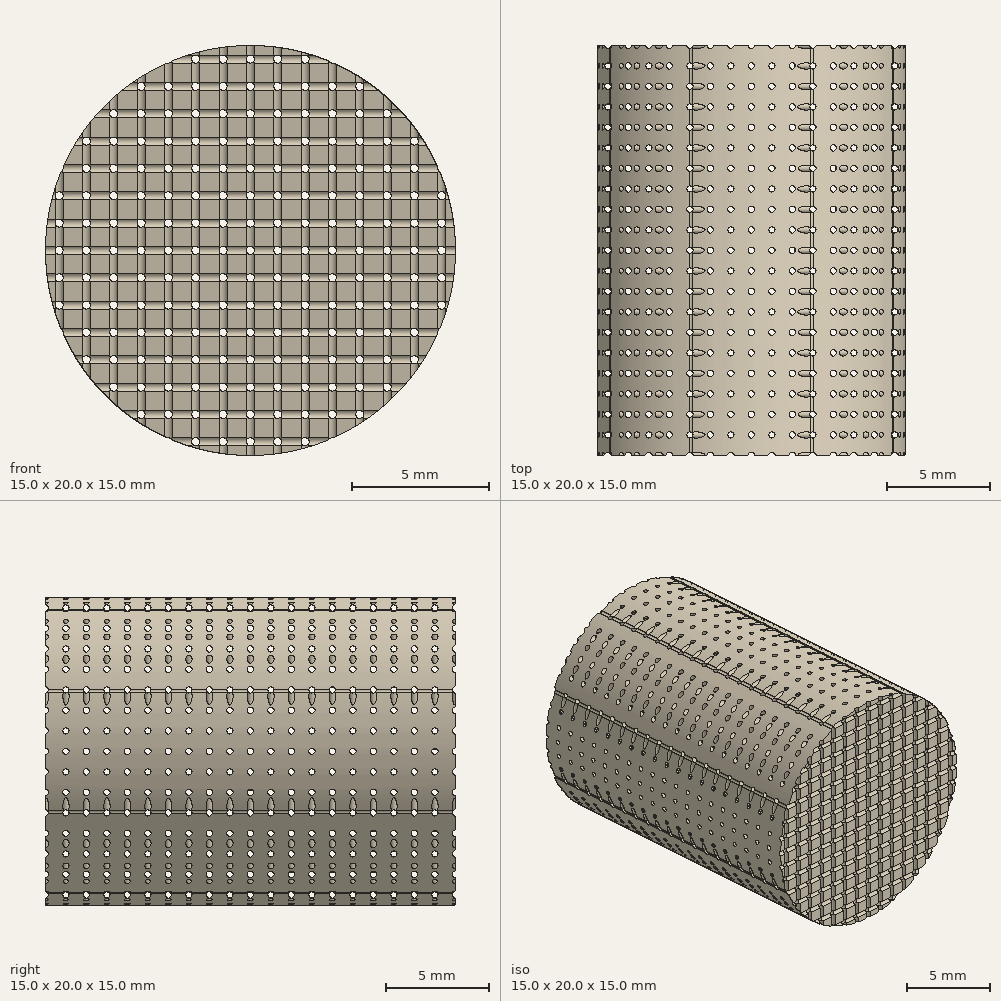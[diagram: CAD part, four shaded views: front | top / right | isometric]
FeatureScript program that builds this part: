
annotation { "Feature Type Name" : "Feature", "Feature Type Description" : "" }
export const myFeature = defineFeature(function(context is Context, id is Id, definition is map)
    precondition{}
    {
        {
            var Q0;
            Q0=qCreatedBy(makeId("Front.planeOp"),FACE);
            var sketch = newSketch(context, id + "F0", { "sketchPlane" : qUnion([Q0])});
            skCircle(sketch, "E0", {"center": v(0, 0) * mm, "radius": 7.5 * mm});
            skSolve(sketch);
        }
        {
            var Q0;
            Q0=qCreatedBy(makeId("Top.planeOp"),FACE);
            var sketch = newSketch(context, id + "F1", { "sketchPlane" : qUnion([Q0])});
            skLineSegment(sketch, "E1", {"start": v(0, 0) * mm, "end": v(0, 20) * mm});
            skSolve(sketch);
        }
        {
            var Q0;
            Q0 = qSketchRegion(id + "F0", true);
            var Q1;
            Q1 = qBodyType(qCreatedBy(id + "F1" ,EDGE), BodyType.WIRE);
            sweep(context, id + "F2", {"profiles" : qUnion([Q0]), "path" : qUnion([Q1])});
        }
        {
            var Q0;
            Q0=qCreatedBy(makeId("Front.planeOp"),FACE);
            var sketch = newSketch(context, id + "F3", { "sketchPlane" : qUnion([Q0])});
            skCircle(sketch, "E2", {"center": v(0, 0) * mm, "radius": 0.15 * mm});
            skCircle(sketch, "E3.0.1.0", {"center": v(0, 1) * mm, "radius": 0.15 * mm});
            skCircle(sketch, "E3.0.2.0", {"center": v(0, 2) * mm, "radius": 0.15 * mm});
            skCircle(sketch, "E3.0.3.0", {"center": v(0, 3) * mm, "radius": 0.15 * mm});
            skCircle(sketch, "E3.0.4.0", {"center": v(0, 4) * mm, "radius": 0.15 * mm});
            skCircle(sketch, "E3.0.5.0", {"center": v(0, 5) * mm, "radius": 0.15 * mm});
            skCircle(sketch, "E3.0.6.0", {"center": v(0, 6) * mm, "radius": 0.15 * mm});
            skCircle(sketch, "E3.0.7.0", {"center": v(0, 7) * mm, "radius": 0.15 * mm});
            skCircle(sketch, "E3.0.8.0", {"center": v(0, 8) * mm, "radius": 0.15 * mm});
            skCircle(sketch, "E3.0.9.0", {"center": v(0, 9) * mm, "radius": 0.15 * mm});
            skCircle(sketch, "E3.1.0.0", {"center": v(1, 0) * mm, "radius": 0.15 * mm});
            skCircle(sketch, "E3.1.1.0", {"center": v(1, 1) * mm, "radius": 0.15 * mm});
            skCircle(sketch, "E3.1.2.0", {"center": v(1, 2) * mm, "radius": 0.15 * mm});
            skCircle(sketch, "E3.1.3.0", {"center": v(1, 3) * mm, "radius": 0.15 * mm});
            skCircle(sketch, "E3.1.4.0", {"center": v(1, 4) * mm, "radius": 0.15 * mm});
            skCircle(sketch, "E3.1.5.0", {"center": v(1, 5) * mm, "radius": 0.15 * mm});
            skCircle(sketch, "E3.1.6.0", {"center": v(1, 6) * mm, "radius": 0.15 * mm});
            skCircle(sketch, "E3.1.7.0", {"center": v(1, 7) * mm, "radius": 0.15 * mm});
            skCircle(sketch, "E3.1.8.0", {"center": v(1, 8) * mm, "radius": 0.15 * mm});
            skCircle(sketch, "E3.1.9.0", {"center": v(1, 9) * mm, "radius": 0.15 * mm});
            skCircle(sketch, "E3.2.0.0", {"center": v(2, 0) * mm, "radius": 0.15 * mm});
            skCircle(sketch, "E3.2.1.0", {"center": v(2, 1) * mm, "radius": 0.15 * mm});
            skCircle(sketch, "E3.2.2.0", {"center": v(2, 2) * mm, "radius": 0.15 * mm});
            skCircle(sketch, "E3.2.3.0", {"center": v(2, 3) * mm, "radius": 0.15 * mm});
            skCircle(sketch, "E3.2.4.0", {"center": v(2, 4) * mm, "radius": 0.15 * mm});
            skCircle(sketch, "E3.2.5.0", {"center": v(2, 5) * mm, "radius": 0.15 * mm});
            skCircle(sketch, "E3.2.6.0", {"center": v(2, 6) * mm, "radius": 0.15 * mm});
            skCircle(sketch, "E3.2.7.0", {"center": v(2, 7) * mm, "radius": 0.15 * mm});
            skCircle(sketch, "E3.2.8.0", {"center": v(2, 8) * mm, "radius": 0.15 * mm});
            skCircle(sketch, "E3.2.9.0", {"center": v(2, 9) * mm, "radius": 0.15 * mm});
            skCircle(sketch, "E3.3.0.0", {"center": v(3, 0) * mm, "radius": 0.15 * mm});
            skCircle(sketch, "E3.3.1.0", {"center": v(3, 1) * mm, "radius": 0.15 * mm});
            skCircle(sketch, "E3.3.2.0", {"center": v(3, 2) * mm, "radius": 0.15 * mm});
            skCircle(sketch, "E3.3.3.0", {"center": v(3, 3) * mm, "radius": 0.15 * mm});
            skCircle(sketch, "E3.3.4.0", {"center": v(3, 4) * mm, "radius": 0.15 * mm});
            skCircle(sketch, "E3.3.5.0", {"center": v(3, 5) * mm, "radius": 0.15 * mm});
            skCircle(sketch, "E3.3.6.0", {"center": v(3, 6) * mm, "radius": 0.15 * mm});
            skCircle(sketch, "E3.3.7.0", {"center": v(3, 7) * mm, "radius": 0.15 * mm});
            skCircle(sketch, "E3.3.8.0", {"center": v(3, 8) * mm, "radius": 0.15 * mm});
            skCircle(sketch, "E3.3.9.0", {"center": v(3, 9) * mm, "radius": 0.15 * mm});
            skCircle(sketch, "E3.4.0.0", {"center": v(4, 0) * mm, "radius": 0.15 * mm});
            skCircle(sketch, "E3.4.1.0", {"center": v(4, 1) * mm, "radius": 0.15 * mm});
            skCircle(sketch, "E3.4.2.0", {"center": v(4, 2) * mm, "radius": 0.15 * mm});
            skCircle(sketch, "E3.4.3.0", {"center": v(4, 3) * mm, "radius": 0.15 * mm});
            skCircle(sketch, "E3.4.4.0", {"center": v(4, 4) * mm, "radius": 0.15 * mm});
            skCircle(sketch, "E3.4.5.0", {"center": v(4, 5) * mm, "radius": 0.15 * mm});
            skCircle(sketch, "E3.4.6.0", {"center": v(4, 6) * mm, "radius": 0.15 * mm});
            skCircle(sketch, "E3.4.7.0", {"center": v(4, 7) * mm, "radius": 0.15 * mm});
            skCircle(sketch, "E3.4.8.0", {"center": v(4, 8) * mm, "radius": 0.15 * mm});
            skCircle(sketch, "E3.4.9.0", {"center": v(4, 9) * mm, "radius": 0.15 * mm});
            skCircle(sketch, "E3.5.0.0", {"center": v(5, 0) * mm, "radius": 0.15 * mm});
            skCircle(sketch, "E3.5.1.0", {"center": v(5, 1) * mm, "radius": 0.15 * mm});
            skCircle(sketch, "E3.5.2.0", {"center": v(5, 2) * mm, "radius": 0.15 * mm});
            skCircle(sketch, "E3.5.3.0", {"center": v(5, 3) * mm, "radius": 0.15 * mm});
            skCircle(sketch, "E3.5.4.0", {"center": v(5, 4) * mm, "radius": 0.15 * mm});
            skCircle(sketch, "E3.5.5.0", {"center": v(5, 5) * mm, "radius": 0.15 * mm});
            skCircle(sketch, "E3.5.6.0", {"center": v(5, 6) * mm, "radius": 0.15 * mm});
            skCircle(sketch, "E3.5.7.0", {"center": v(5, 7) * mm, "radius": 0.15 * mm});
            skCircle(sketch, "E3.5.8.0", {"center": v(5, 8) * mm, "radius": 0.15 * mm});
            skCircle(sketch, "E3.5.9.0", {"center": v(5, 9) * mm, "radius": 0.15 * mm});
            skCircle(sketch, "E3.6.0.0", {"center": v(6, 0) * mm, "radius": 0.15 * mm});
            skCircle(sketch, "E3.6.1.0", {"center": v(6, 1) * mm, "radius": 0.15 * mm});
            skCircle(sketch, "E3.6.2.0", {"center": v(6, 2) * mm, "radius": 0.15 * mm});
            skCircle(sketch, "E3.6.3.0", {"center": v(6, 3) * mm, "radius": 0.15 * mm});
            skCircle(sketch, "E3.6.4.0", {"center": v(6, 4) * mm, "radius": 0.15 * mm});
            skCircle(sketch, "E3.6.5.0", {"center": v(6, 5) * mm, "radius": 0.15 * mm});
            skCircle(sketch, "E3.6.6.0", {"center": v(6, 6) * mm, "radius": 0.15 * mm});
            skCircle(sketch, "E3.6.7.0", {"center": v(6, 7) * mm, "radius": 0.15 * mm});
            skCircle(sketch, "E3.6.8.0", {"center": v(6, 8) * mm, "radius": 0.15 * mm});
            skCircle(sketch, "E3.6.9.0", {"center": v(6, 9) * mm, "radius": 0.15 * mm});
            skCircle(sketch, "E3.7.0.0", {"center": v(7, 0) * mm, "radius": 0.15 * mm});
            skCircle(sketch, "E3.7.1.0", {"center": v(7, 1) * mm, "radius": 0.15 * mm});
            skCircle(sketch, "E3.7.2.0", {"center": v(7, 2) * mm, "radius": 0.15 * mm});
            skCircle(sketch, "E3.7.3.0", {"center": v(7, 3) * mm, "radius": 0.15 * mm});
            skCircle(sketch, "E3.7.4.0", {"center": v(7, 4) * mm, "radius": 0.15 * mm});
            skCircle(sketch, "E3.7.5.0", {"center": v(7, 5) * mm, "radius": 0.15 * mm});
            skCircle(sketch, "E3.7.6.0", {"center": v(7, 6) * mm, "radius": 0.15 * mm});
            skCircle(sketch, "E3.7.7.0", {"center": v(7, 7) * mm, "radius": 0.15 * mm});
            skCircle(sketch, "E3.7.8.0", {"center": v(7, 8) * mm, "radius": 0.15 * mm});
            skCircle(sketch, "E3.7.9.0", {"center": v(7, 9) * mm, "radius": 0.15 * mm});
            skCircle(sketch, "E3.8.0.0", {"center": v(8, 0) * mm, "radius": 0.15 * mm});
            skCircle(sketch, "E3.8.1.0", {"center": v(8, 1) * mm, "radius": 0.15 * mm});
            skCircle(sketch, "E3.8.2.0", {"center": v(8, 2) * mm, "radius": 0.15 * mm});
            skCircle(sketch, "E3.8.3.0", {"center": v(8, 3) * mm, "radius": 0.15 * mm});
            skCircle(sketch, "E3.8.4.0", {"center": v(8, 4) * mm, "radius": 0.15 * mm});
            skCircle(sketch, "E3.8.5.0", {"center": v(8, 5) * mm, "radius": 0.15 * mm});
            skCircle(sketch, "E3.8.6.0", {"center": v(8, 6) * mm, "radius": 0.15 * mm});
            skCircle(sketch, "E3.8.7.0", {"center": v(8, 7) * mm, "radius": 0.15 * mm});
            skCircle(sketch, "E3.8.8.0", {"center": v(8, 8) * mm, "radius": 0.15 * mm});
            skCircle(sketch, "E3.8.9.0", {"center": v(8, 9) * mm, "radius": 0.15 * mm});
            skCircle(sketch, "E3.9.0.0", {"center": v(9, 0) * mm, "radius": 0.15 * mm});
            skCircle(sketch, "E3.9.1.0", {"center": v(9, 1) * mm, "radius": 0.15 * mm});
            skCircle(sketch, "E3.9.2.0", {"center": v(9, 2) * mm, "radius": 0.15 * mm});
            skCircle(sketch, "E3.9.3.0", {"center": v(9, 3) * mm, "radius": 0.15 * mm});
            skCircle(sketch, "E3.9.4.0", {"center": v(9, 4) * mm, "radius": 0.15 * mm});
            skCircle(sketch, "E3.9.5.0", {"center": v(9, 5) * mm, "radius": 0.15 * mm});
            skCircle(sketch, "E3.9.6.0", {"center": v(9, 6) * mm, "radius": 0.15 * mm});
            skCircle(sketch, "E3.9.7.0", {"center": v(9, 7) * mm, "radius": 0.15 * mm});
            skCircle(sketch, "E3.9.8.0", {"center": v(9, 8) * mm, "radius": 0.15 * mm});
            skCircle(sketch, "E3.9.9.0", {"center": v(9, 9) * mm, "radius": 0.15 * mm});
            skLineSegment(sketch, "E3.direction1", {"start": v(0, 0) * mm, "end": v(1, 0) * mm, "construction": true});
            skLineSegment(sketch, "E3.direction2", {"start": v(0, 0) * mm, "end": v(0, 1) * mm, "construction": true});
            skCircle(sketch, "E4.0.10.0", {"center": v(9, -1) * mm, "radius": 0.15 * mm});
            skCircle(sketch, "E4.0.11.0", {"center": v(9, -2) * mm, "radius": 0.15 * mm});
            skCircle(sketch, "E4.0.12.0", {"center": v(9, -3) * mm, "radius": 0.15 * mm});
            skCircle(sketch, "E4.0.13.0", {"center": v(9, -4) * mm, "radius": 0.15 * mm});
            skCircle(sketch, "E4.0.14.0", {"center": v(9, -5) * mm, "radius": 0.15 * mm});
            skCircle(sketch, "E4.0.15.0", {"center": v(9, -6) * mm, "radius": 0.15 * mm});
            skCircle(sketch, "E4.0.16.0", {"center": v(9, -7) * mm, "radius": 0.15 * mm});
            skCircle(sketch, "E4.0.17.0", {"center": v(9, -8) * mm, "radius": 0.15 * mm});
            skCircle(sketch, "E4.0.18.0", {"center": v(9, -9) * mm, "radius": 0.15 * mm});
            skCircle(sketch, "E4.0.19.0", {"center": v(9, -10) * mm, "radius": 0.15 * mm});
            skCircle(sketch, "E4.1.10.0", {"center": v(8, -1) * mm, "radius": 0.15 * mm});
            skCircle(sketch, "E4.1.11.0", {"center": v(8, -2) * mm, "radius": 0.15 * mm});
            skCircle(sketch, "E4.1.12.0", {"center": v(8, -3) * mm, "radius": 0.15 * mm});
            skCircle(sketch, "E4.1.13.0", {"center": v(8, -4) * mm, "radius": 0.15 * mm});
            skCircle(sketch, "E4.1.14.0", {"center": v(8, -5) * mm, "radius": 0.15 * mm});
            skCircle(sketch, "E4.1.15.0", {"center": v(8, -6) * mm, "radius": 0.15 * mm});
            skCircle(sketch, "E4.1.16.0", {"center": v(8, -7) * mm, "radius": 0.15 * mm});
            skCircle(sketch, "E4.1.17.0", {"center": v(8, -8) * mm, "radius": 0.15 * mm});
            skCircle(sketch, "E4.1.18.0", {"center": v(8, -9) * mm, "radius": 0.15 * mm});
            skCircle(sketch, "E4.1.19.0", {"center": v(8, -10) * mm, "radius": 0.15 * mm});
            skCircle(sketch, "E4.2.10.0", {"center": v(7, -1) * mm, "radius": 0.15 * mm});
            skCircle(sketch, "E4.2.11.0", {"center": v(7, -2) * mm, "radius": 0.15 * mm});
            skCircle(sketch, "E4.2.12.0", {"center": v(7, -3) * mm, "radius": 0.15 * mm});
            skCircle(sketch, "E4.2.13.0", {"center": v(7, -4) * mm, "radius": 0.15 * mm});
            skCircle(sketch, "E4.2.14.0", {"center": v(7, -5) * mm, "radius": 0.15 * mm});
            skCircle(sketch, "E4.2.15.0", {"center": v(7, -6) * mm, "radius": 0.15 * mm});
            skCircle(sketch, "E4.2.16.0", {"center": v(7, -7) * mm, "radius": 0.15 * mm});
            skCircle(sketch, "E4.2.17.0", {"center": v(7, -8) * mm, "radius": 0.15 * mm});
            skCircle(sketch, "E4.2.18.0", {"center": v(7, -9) * mm, "radius": 0.15 * mm});
            skCircle(sketch, "E4.2.19.0", {"center": v(7, -10) * mm, "radius": 0.15 * mm});
            skCircle(sketch, "E4.3.10.0", {"center": v(6, -1) * mm, "radius": 0.15 * mm});
            skCircle(sketch, "E4.3.11.0", {"center": v(6, -2) * mm, "radius": 0.15 * mm});
            skCircle(sketch, "E4.3.12.0", {"center": v(6, -3) * mm, "radius": 0.15 * mm});
            skCircle(sketch, "E4.3.13.0", {"center": v(6, -4) * mm, "radius": 0.15 * mm});
            skCircle(sketch, "E4.3.14.0", {"center": v(6, -5) * mm, "radius": 0.15 * mm});
            skCircle(sketch, "E4.3.15.0", {"center": v(6, -6) * mm, "radius": 0.15 * mm});
            skCircle(sketch, "E4.3.16.0", {"center": v(6, -7) * mm, "radius": 0.15 * mm});
            skCircle(sketch, "E4.3.17.0", {"center": v(6, -8) * mm, "radius": 0.15 * mm});
            skCircle(sketch, "E4.3.18.0", {"center": v(6, -9) * mm, "radius": 0.15 * mm});
            skCircle(sketch, "E4.3.19.0", {"center": v(6, -10) * mm, "radius": 0.15 * mm});
            skCircle(sketch, "E4.4.10.0", {"center": v(5, -1) * mm, "radius": 0.15 * mm});
            skCircle(sketch, "E4.4.11.0", {"center": v(5, -2) * mm, "radius": 0.15 * mm});
            skCircle(sketch, "E4.4.12.0", {"center": v(5, -3) * mm, "radius": 0.15 * mm});
            skCircle(sketch, "E4.4.13.0", {"center": v(5, -4) * mm, "radius": 0.15 * mm});
            skCircle(sketch, "E4.4.14.0", {"center": v(5, -5) * mm, "radius": 0.15 * mm});
            skCircle(sketch, "E4.4.15.0", {"center": v(5, -6) * mm, "radius": 0.15 * mm});
            skCircle(sketch, "E4.4.16.0", {"center": v(5, -7) * mm, "radius": 0.15 * mm});
            skCircle(sketch, "E4.4.17.0", {"center": v(5, -8) * mm, "radius": 0.15 * mm});
            skCircle(sketch, "E4.4.18.0", {"center": v(5, -9) * mm, "radius": 0.15 * mm});
            skCircle(sketch, "E4.4.19.0", {"center": v(5, -10) * mm, "radius": 0.15 * mm});
            skCircle(sketch, "E4.5.10.0", {"center": v(4, -1) * mm, "radius": 0.15 * mm});
            skCircle(sketch, "E4.5.11.0", {"center": v(4, -2) * mm, "radius": 0.15 * mm});
            skCircle(sketch, "E4.5.12.0", {"center": v(4, -3) * mm, "radius": 0.15 * mm});
            skCircle(sketch, "E4.5.13.0", {"center": v(4, -4) * mm, "radius": 0.15 * mm});
            skCircle(sketch, "E4.5.14.0", {"center": v(4, -5) * mm, "radius": 0.15 * mm});
            skCircle(sketch, "E4.5.15.0", {"center": v(4, -6) * mm, "radius": 0.15 * mm});
            skCircle(sketch, "E4.5.16.0", {"center": v(4, -7) * mm, "radius": 0.15 * mm});
            skCircle(sketch, "E4.5.17.0", {"center": v(4, -8) * mm, "radius": 0.15 * mm});
            skCircle(sketch, "E4.5.18.0", {"center": v(4, -9) * mm, "radius": 0.15 * mm});
            skCircle(sketch, "E4.5.19.0", {"center": v(4, -10) * mm, "radius": 0.15 * mm});
            skCircle(sketch, "E4.6.10.0", {"center": v(3, -1) * mm, "radius": 0.15 * mm});
            skCircle(sketch, "E4.6.11.0", {"center": v(3, -2) * mm, "radius": 0.15 * mm});
            skCircle(sketch, "E4.6.12.0", {"center": v(3, -3) * mm, "radius": 0.15 * mm});
            skCircle(sketch, "E4.6.13.0", {"center": v(3, -4) * mm, "radius": 0.15 * mm});
            skCircle(sketch, "E4.6.14.0", {"center": v(3, -5) * mm, "radius": 0.15 * mm});
            skCircle(sketch, "E4.6.15.0", {"center": v(3, -6) * mm, "radius": 0.15 * mm});
            skCircle(sketch, "E4.6.16.0", {"center": v(3, -7) * mm, "radius": 0.15 * mm});
            skCircle(sketch, "E4.6.17.0", {"center": v(3, -8) * mm, "radius": 0.15 * mm});
            skCircle(sketch, "E4.6.18.0", {"center": v(3, -9) * mm, "radius": 0.15 * mm});
            skCircle(sketch, "E4.6.19.0", {"center": v(3, -10) * mm, "radius": 0.15 * mm});
            skCircle(sketch, "E4.7.10.0", {"center": v(2, -1) * mm, "radius": 0.15 * mm});
            skCircle(sketch, "E4.7.11.0", {"center": v(2, -2) * mm, "radius": 0.15 * mm});
            skCircle(sketch, "E4.7.12.0", {"center": v(2, -3) * mm, "radius": 0.15 * mm});
            skCircle(sketch, "E4.7.13.0", {"center": v(2, -4) * mm, "radius": 0.15 * mm});
            skCircle(sketch, "E4.7.14.0", {"center": v(2, -5) * mm, "radius": 0.15 * mm});
            skCircle(sketch, "E4.7.15.0", {"center": v(2, -6) * mm, "radius": 0.15 * mm});
            skCircle(sketch, "E4.7.16.0", {"center": v(2, -7) * mm, "radius": 0.15 * mm});
            skCircle(sketch, "E4.7.17.0", {"center": v(2, -8) * mm, "radius": 0.15 * mm});
            skCircle(sketch, "E4.7.18.0", {"center": v(2, -9) * mm, "radius": 0.15 * mm});
            skCircle(sketch, "E4.7.19.0", {"center": v(2, -10) * mm, "radius": 0.15 * mm});
            skCircle(sketch, "E4.8.10.0", {"center": v(1, -1) * mm, "radius": 0.15 * mm});
            skCircle(sketch, "E4.8.11.0", {"center": v(1, -2) * mm, "radius": 0.15 * mm});
            skCircle(sketch, "E4.8.12.0", {"center": v(1, -3) * mm, "radius": 0.15 * mm});
            skCircle(sketch, "E4.8.13.0", {"center": v(1, -4) * mm, "radius": 0.15 * mm});
            skCircle(sketch, "E4.8.14.0", {"center": v(1, -5) * mm, "radius": 0.15 * mm});
            skCircle(sketch, "E4.8.15.0", {"center": v(1, -6) * mm, "radius": 0.15 * mm});
            skCircle(sketch, "E4.8.16.0", {"center": v(1, -7) * mm, "radius": 0.15 * mm});
            skCircle(sketch, "E4.8.17.0", {"center": v(1, -8) * mm, "radius": 0.15 * mm});
            skCircle(sketch, "E4.8.18.0", {"center": v(1, -9) * mm, "radius": 0.15 * mm});
            skCircle(sketch, "E4.8.19.0", {"center": v(1, -10) * mm, "radius": 0.15 * mm});
            skCircle(sketch, "E4.9.10.0", {"center": v(0, -1) * mm, "radius": 0.15 * mm});
            skCircle(sketch, "E4.9.11.0", {"center": v(0, -2) * mm, "radius": 0.15 * mm});
            skCircle(sketch, "E4.9.12.0", {"center": v(0, -3) * mm, "radius": 0.15 * mm});
            skCircle(sketch, "E4.9.13.0", {"center": v(0, -4) * mm, "radius": 0.15 * mm});
            skCircle(sketch, "E4.9.14.0", {"center": v(0, -5) * mm, "radius": 0.15 * mm});
            skCircle(sketch, "E4.9.15.0", {"center": v(0, -6) * mm, "radius": 0.15 * mm});
            skCircle(sketch, "E4.9.16.0", {"center": v(0, -7) * mm, "radius": 0.15 * mm});
            skCircle(sketch, "E4.9.17.0", {"center": v(0, -8) * mm, "radius": 0.15 * mm});
            skCircle(sketch, "E4.9.18.0", {"center": v(0, -9) * mm, "radius": 0.15 * mm});
            skCircle(sketch, "E4.9.19.0", {"center": v(0, -10) * mm, "radius": 0.15 * mm});
            skCircle(sketch, "E4.10.0.0", {"center": v(-1, 9) * mm, "radius": 0.15 * mm});
            skCircle(sketch, "E4.10.1.0", {"center": v(-1, 8) * mm, "radius": 0.15 * mm});
            skCircle(sketch, "E4.10.2.0", {"center": v(-1, 7) * mm, "radius": 0.15 * mm});
            skCircle(sketch, "E4.10.3.0", {"center": v(-1, 6) * mm, "radius": 0.15 * mm});
            skCircle(sketch, "E4.10.4.0", {"center": v(-1, 5) * mm, "radius": 0.15 * mm});
            skCircle(sketch, "E4.10.5.0", {"center": v(-1, 4) * mm, "radius": 0.15 * mm});
            skCircle(sketch, "E4.10.6.0", {"center": v(-1, 3) * mm, "radius": 0.15 * mm});
            skCircle(sketch, "E4.10.7.0", {"center": v(-1, 2) * mm, "radius": 0.15 * mm});
            skCircle(sketch, "E4.10.8.0", {"center": v(-1, 1) * mm, "radius": 0.15 * mm});
            skCircle(sketch, "E4.10.9.0", {"center": v(-1, 0) * mm, "radius": 0.15 * mm});
            skCircle(sketch, "E4.10.10.0", {"center": v(-1, -1) * mm, "radius": 0.15 * mm});
            skCircle(sketch, "E4.10.11.0", {"center": v(-1, -2) * mm, "radius": 0.15 * mm});
            skCircle(sketch, "E4.10.12.0", {"center": v(-1, -3) * mm, "radius": 0.15 * mm});
            skCircle(sketch, "E4.10.13.0", {"center": v(-1, -4) * mm, "radius": 0.15 * mm});
            skCircle(sketch, "E4.10.14.0", {"center": v(-1, -5) * mm, "radius": 0.15 * mm});
            skCircle(sketch, "E4.10.15.0", {"center": v(-1, -6) * mm, "radius": 0.15 * mm});
            skCircle(sketch, "E4.10.16.0", {"center": v(-1, -7) * mm, "radius": 0.15 * mm});
            skCircle(sketch, "E4.10.17.0", {"center": v(-1, -8) * mm, "radius": 0.15 * mm});
            skCircle(sketch, "E4.10.18.0", {"center": v(-1, -9) * mm, "radius": 0.15 * mm});
            skCircle(sketch, "E4.10.19.0", {"center": v(-1, -10) * mm, "radius": 0.15 * mm});
            skCircle(sketch, "E4.11.0.0", {"center": v(-2, 9) * mm, "radius": 0.15 * mm});
            skCircle(sketch, "E4.11.1.0", {"center": v(-2, 8) * mm, "radius": 0.15 * mm});
            skCircle(sketch, "E4.11.2.0", {"center": v(-2, 7) * mm, "radius": 0.15 * mm});
            skCircle(sketch, "E4.11.3.0", {"center": v(-2, 6) * mm, "radius": 0.15 * mm});
            skCircle(sketch, "E4.11.4.0", {"center": v(-2, 5) * mm, "radius": 0.15 * mm});
            skCircle(sketch, "E4.11.5.0", {"center": v(-2, 4) * mm, "radius": 0.15 * mm});
            skCircle(sketch, "E4.11.6.0", {"center": v(-2, 3) * mm, "radius": 0.15 * mm});
            skCircle(sketch, "E4.11.7.0", {"center": v(-2, 2) * mm, "radius": 0.15 * mm});
            skCircle(sketch, "E4.11.8.0", {"center": v(-2, 1) * mm, "radius": 0.15 * mm});
            skCircle(sketch, "E4.11.9.0", {"center": v(-2, 0) * mm, "radius": 0.15 * mm});
            skCircle(sketch, "E4.11.10.0", {"center": v(-2, -1) * mm, "radius": 0.15 * mm});
            skCircle(sketch, "E4.11.11.0", {"center": v(-2, -2) * mm, "radius": 0.15 * mm});
            skCircle(sketch, "E4.11.12.0", {"center": v(-2, -3) * mm, "radius": 0.15 * mm});
            skCircle(sketch, "E4.11.13.0", {"center": v(-2, -4) * mm, "radius": 0.15 * mm});
            skCircle(sketch, "E4.11.14.0", {"center": v(-2, -5) * mm, "radius": 0.15 * mm});
            skCircle(sketch, "E4.11.15.0", {"center": v(-2, -6) * mm, "radius": 0.15 * mm});
            skCircle(sketch, "E4.11.16.0", {"center": v(-2, -7) * mm, "radius": 0.15 * mm});
            skCircle(sketch, "E4.11.17.0", {"center": v(-2, -8) * mm, "radius": 0.15 * mm});
            skCircle(sketch, "E4.11.18.0", {"center": v(-2, -9) * mm, "radius": 0.15 * mm});
            skCircle(sketch, "E4.11.19.0", {"center": v(-2, -10) * mm, "radius": 0.15 * mm});
            skCircle(sketch, "E4.12.0.0", {"center": v(-3, 9) * mm, "radius": 0.15 * mm});
            skCircle(sketch, "E4.12.1.0", {"center": v(-3, 8) * mm, "radius": 0.15 * mm});
            skCircle(sketch, "E4.12.2.0", {"center": v(-3, 7) * mm, "radius": 0.15 * mm});
            skCircle(sketch, "E4.12.3.0", {"center": v(-3, 6) * mm, "radius": 0.15 * mm});
            skCircle(sketch, "E4.12.4.0", {"center": v(-3, 5) * mm, "radius": 0.15 * mm});
            skCircle(sketch, "E4.12.5.0", {"center": v(-3, 4) * mm, "radius": 0.15 * mm});
            skCircle(sketch, "E4.12.6.0", {"center": v(-3, 3) * mm, "radius": 0.15 * mm});
            skCircle(sketch, "E4.12.7.0", {"center": v(-3, 2) * mm, "radius": 0.15 * mm});
            skCircle(sketch, "E4.12.8.0", {"center": v(-3, 1) * mm, "radius": 0.15 * mm});
            skCircle(sketch, "E4.12.9.0", {"center": v(-3, 0) * mm, "radius": 0.15 * mm});
            skCircle(sketch, "E4.12.10.0", {"center": v(-3, -1) * mm, "radius": 0.15 * mm});
            skCircle(sketch, "E4.12.11.0", {"center": v(-3, -2) * mm, "radius": 0.15 * mm});
            skCircle(sketch, "E4.12.12.0", {"center": v(-3, -3) * mm, "radius": 0.15 * mm});
            skCircle(sketch, "E4.12.13.0", {"center": v(-3, -4) * mm, "radius": 0.15 * mm});
            skCircle(sketch, "E4.12.14.0", {"center": v(-3, -5) * mm, "radius": 0.15 * mm});
            skCircle(sketch, "E4.12.15.0", {"center": v(-3, -6) * mm, "radius": 0.15 * mm});
            skCircle(sketch, "E4.12.16.0", {"center": v(-3, -7) * mm, "radius": 0.15 * mm});
            skCircle(sketch, "E4.12.17.0", {"center": v(-3, -8) * mm, "radius": 0.15 * mm});
            skCircle(sketch, "E4.12.18.0", {"center": v(-3, -9) * mm, "radius": 0.15 * mm});
            skCircle(sketch, "E4.12.19.0", {"center": v(-3, -10) * mm, "radius": 0.15 * mm});
            skCircle(sketch, "E4.13.0.0", {"center": v(-4, 9) * mm, "radius": 0.15 * mm});
            skCircle(sketch, "E4.13.1.0", {"center": v(-4, 8) * mm, "radius": 0.15 * mm});
            skCircle(sketch, "E4.13.2.0", {"center": v(-4, 7) * mm, "radius": 0.15 * mm});
            skCircle(sketch, "E4.13.3.0", {"center": v(-4, 6) * mm, "radius": 0.15 * mm});
            skCircle(sketch, "E4.13.4.0", {"center": v(-4, 5) * mm, "radius": 0.15 * mm});
            skCircle(sketch, "E4.13.5.0", {"center": v(-4, 4) * mm, "radius": 0.15 * mm});
            skCircle(sketch, "E4.13.6.0", {"center": v(-4, 3) * mm, "radius": 0.15 * mm});
            skCircle(sketch, "E4.13.7.0", {"center": v(-4, 2) * mm, "radius": 0.15 * mm});
            skCircle(sketch, "E4.13.8.0", {"center": v(-4, 1) * mm, "radius": 0.15 * mm});
            skCircle(sketch, "E4.13.9.0", {"center": v(-4, 0) * mm, "radius": 0.15 * mm});
            skCircle(sketch, "E4.13.10.0", {"center": v(-4, -1) * mm, "radius": 0.15 * mm});
            skCircle(sketch, "E4.13.11.0", {"center": v(-4, -2) * mm, "radius": 0.15 * mm});
            skCircle(sketch, "E4.13.12.0", {"center": v(-4, -3) * mm, "radius": 0.15 * mm});
            skCircle(sketch, "E4.13.13.0", {"center": v(-4, -4) * mm, "radius": 0.15 * mm});
            skCircle(sketch, "E4.13.14.0", {"center": v(-4, -5) * mm, "radius": 0.15 * mm});
            skCircle(sketch, "E4.13.15.0", {"center": v(-4, -6) * mm, "radius": 0.15 * mm});
            skCircle(sketch, "E4.13.16.0", {"center": v(-4, -7) * mm, "radius": 0.15 * mm});
            skCircle(sketch, "E4.13.17.0", {"center": v(-4, -8) * mm, "radius": 0.15 * mm});
            skCircle(sketch, "E4.13.18.0", {"center": v(-4, -9) * mm, "radius": 0.15 * mm});
            skCircle(sketch, "E4.13.19.0", {"center": v(-4, -10) * mm, "radius": 0.15 * mm});
            skCircle(sketch, "E4.14.0.0", {"center": v(-5, 9) * mm, "radius": 0.15 * mm});
            skCircle(sketch, "E4.14.1.0", {"center": v(-5, 8) * mm, "radius": 0.15 * mm});
            skCircle(sketch, "E4.14.2.0", {"center": v(-5, 7) * mm, "radius": 0.15 * mm});
            skCircle(sketch, "E4.14.3.0", {"center": v(-5, 6) * mm, "radius": 0.15 * mm});
            skCircle(sketch, "E4.14.4.0", {"center": v(-5, 5) * mm, "radius": 0.15 * mm});
            skCircle(sketch, "E4.14.5.0", {"center": v(-5, 4) * mm, "radius": 0.15 * mm});
            skCircle(sketch, "E4.14.6.0", {"center": v(-5, 3) * mm, "radius": 0.15 * mm});
            skCircle(sketch, "E4.14.7.0", {"center": v(-5, 2) * mm, "radius": 0.15 * mm});
            skCircle(sketch, "E4.14.8.0", {"center": v(-5, 1) * mm, "radius": 0.15 * mm});
            skCircle(sketch, "E4.14.9.0", {"center": v(-5, 0) * mm, "radius": 0.15 * mm});
            skCircle(sketch, "E4.14.10.0", {"center": v(-5, -1) * mm, "radius": 0.15 * mm});
            skCircle(sketch, "E4.14.11.0", {"center": v(-5, -2) * mm, "radius": 0.15 * mm});
            skCircle(sketch, "E4.14.12.0", {"center": v(-5, -3) * mm, "radius": 0.15 * mm});
            skCircle(sketch, "E4.14.13.0", {"center": v(-5, -4) * mm, "radius": 0.15 * mm});
            skCircle(sketch, "E4.14.14.0", {"center": v(-5, -5) * mm, "radius": 0.15 * mm});
            skCircle(sketch, "E4.14.15.0", {"center": v(-5, -6) * mm, "radius": 0.15 * mm});
            skCircle(sketch, "E4.14.16.0", {"center": v(-5, -7) * mm, "radius": 0.15 * mm});
            skCircle(sketch, "E4.14.17.0", {"center": v(-5, -8) * mm, "radius": 0.15 * mm});
            skCircle(sketch, "E4.14.18.0", {"center": v(-5, -9) * mm, "radius": 0.15 * mm});
            skCircle(sketch, "E4.14.19.0", {"center": v(-5, -10) * mm, "radius": 0.15 * mm});
            skCircle(sketch, "E4.15.0.0", {"center": v(-6, 9) * mm, "radius": 0.15 * mm});
            skCircle(sketch, "E4.15.1.0", {"center": v(-6, 8) * mm, "radius": 0.15 * mm});
            skCircle(sketch, "E4.15.2.0", {"center": v(-6, 7) * mm, "radius": 0.15 * mm});
            skCircle(sketch, "E4.15.3.0", {"center": v(-6, 6) * mm, "radius": 0.15 * mm});
            skCircle(sketch, "E4.15.4.0", {"center": v(-6, 5) * mm, "radius": 0.15 * mm});
            skCircle(sketch, "E4.15.5.0", {"center": v(-6, 4) * mm, "radius": 0.15 * mm});
            skCircle(sketch, "E4.15.6.0", {"center": v(-6, 3) * mm, "radius": 0.15 * mm});
            skCircle(sketch, "E4.15.7.0", {"center": v(-6, 2) * mm, "radius": 0.15 * mm});
            skCircle(sketch, "E4.15.8.0", {"center": v(-6, 1) * mm, "radius": 0.15 * mm});
            skCircle(sketch, "E4.15.9.0", {"center": v(-6, 0) * mm, "radius": 0.15 * mm});
            skCircle(sketch, "E4.15.10.0", {"center": v(-6, -1) * mm, "radius": 0.15 * mm});
            skCircle(sketch, "E4.15.11.0", {"center": v(-6, -2) * mm, "radius": 0.15 * mm});
            skCircle(sketch, "E4.15.12.0", {"center": v(-6, -3) * mm, "radius": 0.15 * mm});
            skCircle(sketch, "E4.15.13.0", {"center": v(-6, -4) * mm, "radius": 0.15 * mm});
            skCircle(sketch, "E4.15.14.0", {"center": v(-6, -5) * mm, "radius": 0.15 * mm});
            skCircle(sketch, "E4.15.15.0", {"center": v(-6, -6) * mm, "radius": 0.15 * mm});
            skCircle(sketch, "E4.15.16.0", {"center": v(-6, -7) * mm, "radius": 0.15 * mm});
            skCircle(sketch, "E4.15.17.0", {"center": v(-6, -8) * mm, "radius": 0.15 * mm});
            skCircle(sketch, "E4.15.18.0", {"center": v(-6, -9) * mm, "radius": 0.15 * mm});
            skCircle(sketch, "E4.15.19.0", {"center": v(-6, -10) * mm, "radius": 0.15 * mm});
            skCircle(sketch, "E4.16.0.0", {"center": v(-7, 9) * mm, "radius": 0.15 * mm});
            skCircle(sketch, "E4.16.1.0", {"center": v(-7, 8) * mm, "radius": 0.15 * mm});
            skCircle(sketch, "E4.16.2.0", {"center": v(-7, 7) * mm, "radius": 0.15 * mm});
            skCircle(sketch, "E4.16.3.0", {"center": v(-7, 6) * mm, "radius": 0.15 * mm});
            skCircle(sketch, "E4.16.4.0", {"center": v(-7, 5) * mm, "radius": 0.15 * mm});
            skCircle(sketch, "E4.16.5.0", {"center": v(-7, 4) * mm, "radius": 0.15 * mm});
            skCircle(sketch, "E4.16.6.0", {"center": v(-7, 3) * mm, "radius": 0.15 * mm});
            skCircle(sketch, "E4.16.7.0", {"center": v(-7, 2) * mm, "radius": 0.15 * mm});
            skCircle(sketch, "E4.16.8.0", {"center": v(-7, 1) * mm, "radius": 0.15 * mm});
            skCircle(sketch, "E4.16.9.0", {"center": v(-7, 0) * mm, "radius": 0.15 * mm});
            skCircle(sketch, "E4.16.10.0", {"center": v(-7, -1) * mm, "radius": 0.15 * mm});
            skCircle(sketch, "E4.16.11.0", {"center": v(-7, -2) * mm, "radius": 0.15 * mm});
            skCircle(sketch, "E4.16.12.0", {"center": v(-7, -3) * mm, "radius": 0.15 * mm});
            skCircle(sketch, "E4.16.13.0", {"center": v(-7, -4) * mm, "radius": 0.15 * mm});
            skCircle(sketch, "E4.16.14.0", {"center": v(-7, -5) * mm, "radius": 0.15 * mm});
            skCircle(sketch, "E4.16.15.0", {"center": v(-7, -6) * mm, "radius": 0.15 * mm});
            skCircle(sketch, "E4.16.16.0", {"center": v(-7, -7) * mm, "radius": 0.15 * mm});
            skCircle(sketch, "E4.16.17.0", {"center": v(-7, -8) * mm, "radius": 0.15 * mm});
            skCircle(sketch, "E4.16.18.0", {"center": v(-7, -9) * mm, "radius": 0.15 * mm});
            skCircle(sketch, "E4.16.19.0", {"center": v(-7, -10) * mm, "radius": 0.15 * mm});
            skCircle(sketch, "E4.17.0.0", {"center": v(-8, 9) * mm, "radius": 0.15 * mm});
            skCircle(sketch, "E4.17.1.0", {"center": v(-8, 8) * mm, "radius": 0.15 * mm});
            skCircle(sketch, "E4.17.2.0", {"center": v(-8, 7) * mm, "radius": 0.15 * mm});
            skCircle(sketch, "E4.17.3.0", {"center": v(-8, 6) * mm, "radius": 0.15 * mm});
            skCircle(sketch, "E4.17.4.0", {"center": v(-8, 5) * mm, "radius": 0.15 * mm});
            skCircle(sketch, "E4.17.5.0", {"center": v(-8, 4) * mm, "radius": 0.15 * mm});
            skCircle(sketch, "E4.17.6.0", {"center": v(-8, 3) * mm, "radius": 0.15 * mm});
            skCircle(sketch, "E4.17.7.0", {"center": v(-8, 2) * mm, "radius": 0.15 * mm});
            skCircle(sketch, "E4.17.8.0", {"center": v(-8, 1) * mm, "radius": 0.15 * mm});
            skCircle(sketch, "E4.17.9.0", {"center": v(-8, 0) * mm, "radius": 0.15 * mm});
            skCircle(sketch, "E4.17.10.0", {"center": v(-8, -1) * mm, "radius": 0.15 * mm});
            skCircle(sketch, "E4.17.11.0", {"center": v(-8, -2) * mm, "radius": 0.15 * mm});
            skCircle(sketch, "E4.17.12.0", {"center": v(-8, -3) * mm, "radius": 0.15 * mm});
            skCircle(sketch, "E4.17.13.0", {"center": v(-8, -4) * mm, "radius": 0.15 * mm});
            skCircle(sketch, "E4.17.14.0", {"center": v(-8, -5) * mm, "radius": 0.15 * mm});
            skCircle(sketch, "E4.17.15.0", {"center": v(-8, -6) * mm, "radius": 0.15 * mm});
            skCircle(sketch, "E4.17.16.0", {"center": v(-8, -7) * mm, "radius": 0.15 * mm});
            skCircle(sketch, "E4.17.17.0", {"center": v(-8, -8) * mm, "radius": 0.15 * mm});
            skCircle(sketch, "E4.17.18.0", {"center": v(-8, -9) * mm, "radius": 0.15 * mm});
            skCircle(sketch, "E4.17.19.0", {"center": v(-8, -10) * mm, "radius": 0.15 * mm});
            skCircle(sketch, "E4.18.0.0", {"center": v(-9, 9) * mm, "radius": 0.15 * mm});
            skCircle(sketch, "E4.18.1.0", {"center": v(-9, 8) * mm, "radius": 0.15 * mm});
            skCircle(sketch, "E4.18.2.0", {"center": v(-9, 7) * mm, "radius": 0.15 * mm});
            skCircle(sketch, "E4.18.3.0", {"center": v(-9, 6) * mm, "radius": 0.15 * mm});
            skCircle(sketch, "E4.18.4.0", {"center": v(-9, 5) * mm, "radius": 0.15 * mm});
            skCircle(sketch, "E4.18.5.0", {"center": v(-9, 4) * mm, "radius": 0.15 * mm});
            skCircle(sketch, "E4.18.6.0", {"center": v(-9, 3) * mm, "radius": 0.15 * mm});
            skCircle(sketch, "E4.18.7.0", {"center": v(-9, 2) * mm, "radius": 0.15 * mm});
            skCircle(sketch, "E4.18.8.0", {"center": v(-9, 1) * mm, "radius": 0.15 * mm});
            skCircle(sketch, "E4.18.9.0", {"center": v(-9, 0) * mm, "radius": 0.15 * mm});
            skCircle(sketch, "E4.18.10.0", {"center": v(-9, -1) * mm, "radius": 0.15 * mm});
            skCircle(sketch, "E4.18.11.0", {"center": v(-9, -2) * mm, "radius": 0.15 * mm});
            skCircle(sketch, "E4.18.12.0", {"center": v(-9, -3) * mm, "radius": 0.15 * mm});
            skCircle(sketch, "E4.18.13.0", {"center": v(-9, -4) * mm, "radius": 0.15 * mm});
            skCircle(sketch, "E4.18.14.0", {"center": v(-9, -5) * mm, "radius": 0.15 * mm});
            skCircle(sketch, "E4.18.15.0", {"center": v(-9, -6) * mm, "radius": 0.15 * mm});
            skCircle(sketch, "E4.18.16.0", {"center": v(-9, -7) * mm, "radius": 0.15 * mm});
            skCircle(sketch, "E4.18.17.0", {"center": v(-9, -8) * mm, "radius": 0.15 * mm});
            skCircle(sketch, "E4.18.18.0", {"center": v(-9, -9) * mm, "radius": 0.15 * mm});
            skCircle(sketch, "E4.18.19.0", {"center": v(-9, -10) * mm, "radius": 0.15 * mm});
            skCircle(sketch, "E4.19.0.0", {"center": v(-10, 9) * mm, "radius": 0.15 * mm});
            skCircle(sketch, "E4.19.1.0", {"center": v(-10, 8) * mm, "radius": 0.15 * mm});
            skCircle(sketch, "E4.19.2.0", {"center": v(-10, 7) * mm, "radius": 0.15 * mm});
            skCircle(sketch, "E4.19.3.0", {"center": v(-10, 6) * mm, "radius": 0.15 * mm});
            skCircle(sketch, "E4.19.4.0", {"center": v(-10, 5) * mm, "radius": 0.15 * mm});
            skCircle(sketch, "E4.19.5.0", {"center": v(-10, 4) * mm, "radius": 0.15 * mm});
            skCircle(sketch, "E4.19.6.0", {"center": v(-10, 3) * mm, "radius": 0.15 * mm});
            skCircle(sketch, "E4.19.7.0", {"center": v(-10, 2) * mm, "radius": 0.15 * mm});
            skCircle(sketch, "E4.19.8.0", {"center": v(-10, 1) * mm, "radius": 0.15 * mm});
            skCircle(sketch, "E4.19.9.0", {"center": v(-10, 0) * mm, "radius": 0.15 * mm});
            skCircle(sketch, "E4.19.10.0", {"center": v(-10, -1) * mm, "radius": 0.15 * mm});
            skCircle(sketch, "E4.19.11.0", {"center": v(-10, -2) * mm, "radius": 0.15 * mm});
            skCircle(sketch, "E4.19.12.0", {"center": v(-10, -3) * mm, "radius": 0.15 * mm});
            skCircle(sketch, "E4.19.13.0", {"center": v(-10, -4) * mm, "radius": 0.15 * mm});
            skCircle(sketch, "E4.19.14.0", {"center": v(-10, -5) * mm, "radius": 0.15 * mm});
            skCircle(sketch, "E4.19.15.0", {"center": v(-10, -6) * mm, "radius": 0.15 * mm});
            skCircle(sketch, "E4.19.16.0", {"center": v(-10, -7) * mm, "radius": 0.15 * mm});
            skCircle(sketch, "E4.19.17.0", {"center": v(-10, -8) * mm, "radius": 0.15 * mm});
            skCircle(sketch, "E4.19.18.0", {"center": v(-10, -9) * mm, "radius": 0.15 * mm});
            skCircle(sketch, "E4.19.19.0", {"center": v(-10, -10) * mm, "radius": 0.15 * mm});
            skLineSegment(sketch, "E4.direction1", {"start": v(9, 9) * mm, "end": v(8, 9) * mm, "construction": true});
            skLineSegment(sketch, "E4.direction2", {"start": v(9, 9) * mm, "end": v(9, 8) * mm, "construction": true});
            skSolve(sketch);
        }
        {
            var Q0;
            Q0 = qSketchRegion(id + "F3", true);
            extrude(context, id + "F4", {"entities" : qUnion([Q0]), "operationType" : NewBodyOperationType.REMOVE, "oppositeDirection" : true, "depth" : 40 * mm, "offsetDistance" : 25 * mm});
        }
        {
            var Q0;
            Q0=qCreatedBy(makeId("Top.planeOp"),FACE);
            var sketch = newSketch(context, id + "F5", { "sketchPlane" : qUnion([Q0])});
            skCircle(sketch, "E5", {"center": v(0, 0) * mm, "radius": 0.15 * mm});
            skCircle(sketch, "E6.0.1.0", {"center": v(0, 1) * mm, "radius": 0.15 * mm});
            skCircle(sketch, "E6.0.2.0", {"center": v(0, 2) * mm, "radius": 0.15 * mm});
            skCircle(sketch, "E6.0.3.0", {"center": v(0, 3) * mm, "radius": 0.15 * mm});
            skCircle(sketch, "E6.0.4.0", {"center": v(0, 4) * mm, "radius": 0.15 * mm});
            skCircle(sketch, "E6.0.5.0", {"center": v(0, 5) * mm, "radius": 0.15 * mm});
            skCircle(sketch, "E6.0.6.0", {"center": v(0, 6) * mm, "radius": 0.15 * mm});
            skCircle(sketch, "E6.0.7.0", {"center": v(0, 7) * mm, "radius": 0.15 * mm});
            skCircle(sketch, "E6.0.8.0", {"center": v(0, 8) * mm, "radius": 0.15 * mm});
            skCircle(sketch, "E6.0.9.0", {"center": v(0, 9) * mm, "radius": 0.15 * mm});
            skCircle(sketch, "E6.1.0.0", {"center": v(1, 0) * mm, "radius": 0.15 * mm});
            skCircle(sketch, "E6.1.1.0", {"center": v(1, 1) * mm, "radius": 0.15 * mm});
            skCircle(sketch, "E6.1.2.0", {"center": v(1, 2) * mm, "radius": 0.15 * mm});
            skCircle(sketch, "E6.1.3.0", {"center": v(1, 3) * mm, "radius": 0.15 * mm});
            skCircle(sketch, "E6.1.4.0", {"center": v(1, 4) * mm, "radius": 0.15 * mm});
            skCircle(sketch, "E6.1.5.0", {"center": v(1, 5) * mm, "radius": 0.15 * mm});
            skCircle(sketch, "E6.1.6.0", {"center": v(1, 6) * mm, "radius": 0.15 * mm});
            skCircle(sketch, "E6.1.7.0", {"center": v(1, 7) * mm, "radius": 0.15 * mm});
            skCircle(sketch, "E6.1.8.0", {"center": v(1, 8) * mm, "radius": 0.15 * mm});
            skCircle(sketch, "E6.1.9.0", {"center": v(1, 9) * mm, "radius": 0.15 * mm});
            skCircle(sketch, "E6.2.0.0", {"center": v(2, 0) * mm, "radius": 0.15 * mm});
            skCircle(sketch, "E6.2.1.0", {"center": v(2, 1) * mm, "radius": 0.15 * mm});
            skCircle(sketch, "E6.2.2.0", {"center": v(2, 2) * mm, "radius": 0.15 * mm});
            skCircle(sketch, "E6.2.3.0", {"center": v(2, 3) * mm, "radius": 0.15 * mm});
            skCircle(sketch, "E6.2.4.0", {"center": v(2, 4) * mm, "radius": 0.15 * mm});
            skCircle(sketch, "E6.2.5.0", {"center": v(2, 5) * mm, "radius": 0.15 * mm});
            skCircle(sketch, "E6.2.6.0", {"center": v(2, 6) * mm, "radius": 0.15 * mm});
            skCircle(sketch, "E6.2.7.0", {"center": v(2, 7) * mm, "radius": 0.15 * mm});
            skCircle(sketch, "E6.2.8.0", {"center": v(2, 8) * mm, "radius": 0.15 * mm});
            skCircle(sketch, "E6.2.9.0", {"center": v(2, 9) * mm, "radius": 0.15 * mm});
            skCircle(sketch, "E6.3.0.0", {"center": v(3, 0) * mm, "radius": 0.15 * mm});
            skCircle(sketch, "E6.3.1.0", {"center": v(3, 1) * mm, "radius": 0.15 * mm});
            skCircle(sketch, "E6.3.2.0", {"center": v(3, 2) * mm, "radius": 0.15 * mm});
            skCircle(sketch, "E6.3.3.0", {"center": v(3, 3) * mm, "radius": 0.15 * mm});
            skCircle(sketch, "E6.3.4.0", {"center": v(3, 4) * mm, "radius": 0.15 * mm});
            skCircle(sketch, "E6.3.5.0", {"center": v(3, 5) * mm, "radius": 0.15 * mm});
            skCircle(sketch, "E6.3.6.0", {"center": v(3, 6) * mm, "radius": 0.15 * mm});
            skCircle(sketch, "E6.3.7.0", {"center": v(3, 7) * mm, "radius": 0.15 * mm});
            skCircle(sketch, "E6.3.8.0", {"center": v(3, 8) * mm, "radius": 0.15 * mm});
            skCircle(sketch, "E6.3.9.0", {"center": v(3, 9) * mm, "radius": 0.15 * mm});
            skCircle(sketch, "E6.4.0.0", {"center": v(4, 0) * mm, "radius": 0.15 * mm});
            skCircle(sketch, "E6.4.1.0", {"center": v(4, 1) * mm, "radius": 0.15 * mm});
            skCircle(sketch, "E6.4.2.0", {"center": v(4, 2) * mm, "radius": 0.15 * mm});
            skCircle(sketch, "E6.4.3.0", {"center": v(4, 3) * mm, "radius": 0.15 * mm});
            skCircle(sketch, "E6.4.4.0", {"center": v(4, 4) * mm, "radius": 0.15 * mm});
            skCircle(sketch, "E6.4.5.0", {"center": v(4, 5) * mm, "radius": 0.15 * mm});
            skCircle(sketch, "E6.4.6.0", {"center": v(4, 6) * mm, "radius": 0.15 * mm});
            skCircle(sketch, "E6.4.7.0", {"center": v(4, 7) * mm, "radius": 0.15 * mm});
            skCircle(sketch, "E6.4.8.0", {"center": v(4, 8) * mm, "radius": 0.15 * mm});
            skCircle(sketch, "E6.4.9.0", {"center": v(4, 9) * mm, "radius": 0.15 * mm});
            skCircle(sketch, "E6.5.0.0", {"center": v(5, 0) * mm, "radius": 0.15 * mm});
            skCircle(sketch, "E6.5.1.0", {"center": v(5, 1) * mm, "radius": 0.15 * mm});
            skCircle(sketch, "E6.5.2.0", {"center": v(5, 2) * mm, "radius": 0.15 * mm});
            skCircle(sketch, "E6.5.3.0", {"center": v(5, 3) * mm, "radius": 0.15 * mm});
            skCircle(sketch, "E6.5.4.0", {"center": v(5, 4) * mm, "radius": 0.15 * mm});
            skCircle(sketch, "E6.5.5.0", {"center": v(5, 5) * mm, "radius": 0.15 * mm});
            skCircle(sketch, "E6.5.6.0", {"center": v(5, 6) * mm, "radius": 0.15 * mm});
            skCircle(sketch, "E6.5.7.0", {"center": v(5, 7) * mm, "radius": 0.15 * mm});
            skCircle(sketch, "E6.5.8.0", {"center": v(5, 8) * mm, "radius": 0.15 * mm});
            skCircle(sketch, "E6.5.9.0", {"center": v(5, 9) * mm, "radius": 0.15 * mm});
            skCircle(sketch, "E6.6.0.0", {"center": v(6, 0) * mm, "radius": 0.15 * mm});
            skCircle(sketch, "E6.6.1.0", {"center": v(6, 1) * mm, "radius": 0.15 * mm});
            skCircle(sketch, "E6.6.2.0", {"center": v(6, 2) * mm, "radius": 0.15 * mm});
            skCircle(sketch, "E6.6.3.0", {"center": v(6, 3) * mm, "radius": 0.15 * mm});
            skCircle(sketch, "E6.6.4.0", {"center": v(6, 4) * mm, "radius": 0.15 * mm});
            skCircle(sketch, "E6.6.5.0", {"center": v(6, 5) * mm, "radius": 0.15 * mm});
            skCircle(sketch, "E6.6.6.0", {"center": v(6, 6) * mm, "radius": 0.15 * mm});
            skCircle(sketch, "E6.6.7.0", {"center": v(6, 7) * mm, "radius": 0.15 * mm});
            skCircle(sketch, "E6.6.8.0", {"center": v(6, 8) * mm, "radius": 0.15 * mm});
            skCircle(sketch, "E6.6.9.0", {"center": v(6, 9) * mm, "radius": 0.15 * mm});
            skCircle(sketch, "E6.7.0.0", {"center": v(7, 0) * mm, "radius": 0.15 * mm});
            skCircle(sketch, "E6.7.1.0", {"center": v(7, 1) * mm, "radius": 0.15 * mm});
            skCircle(sketch, "E6.7.2.0", {"center": v(7, 2) * mm, "radius": 0.15 * mm});
            skCircle(sketch, "E6.7.3.0", {"center": v(7, 3) * mm, "radius": 0.15 * mm});
            skCircle(sketch, "E6.7.4.0", {"center": v(7, 4) * mm, "radius": 0.15 * mm});
            skCircle(sketch, "E6.7.5.0", {"center": v(7, 5) * mm, "radius": 0.15 * mm});
            skCircle(sketch, "E6.7.6.0", {"center": v(7, 6) * mm, "radius": 0.15 * mm});
            skCircle(sketch, "E6.7.7.0", {"center": v(7, 7) * mm, "radius": 0.15 * mm});
            skCircle(sketch, "E6.7.8.0", {"center": v(7, 8) * mm, "radius": 0.15 * mm});
            skCircle(sketch, "E6.7.9.0", {"center": v(7, 9) * mm, "radius": 0.15 * mm});
            skCircle(sketch, "E6.8.0.0", {"center": v(8, 0) * mm, "radius": 0.15 * mm});
            skCircle(sketch, "E6.8.1.0", {"center": v(8, 1) * mm, "radius": 0.15 * mm});
            skCircle(sketch, "E6.8.2.0", {"center": v(8, 2) * mm, "radius": 0.15 * mm});
            skCircle(sketch, "E6.8.3.0", {"center": v(8, 3) * mm, "radius": 0.15 * mm});
            skCircle(sketch, "E6.8.4.0", {"center": v(8, 4) * mm, "radius": 0.15 * mm});
            skCircle(sketch, "E6.8.5.0", {"center": v(8, 5) * mm, "radius": 0.15 * mm});
            skCircle(sketch, "E6.8.6.0", {"center": v(8, 6) * mm, "radius": 0.15 * mm});
            skCircle(sketch, "E6.8.7.0", {"center": v(8, 7) * mm, "radius": 0.15 * mm});
            skCircle(sketch, "E6.8.8.0", {"center": v(8, 8) * mm, "radius": 0.15 * mm});
            skCircle(sketch, "E6.8.9.0", {"center": v(8, 9) * mm, "radius": 0.15 * mm});
            skCircle(sketch, "E6.9.0.0", {"center": v(9, 0) * mm, "radius": 0.15 * mm});
            skCircle(sketch, "E6.9.1.0", {"center": v(9, 1) * mm, "radius": 0.15 * mm});
            skCircle(sketch, "E6.9.2.0", {"center": v(9, 2) * mm, "radius": 0.15 * mm});
            skCircle(sketch, "E6.9.3.0", {"center": v(9, 3) * mm, "radius": 0.15 * mm});
            skCircle(sketch, "E6.9.4.0", {"center": v(9, 4) * mm, "radius": 0.15 * mm});
            skCircle(sketch, "E6.9.5.0", {"center": v(9, 5) * mm, "radius": 0.15 * mm});
            skCircle(sketch, "E6.9.6.0", {"center": v(9, 6) * mm, "radius": 0.15 * mm});
            skCircle(sketch, "E6.9.7.0", {"center": v(9, 7) * mm, "radius": 0.15 * mm});
            skCircle(sketch, "E6.9.8.0", {"center": v(9, 8) * mm, "radius": 0.15 * mm});
            skCircle(sketch, "E6.9.9.0", {"center": v(9, 9) * mm, "radius": 0.15 * mm});
            skLineSegment(sketch, "E6.direction1", {"start": v(0, 0) * mm, "end": v(1, 0) * mm, "construction": true});
            skLineSegment(sketch, "E6.direction2", {"start": v(0, 0) * mm, "end": v(0, 1) * mm, "construction": true});
            skLineSegment(sketch, "E7.direction1", {"start": v(9, 9) * mm, "end": v(8, 9) * mm, "construction": true});
            skLineSegment(sketch, "E7.direction2", {"start": v(9, 9) * mm, "end": v(9, 8) * mm, "construction": true});
            skCircle(sketch, "E8.0.10.0", {"center": v(9, 10) * mm, "radius": 0.15 * mm});
            skCircle(sketch, "E8.0.11.0", {"center": v(9, 11) * mm, "radius": 0.15 * mm});
            skCircle(sketch, "E8.0.12.0", {"center": v(9, 12) * mm, "radius": 0.15 * mm});
            skCircle(sketch, "E8.0.13.0", {"center": v(9, 13) * mm, "radius": 0.15 * mm});
            skCircle(sketch, "E8.0.14.0", {"center": v(9, 14) * mm, "radius": 0.15 * mm});
            skCircle(sketch, "E8.0.15.0", {"center": v(9, 15) * mm, "radius": 0.15 * mm});
            skCircle(sketch, "E8.0.16.0", {"center": v(9, 16) * mm, "radius": 0.15 * mm});
            skCircle(sketch, "E8.0.17.0", {"center": v(9, 17) * mm, "radius": 0.15 * mm});
            skCircle(sketch, "E8.0.18.0", {"center": v(9, 18) * mm, "radius": 0.15 * mm});
            skCircle(sketch, "E8.0.19.0", {"center": v(9, 19) * mm, "radius": 0.15 * mm});
            skCircle(sketch, "E8.0.20.0", {"center": v(9, 20) * mm, "radius": 0.15 * mm});
            skCircle(sketch, "E8.0.21.0", {"center": v(9, 21) * mm, "radius": 0.15 * mm});
            skCircle(sketch, "E8.0.22.0", {"center": v(9, 22) * mm, "radius": 0.15 * mm});
            skCircle(sketch, "E8.0.23.0", {"center": v(9, 23) * mm, "radius": 0.15 * mm});
            skCircle(sketch, "E8.0.24.0", {"center": v(9, 24) * mm, "radius": 0.15 * mm});
            skCircle(sketch, "E8.0.25.0", {"center": v(9, 25) * mm, "radius": 0.15 * mm});
            skCircle(sketch, "E8.0.26.0", {"center": v(9, 26) * mm, "radius": 0.15 * mm});
            skCircle(sketch, "E8.0.27.0", {"center": v(9, 27) * mm, "radius": 0.15 * mm});
            skCircle(sketch, "E8.0.28.0", {"center": v(9, 28) * mm, "radius": 0.15 * mm});
            skCircle(sketch, "E8.0.29.0", {"center": v(9, 29) * mm, "radius": 0.15 * mm});
            skCircle(sketch, "E8.0.30.0", {"center": v(9, 30) * mm, "radius": 0.15 * mm});
            skCircle(sketch, "E8.0.31.0", {"center": v(9, 31) * mm, "radius": 0.15 * mm});
            skCircle(sketch, "E8.0.32.0", {"center": v(9, 32) * mm, "radius": 0.15 * mm});
            skCircle(sketch, "E8.0.33.0", {"center": v(9, 33) * mm, "radius": 0.15 * mm});
            skCircle(sketch, "E8.0.34.0", {"center": v(9, 34) * mm, "radius": 0.15 * mm});
            skCircle(sketch, "E8.0.35.0", {"center": v(9, 35) * mm, "radius": 0.15 * mm});
            skCircle(sketch, "E8.0.36.0", {"center": v(9, 36) * mm, "radius": 0.15 * mm});
            skCircle(sketch, "E8.0.37.0", {"center": v(9, 37) * mm, "radius": 0.15 * mm});
            skCircle(sketch, "E8.0.38.0", {"center": v(9, 38) * mm, "radius": 0.15 * mm});
            skCircle(sketch, "E8.0.39.0", {"center": v(9, 39) * mm, "radius": 0.15 * mm});
            skCircle(sketch, "E8.0.40.0", {"center": v(9, 40) * mm, "radius": 0.15 * mm});
            skCircle(sketch, "E8.0.41.0", {"center": v(9, 41) * mm, "radius": 0.15 * mm});
            skCircle(sketch, "E8.0.42.0", {"center": v(9, 42) * mm, "radius": 0.15 * mm});
            skCircle(sketch, "E8.0.43.0", {"center": v(9, 43) * mm, "radius": 0.15 * mm});
            skCircle(sketch, "E8.0.44.0", {"center": v(9, 44) * mm, "radius": 0.15 * mm});
            skCircle(sketch, "E8.1.10.0", {"center": v(8, 10) * mm, "radius": 0.15 * mm});
            skCircle(sketch, "E8.1.11.0", {"center": v(8, 11) * mm, "radius": 0.15 * mm});
            skCircle(sketch, "E8.1.12.0", {"center": v(8, 12) * mm, "radius": 0.15 * mm});
            skCircle(sketch, "E8.1.13.0", {"center": v(8, 13) * mm, "radius": 0.15 * mm});
            skCircle(sketch, "E8.1.14.0", {"center": v(8, 14) * mm, "radius": 0.15 * mm});
            skCircle(sketch, "E8.1.15.0", {"center": v(8, 15) * mm, "radius": 0.15 * mm});
            skCircle(sketch, "E8.1.16.0", {"center": v(8, 16) * mm, "radius": 0.15 * mm});
            skCircle(sketch, "E8.1.17.0", {"center": v(8, 17) * mm, "radius": 0.15 * mm});
            skCircle(sketch, "E8.1.18.0", {"center": v(8, 18) * mm, "radius": 0.15 * mm});
            skCircle(sketch, "E8.1.19.0", {"center": v(8, 19) * mm, "radius": 0.15 * mm});
            skCircle(sketch, "E8.1.20.0", {"center": v(8, 20) * mm, "radius": 0.15 * mm});
            skCircle(sketch, "E8.1.21.0", {"center": v(8, 21) * mm, "radius": 0.15 * mm});
            skCircle(sketch, "E8.1.22.0", {"center": v(8, 22) * mm, "radius": 0.15 * mm});
            skCircle(sketch, "E8.1.23.0", {"center": v(8, 23) * mm, "radius": 0.15 * mm});
            skCircle(sketch, "E8.1.24.0", {"center": v(8, 24) * mm, "radius": 0.15 * mm});
            skCircle(sketch, "E8.1.25.0", {"center": v(8, 25) * mm, "radius": 0.15 * mm});
            skCircle(sketch, "E8.1.26.0", {"center": v(8, 26) * mm, "radius": 0.15 * mm});
            skCircle(sketch, "E8.1.27.0", {"center": v(8, 27) * mm, "radius": 0.15 * mm});
            skCircle(sketch, "E8.1.28.0", {"center": v(8, 28) * mm, "radius": 0.15 * mm});
            skCircle(sketch, "E8.1.29.0", {"center": v(8, 29) * mm, "radius": 0.15 * mm});
            skCircle(sketch, "E8.1.30.0", {"center": v(8, 30) * mm, "radius": 0.15 * mm});
            skCircle(sketch, "E8.1.31.0", {"center": v(8, 31) * mm, "radius": 0.15 * mm});
            skCircle(sketch, "E8.1.32.0", {"center": v(8, 32) * mm, "radius": 0.15 * mm});
            skCircle(sketch, "E8.1.33.0", {"center": v(8, 33) * mm, "radius": 0.15 * mm});
            skCircle(sketch, "E8.1.34.0", {"center": v(8, 34) * mm, "radius": 0.15 * mm});
            skCircle(sketch, "E8.1.35.0", {"center": v(8, 35) * mm, "radius": 0.15 * mm});
            skCircle(sketch, "E8.1.36.0", {"center": v(8, 36) * mm, "radius": 0.15 * mm});
            skCircle(sketch, "E8.1.37.0", {"center": v(8, 37) * mm, "radius": 0.15 * mm});
            skCircle(sketch, "E8.1.38.0", {"center": v(8, 38) * mm, "radius": 0.15 * mm});
            skCircle(sketch, "E8.1.39.0", {"center": v(8, 39) * mm, "radius": 0.15 * mm});
            skCircle(sketch, "E8.1.40.0", {"center": v(8, 40) * mm, "radius": 0.15 * mm});
            skCircle(sketch, "E8.1.41.0", {"center": v(8, 41) * mm, "radius": 0.15 * mm});
            skCircle(sketch, "E8.1.42.0", {"center": v(8, 42) * mm, "radius": 0.15 * mm});
            skCircle(sketch, "E8.1.43.0", {"center": v(8, 43) * mm, "radius": 0.15 * mm});
            skCircle(sketch, "E8.1.44.0", {"center": v(8, 44) * mm, "radius": 0.15 * mm});
            skCircle(sketch, "E8.2.10.0", {"center": v(7, 10) * mm, "radius": 0.15 * mm});
            skCircle(sketch, "E8.2.11.0", {"center": v(7, 11) * mm, "radius": 0.15 * mm});
            skCircle(sketch, "E8.2.12.0", {"center": v(7, 12) * mm, "radius": 0.15 * mm});
            skCircle(sketch, "E8.2.13.0", {"center": v(7, 13) * mm, "radius": 0.15 * mm});
            skCircle(sketch, "E8.2.14.0", {"center": v(7, 14) * mm, "radius": 0.15 * mm});
            skCircle(sketch, "E8.2.15.0", {"center": v(7, 15) * mm, "radius": 0.15 * mm});
            skCircle(sketch, "E8.2.16.0", {"center": v(7, 16) * mm, "radius": 0.15 * mm});
            skCircle(sketch, "E8.2.17.0", {"center": v(7, 17) * mm, "radius": 0.15 * mm});
            skCircle(sketch, "E8.2.18.0", {"center": v(7, 18) * mm, "radius": 0.15 * mm});
            skCircle(sketch, "E8.2.19.0", {"center": v(7, 19) * mm, "radius": 0.15 * mm});
            skCircle(sketch, "E8.2.20.0", {"center": v(7, 20) * mm, "radius": 0.15 * mm});
            skCircle(sketch, "E8.2.21.0", {"center": v(7, 21) * mm, "radius": 0.15 * mm});
            skCircle(sketch, "E8.2.22.0", {"center": v(7, 22) * mm, "radius": 0.15 * mm});
            skCircle(sketch, "E8.2.23.0", {"center": v(7, 23) * mm, "radius": 0.15 * mm});
            skCircle(sketch, "E8.2.24.0", {"center": v(7, 24) * mm, "radius": 0.15 * mm});
            skCircle(sketch, "E8.2.25.0", {"center": v(7, 25) * mm, "radius": 0.15 * mm});
            skCircle(sketch, "E8.2.26.0", {"center": v(7, 26) * mm, "radius": 0.15 * mm});
            skCircle(sketch, "E8.2.27.0", {"center": v(7, 27) * mm, "radius": 0.15 * mm});
            skCircle(sketch, "E8.2.28.0", {"center": v(7, 28) * mm, "radius": 0.15 * mm});
            skCircle(sketch, "E8.2.29.0", {"center": v(7, 29) * mm, "radius": 0.15 * mm});
            skCircle(sketch, "E8.2.30.0", {"center": v(7, 30) * mm, "radius": 0.15 * mm});
            skCircle(sketch, "E8.2.31.0", {"center": v(7, 31) * mm, "radius": 0.15 * mm});
            skCircle(sketch, "E8.2.32.0", {"center": v(7, 32) * mm, "radius": 0.15 * mm});
            skCircle(sketch, "E8.2.33.0", {"center": v(7, 33) * mm, "radius": 0.15 * mm});
            skCircle(sketch, "E8.2.34.0", {"center": v(7, 34) * mm, "radius": 0.15 * mm});
            skCircle(sketch, "E8.2.35.0", {"center": v(7, 35) * mm, "radius": 0.15 * mm});
            skCircle(sketch, "E8.2.36.0", {"center": v(7, 36) * mm, "radius": 0.15 * mm});
            skCircle(sketch, "E8.2.37.0", {"center": v(7, 37) * mm, "radius": 0.15 * mm});
            skCircle(sketch, "E8.2.38.0", {"center": v(7, 38) * mm, "radius": 0.15 * mm});
            skCircle(sketch, "E8.2.39.0", {"center": v(7, 39) * mm, "radius": 0.15 * mm});
            skCircle(sketch, "E8.2.40.0", {"center": v(7, 40) * mm, "radius": 0.15 * mm});
            skCircle(sketch, "E8.2.41.0", {"center": v(7, 41) * mm, "radius": 0.15 * mm});
            skCircle(sketch, "E8.2.42.0", {"center": v(7, 42) * mm, "radius": 0.15 * mm});
            skCircle(sketch, "E8.2.43.0", {"center": v(7, 43) * mm, "radius": 0.15 * mm});
            skCircle(sketch, "E8.2.44.0", {"center": v(7, 44) * mm, "radius": 0.15 * mm});
            skCircle(sketch, "E8.3.10.0", {"center": v(6, 10) * mm, "radius": 0.15 * mm});
            skCircle(sketch, "E8.3.11.0", {"center": v(6, 11) * mm, "radius": 0.15 * mm});
            skCircle(sketch, "E8.3.12.0", {"center": v(6, 12) * mm, "radius": 0.15 * mm});
            skCircle(sketch, "E8.3.13.0", {"center": v(6, 13) * mm, "radius": 0.15 * mm});
            skCircle(sketch, "E8.3.14.0", {"center": v(6, 14) * mm, "radius": 0.15 * mm});
            skCircle(sketch, "E8.3.15.0", {"center": v(6, 15) * mm, "radius": 0.15 * mm});
            skCircle(sketch, "E8.3.16.0", {"center": v(6, 16) * mm, "radius": 0.15 * mm});
            skCircle(sketch, "E8.3.17.0", {"center": v(6, 17) * mm, "radius": 0.15 * mm});
            skCircle(sketch, "E8.3.18.0", {"center": v(6, 18) * mm, "radius": 0.15 * mm});
            skCircle(sketch, "E8.3.19.0", {"center": v(6, 19) * mm, "radius": 0.15 * mm});
            skCircle(sketch, "E8.3.20.0", {"center": v(6, 20) * mm, "radius": 0.15 * mm});
            skCircle(sketch, "E8.3.21.0", {"center": v(6, 21) * mm, "radius": 0.15 * mm});
            skCircle(sketch, "E8.3.22.0", {"center": v(6, 22) * mm, "radius": 0.15 * mm});
            skCircle(sketch, "E8.3.23.0", {"center": v(6, 23) * mm, "radius": 0.15 * mm});
            skCircle(sketch, "E8.3.24.0", {"center": v(6, 24) * mm, "radius": 0.15 * mm});
            skCircle(sketch, "E8.3.25.0", {"center": v(6, 25) * mm, "radius": 0.15 * mm});
            skCircle(sketch, "E8.3.26.0", {"center": v(6, 26) * mm, "radius": 0.15 * mm});
            skCircle(sketch, "E8.3.27.0", {"center": v(6, 27) * mm, "radius": 0.15 * mm});
            skCircle(sketch, "E8.3.28.0", {"center": v(6, 28) * mm, "radius": 0.15 * mm});
            skCircle(sketch, "E8.3.29.0", {"center": v(6, 29) * mm, "radius": 0.15 * mm});
            skCircle(sketch, "E8.3.30.0", {"center": v(6, 30) * mm, "radius": 0.15 * mm});
            skCircle(sketch, "E8.3.31.0", {"center": v(6, 31) * mm, "radius": 0.15 * mm});
            skCircle(sketch, "E8.3.32.0", {"center": v(6, 32) * mm, "radius": 0.15 * mm});
            skCircle(sketch, "E8.3.33.0", {"center": v(6, 33) * mm, "radius": 0.15 * mm});
            skCircle(sketch, "E8.3.34.0", {"center": v(6, 34) * mm, "radius": 0.15 * mm});
            skCircle(sketch, "E8.3.35.0", {"center": v(6, 35) * mm, "radius": 0.15 * mm});
            skCircle(sketch, "E8.3.36.0", {"center": v(6, 36) * mm, "radius": 0.15 * mm});
            skCircle(sketch, "E8.3.37.0", {"center": v(6, 37) * mm, "radius": 0.15 * mm});
            skCircle(sketch, "E8.3.38.0", {"center": v(6, 38) * mm, "radius": 0.15 * mm});
            skCircle(sketch, "E8.3.39.0", {"center": v(6, 39) * mm, "radius": 0.15 * mm});
            skCircle(sketch, "E8.3.40.0", {"center": v(6, 40) * mm, "radius": 0.15 * mm});
            skCircle(sketch, "E8.3.41.0", {"center": v(6, 41) * mm, "radius": 0.15 * mm});
            skCircle(sketch, "E8.3.42.0", {"center": v(6, 42) * mm, "radius": 0.15 * mm});
            skCircle(sketch, "E8.3.43.0", {"center": v(6, 43) * mm, "radius": 0.15 * mm});
            skCircle(sketch, "E8.3.44.0", {"center": v(6, 44) * mm, "radius": 0.15 * mm});
            skCircle(sketch, "E8.4.10.0", {"center": v(5, 10) * mm, "radius": 0.15 * mm});
            skCircle(sketch, "E8.4.11.0", {"center": v(5, 11) * mm, "radius": 0.15 * mm});
            skCircle(sketch, "E8.4.12.0", {"center": v(5, 12) * mm, "radius": 0.15 * mm});
            skCircle(sketch, "E8.4.13.0", {"center": v(5, 13) * mm, "radius": 0.15 * mm});
            skCircle(sketch, "E8.4.14.0", {"center": v(5, 14) * mm, "radius": 0.15 * mm});
            skCircle(sketch, "E8.4.15.0", {"center": v(5, 15) * mm, "radius": 0.15 * mm});
            skCircle(sketch, "E8.4.16.0", {"center": v(5, 16) * mm, "radius": 0.15 * mm});
            skCircle(sketch, "E8.4.17.0", {"center": v(5, 17) * mm, "radius": 0.15 * mm});
            skCircle(sketch, "E8.4.18.0", {"center": v(5, 18) * mm, "radius": 0.15 * mm});
            skCircle(sketch, "E8.4.19.0", {"center": v(5, 19) * mm, "radius": 0.15 * mm});
            skCircle(sketch, "E8.4.20.0", {"center": v(5, 20) * mm, "radius": 0.15 * mm});
            skCircle(sketch, "E8.4.21.0", {"center": v(5, 21) * mm, "radius": 0.15 * mm});
            skCircle(sketch, "E8.4.22.0", {"center": v(5, 22) * mm, "radius": 0.15 * mm});
            skCircle(sketch, "E8.4.23.0", {"center": v(5, 23) * mm, "radius": 0.15 * mm});
            skCircle(sketch, "E8.4.24.0", {"center": v(5, 24) * mm, "radius": 0.15 * mm});
            skCircle(sketch, "E8.4.25.0", {"center": v(5, 25) * mm, "radius": 0.15 * mm});
            skCircle(sketch, "E8.4.26.0", {"center": v(5, 26) * mm, "radius": 0.15 * mm});
            skCircle(sketch, "E8.4.27.0", {"center": v(5, 27) * mm, "radius": 0.15 * mm});
            skCircle(sketch, "E8.4.28.0", {"center": v(5, 28) * mm, "radius": 0.15 * mm});
            skCircle(sketch, "E8.4.29.0", {"center": v(5, 29) * mm, "radius": 0.15 * mm});
            skCircle(sketch, "E8.4.30.0", {"center": v(5, 30) * mm, "radius": 0.15 * mm});
            skCircle(sketch, "E8.4.31.0", {"center": v(5, 31) * mm, "radius": 0.15 * mm});
            skCircle(sketch, "E8.4.32.0", {"center": v(5, 32) * mm, "radius": 0.15 * mm});
            skCircle(sketch, "E8.4.33.0", {"center": v(5, 33) * mm, "radius": 0.15 * mm});
            skCircle(sketch, "E8.4.34.0", {"center": v(5, 34) * mm, "radius": 0.15 * mm});
            skCircle(sketch, "E8.4.35.0", {"center": v(5, 35) * mm, "radius": 0.15 * mm});
            skCircle(sketch, "E8.4.36.0", {"center": v(5, 36) * mm, "radius": 0.15 * mm});
            skCircle(sketch, "E8.4.37.0", {"center": v(5, 37) * mm, "radius": 0.15 * mm});
            skCircle(sketch, "E8.4.38.0", {"center": v(5, 38) * mm, "radius": 0.15 * mm});
            skCircle(sketch, "E8.4.39.0", {"center": v(5, 39) * mm, "radius": 0.15 * mm});
            skCircle(sketch, "E8.4.40.0", {"center": v(5, 40) * mm, "radius": 0.15 * mm});
            skCircle(sketch, "E8.4.41.0", {"center": v(5, 41) * mm, "radius": 0.15 * mm});
            skCircle(sketch, "E8.4.42.0", {"center": v(5, 42) * mm, "radius": 0.15 * mm});
            skCircle(sketch, "E8.4.43.0", {"center": v(5, 43) * mm, "radius": 0.15 * mm});
            skCircle(sketch, "E8.4.44.0", {"center": v(5, 44) * mm, "radius": 0.15 * mm});
            skCircle(sketch, "E8.5.10.0", {"center": v(4, 10) * mm, "radius": 0.15 * mm});
            skCircle(sketch, "E8.5.11.0", {"center": v(4, 11) * mm, "radius": 0.15 * mm});
            skCircle(sketch, "E8.5.12.0", {"center": v(4, 12) * mm, "radius": 0.15 * mm});
            skCircle(sketch, "E8.5.13.0", {"center": v(4, 13) * mm, "radius": 0.15 * mm});
            skCircle(sketch, "E8.5.14.0", {"center": v(4, 14) * mm, "radius": 0.15 * mm});
            skCircle(sketch, "E8.5.15.0", {"center": v(4, 15) * mm, "radius": 0.15 * mm});
            skCircle(sketch, "E8.5.16.0", {"center": v(4, 16) * mm, "radius": 0.15 * mm});
            skCircle(sketch, "E8.5.17.0", {"center": v(4, 17) * mm, "radius": 0.15 * mm});
            skCircle(sketch, "E8.5.18.0", {"center": v(4, 18) * mm, "radius": 0.15 * mm});
            skCircle(sketch, "E8.5.19.0", {"center": v(4, 19) * mm, "radius": 0.15 * mm});
            skCircle(sketch, "E8.5.20.0", {"center": v(4, 20) * mm, "radius": 0.15 * mm});
            skCircle(sketch, "E8.5.21.0", {"center": v(4, 21) * mm, "radius": 0.15 * mm});
            skCircle(sketch, "E8.5.22.0", {"center": v(4, 22) * mm, "radius": 0.15 * mm});
            skCircle(sketch, "E8.5.23.0", {"center": v(4, 23) * mm, "radius": 0.15 * mm});
            skCircle(sketch, "E8.5.24.0", {"center": v(4, 24) * mm, "radius": 0.15 * mm});
            skCircle(sketch, "E8.5.25.0", {"center": v(4, 25) * mm, "radius": 0.15 * mm});
            skCircle(sketch, "E8.5.26.0", {"center": v(4, 26) * mm, "radius": 0.15 * mm});
            skCircle(sketch, "E8.5.27.0", {"center": v(4, 27) * mm, "radius": 0.15 * mm});
            skCircle(sketch, "E8.5.28.0", {"center": v(4, 28) * mm, "radius": 0.15 * mm});
            skCircle(sketch, "E8.5.29.0", {"center": v(4, 29) * mm, "radius": 0.15 * mm});
            skCircle(sketch, "E8.5.30.0", {"center": v(4, 30) * mm, "radius": 0.15 * mm});
            skCircle(sketch, "E8.5.31.0", {"center": v(4, 31) * mm, "radius": 0.15 * mm});
            skCircle(sketch, "E8.5.32.0", {"center": v(4, 32) * mm, "radius": 0.15 * mm});
            skCircle(sketch, "E8.5.33.0", {"center": v(4, 33) * mm, "radius": 0.15 * mm});
            skCircle(sketch, "E8.5.34.0", {"center": v(4, 34) * mm, "radius": 0.15 * mm});
            skCircle(sketch, "E8.5.35.0", {"center": v(4, 35) * mm, "radius": 0.15 * mm});
            skCircle(sketch, "E8.5.36.0", {"center": v(4, 36) * mm, "radius": 0.15 * mm});
            skCircle(sketch, "E8.5.37.0", {"center": v(4, 37) * mm, "radius": 0.15 * mm});
            skCircle(sketch, "E8.5.38.0", {"center": v(4, 38) * mm, "radius": 0.15 * mm});
            skCircle(sketch, "E8.5.39.0", {"center": v(4, 39) * mm, "radius": 0.15 * mm});
            skCircle(sketch, "E8.5.40.0", {"center": v(4, 40) * mm, "radius": 0.15 * mm});
            skCircle(sketch, "E8.5.41.0", {"center": v(4, 41) * mm, "radius": 0.15 * mm});
            skCircle(sketch, "E8.5.42.0", {"center": v(4, 42) * mm, "radius": 0.15 * mm});
            skCircle(sketch, "E8.5.43.0", {"center": v(4, 43) * mm, "radius": 0.15 * mm});
            skCircle(sketch, "E8.5.44.0", {"center": v(4, 44) * mm, "radius": 0.15 * mm});
            skCircle(sketch, "E8.6.10.0", {"center": v(3, 10) * mm, "radius": 0.15 * mm});
            skCircle(sketch, "E8.6.11.0", {"center": v(3, 11) * mm, "radius": 0.15 * mm});
            skCircle(sketch, "E8.6.12.0", {"center": v(3, 12) * mm, "radius": 0.15 * mm});
            skCircle(sketch, "E8.6.13.0", {"center": v(3, 13) * mm, "radius": 0.15 * mm});
            skCircle(sketch, "E8.6.14.0", {"center": v(3, 14) * mm, "radius": 0.15 * mm});
            skCircle(sketch, "E8.6.15.0", {"center": v(3, 15) * mm, "radius": 0.15 * mm});
            skCircle(sketch, "E8.6.16.0", {"center": v(3, 16) * mm, "radius": 0.15 * mm});
            skCircle(sketch, "E8.6.17.0", {"center": v(3, 17) * mm, "radius": 0.15 * mm});
            skCircle(sketch, "E8.6.18.0", {"center": v(3, 18) * mm, "radius": 0.15 * mm});
            skCircle(sketch, "E8.6.19.0", {"center": v(3, 19) * mm, "radius": 0.15 * mm});
            skCircle(sketch, "E8.6.20.0", {"center": v(3, 20) * mm, "radius": 0.15 * mm});
            skCircle(sketch, "E8.6.21.0", {"center": v(3, 21) * mm, "radius": 0.15 * mm});
            skCircle(sketch, "E8.6.22.0", {"center": v(3, 22) * mm, "radius": 0.15 * mm});
            skCircle(sketch, "E8.6.23.0", {"center": v(3, 23) * mm, "radius": 0.15 * mm});
            skCircle(sketch, "E8.6.24.0", {"center": v(3, 24) * mm, "radius": 0.15 * mm});
            skCircle(sketch, "E8.6.25.0", {"center": v(3, 25) * mm, "radius": 0.15 * mm});
            skCircle(sketch, "E8.6.26.0", {"center": v(3, 26) * mm, "radius": 0.15 * mm});
            skCircle(sketch, "E8.6.27.0", {"center": v(3, 27) * mm, "radius": 0.15 * mm});
            skCircle(sketch, "E8.6.28.0", {"center": v(3, 28) * mm, "radius": 0.15 * mm});
            skCircle(sketch, "E8.6.29.0", {"center": v(3, 29) * mm, "radius": 0.15 * mm});
            skCircle(sketch, "E8.6.30.0", {"center": v(3, 30) * mm, "radius": 0.15 * mm});
            skCircle(sketch, "E8.6.31.0", {"center": v(3, 31) * mm, "radius": 0.15 * mm});
            skCircle(sketch, "E8.6.32.0", {"center": v(3, 32) * mm, "radius": 0.15 * mm});
            skCircle(sketch, "E8.6.33.0", {"center": v(3, 33) * mm, "radius": 0.15 * mm});
            skCircle(sketch, "E8.6.34.0", {"center": v(3, 34) * mm, "radius": 0.15 * mm});
            skCircle(sketch, "E8.6.35.0", {"center": v(3, 35) * mm, "radius": 0.15 * mm});
            skCircle(sketch, "E8.6.36.0", {"center": v(3, 36) * mm, "radius": 0.15 * mm});
            skCircle(sketch, "E8.6.37.0", {"center": v(3, 37) * mm, "radius": 0.15 * mm});
            skCircle(sketch, "E8.6.38.0", {"center": v(3, 38) * mm, "radius": 0.15 * mm});
            skCircle(sketch, "E8.6.39.0", {"center": v(3, 39) * mm, "radius": 0.15 * mm});
            skCircle(sketch, "E8.6.40.0", {"center": v(3, 40) * mm, "radius": 0.15 * mm});
            skCircle(sketch, "E8.6.41.0", {"center": v(3, 41) * mm, "radius": 0.15 * mm});
            skCircle(sketch, "E8.6.42.0", {"center": v(3, 42) * mm, "radius": 0.15 * mm});
            skCircle(sketch, "E8.6.43.0", {"center": v(3, 43) * mm, "radius": 0.15 * mm});
            skCircle(sketch, "E8.6.44.0", {"center": v(3, 44) * mm, "radius": 0.15 * mm});
            skCircle(sketch, "E8.7.10.0", {"center": v(2, 10) * mm, "radius": 0.15 * mm});
            skCircle(sketch, "E8.7.11.0", {"center": v(2, 11) * mm, "radius": 0.15 * mm});
            skCircle(sketch, "E8.7.12.0", {"center": v(2, 12) * mm, "radius": 0.15 * mm});
            skCircle(sketch, "E8.7.13.0", {"center": v(2, 13) * mm, "radius": 0.15 * mm});
            skCircle(sketch, "E8.7.14.0", {"center": v(2, 14) * mm, "radius": 0.15 * mm});
            skCircle(sketch, "E8.7.15.0", {"center": v(2, 15) * mm, "radius": 0.15 * mm});
            skCircle(sketch, "E8.7.16.0", {"center": v(2, 16) * mm, "radius": 0.15 * mm});
            skCircle(sketch, "E8.7.17.0", {"center": v(2, 17) * mm, "radius": 0.15 * mm});
            skCircle(sketch, "E8.7.18.0", {"center": v(2, 18) * mm, "radius": 0.15 * mm});
            skCircle(sketch, "E8.7.19.0", {"center": v(2, 19) * mm, "radius": 0.15 * mm});
            skCircle(sketch, "E8.7.20.0", {"center": v(2, 20) * mm, "radius": 0.15 * mm});
            skCircle(sketch, "E8.7.21.0", {"center": v(2, 21) * mm, "radius": 0.15 * mm});
            skCircle(sketch, "E8.7.22.0", {"center": v(2, 22) * mm, "radius": 0.15 * mm});
            skCircle(sketch, "E8.7.23.0", {"center": v(2, 23) * mm, "radius": 0.15 * mm});
            skCircle(sketch, "E8.7.24.0", {"center": v(2, 24) * mm, "radius": 0.15 * mm});
            skCircle(sketch, "E8.7.25.0", {"center": v(2, 25) * mm, "radius": 0.15 * mm});
            skCircle(sketch, "E8.7.26.0", {"center": v(2, 26) * mm, "radius": 0.15 * mm});
            skCircle(sketch, "E8.7.27.0", {"center": v(2, 27) * mm, "radius": 0.15 * mm});
            skCircle(sketch, "E8.7.28.0", {"center": v(2, 28) * mm, "radius": 0.15 * mm});
            skCircle(sketch, "E8.7.29.0", {"center": v(2, 29) * mm, "radius": 0.15 * mm});
            skCircle(sketch, "E8.7.30.0", {"center": v(2, 30) * mm, "radius": 0.15 * mm});
            skCircle(sketch, "E8.7.31.0", {"center": v(2, 31) * mm, "radius": 0.15 * mm});
            skCircle(sketch, "E8.7.32.0", {"center": v(2, 32) * mm, "radius": 0.15 * mm});
            skCircle(sketch, "E8.7.33.0", {"center": v(2, 33) * mm, "radius": 0.15 * mm});
            skCircle(sketch, "E8.7.34.0", {"center": v(2, 34) * mm, "radius": 0.15 * mm});
            skCircle(sketch, "E8.7.35.0", {"center": v(2, 35) * mm, "radius": 0.15 * mm});
            skCircle(sketch, "E8.7.36.0", {"center": v(2, 36) * mm, "radius": 0.15 * mm});
            skCircle(sketch, "E8.7.37.0", {"center": v(2, 37) * mm, "radius": 0.15 * mm});
            skCircle(sketch, "E8.7.38.0", {"center": v(2, 38) * mm, "radius": 0.15 * mm});
            skCircle(sketch, "E8.7.39.0", {"center": v(2, 39) * mm, "radius": 0.15 * mm});
            skCircle(sketch, "E8.7.40.0", {"center": v(2, 40) * mm, "radius": 0.15 * mm});
            skCircle(sketch, "E8.7.41.0", {"center": v(2, 41) * mm, "radius": 0.15 * mm});
            skCircle(sketch, "E8.7.42.0", {"center": v(2, 42) * mm, "radius": 0.15 * mm});
            skCircle(sketch, "E8.7.43.0", {"center": v(2, 43) * mm, "radius": 0.15 * mm});
            skCircle(sketch, "E8.7.44.0", {"center": v(2, 44) * mm, "radius": 0.15 * mm});
            skCircle(sketch, "E8.8.10.0", {"center": v(1, 10) * mm, "radius": 0.15 * mm});
            skCircle(sketch, "E8.8.11.0", {"center": v(1, 11) * mm, "radius": 0.15 * mm});
            skCircle(sketch, "E8.8.12.0", {"center": v(1, 12) * mm, "radius": 0.15 * mm});
            skCircle(sketch, "E8.8.13.0", {"center": v(1, 13) * mm, "radius": 0.15 * mm});
            skCircle(sketch, "E8.8.14.0", {"center": v(1, 14) * mm, "radius": 0.15 * mm});
            skCircle(sketch, "E8.8.15.0", {"center": v(1, 15) * mm, "radius": 0.15 * mm});
            skCircle(sketch, "E8.8.16.0", {"center": v(1, 16) * mm, "radius": 0.15 * mm});
            skCircle(sketch, "E8.8.17.0", {"center": v(1, 17) * mm, "radius": 0.15 * mm});
            skCircle(sketch, "E8.8.18.0", {"center": v(1, 18) * mm, "radius": 0.15 * mm});
            skCircle(sketch, "E8.8.19.0", {"center": v(1, 19) * mm, "radius": 0.15 * mm});
            skCircle(sketch, "E8.8.20.0", {"center": v(1, 20) * mm, "radius": 0.15 * mm});
            skCircle(sketch, "E8.8.21.0", {"center": v(1, 21) * mm, "radius": 0.15 * mm});
            skCircle(sketch, "E8.8.22.0", {"center": v(1, 22) * mm, "radius": 0.15 * mm});
            skCircle(sketch, "E8.8.23.0", {"center": v(1, 23) * mm, "radius": 0.15 * mm});
            skCircle(sketch, "E8.8.24.0", {"center": v(1, 24) * mm, "radius": 0.15 * mm});
            skCircle(sketch, "E8.8.25.0", {"center": v(1, 25) * mm, "radius": 0.15 * mm});
            skCircle(sketch, "E8.8.26.0", {"center": v(1, 26) * mm, "radius": 0.15 * mm});
            skCircle(sketch, "E8.8.27.0", {"center": v(1, 27) * mm, "radius": 0.15 * mm});
            skCircle(sketch, "E8.8.28.0", {"center": v(1, 28) * mm, "radius": 0.15 * mm});
            skCircle(sketch, "E8.8.29.0", {"center": v(1, 29) * mm, "radius": 0.15 * mm});
            skCircle(sketch, "E8.8.30.0", {"center": v(1, 30) * mm, "radius": 0.15 * mm});
            skCircle(sketch, "E8.8.31.0", {"center": v(1, 31) * mm, "radius": 0.15 * mm});
            skCircle(sketch, "E8.8.32.0", {"center": v(1, 32) * mm, "radius": 0.15 * mm});
            skCircle(sketch, "E8.8.33.0", {"center": v(1, 33) * mm, "radius": 0.15 * mm});
            skCircle(sketch, "E8.8.34.0", {"center": v(1, 34) * mm, "radius": 0.15 * mm});
            skCircle(sketch, "E8.8.35.0", {"center": v(1, 35) * mm, "radius": 0.15 * mm});
            skCircle(sketch, "E8.8.36.0", {"center": v(1, 36) * mm, "radius": 0.15 * mm});
            skCircle(sketch, "E8.8.37.0", {"center": v(1, 37) * mm, "radius": 0.15 * mm});
            skCircle(sketch, "E8.8.38.0", {"center": v(1, 38) * mm, "radius": 0.15 * mm});
            skCircle(sketch, "E8.8.39.0", {"center": v(1, 39) * mm, "radius": 0.15 * mm});
            skCircle(sketch, "E8.8.40.0", {"center": v(1, 40) * mm, "radius": 0.15 * mm});
            skCircle(sketch, "E8.8.41.0", {"center": v(1, 41) * mm, "radius": 0.15 * mm});
            skCircle(sketch, "E8.8.42.0", {"center": v(1, 42) * mm, "radius": 0.15 * mm});
            skCircle(sketch, "E8.8.43.0", {"center": v(1, 43) * mm, "radius": 0.15 * mm});
            skCircle(sketch, "E8.8.44.0", {"center": v(1, 44) * mm, "radius": 0.15 * mm});
            skCircle(sketch, "E8.9.10.0", {"center": v(0, 10) * mm, "radius": 0.15 * mm});
            skCircle(sketch, "E8.9.11.0", {"center": v(0, 11) * mm, "radius": 0.15 * mm});
            skCircle(sketch, "E8.9.12.0", {"center": v(0, 12) * mm, "radius": 0.15 * mm});
            skCircle(sketch, "E8.9.13.0", {"center": v(0, 13) * mm, "radius": 0.15 * mm});
            skCircle(sketch, "E8.9.14.0", {"center": v(0, 14) * mm, "radius": 0.15 * mm});
            skCircle(sketch, "E8.9.15.0", {"center": v(0, 15) * mm, "radius": 0.15 * mm});
            skCircle(sketch, "E8.9.16.0", {"center": v(0, 16) * mm, "radius": 0.15 * mm});
            skCircle(sketch, "E8.9.17.0", {"center": v(0, 17) * mm, "radius": 0.15 * mm});
            skCircle(sketch, "E8.9.18.0", {"center": v(0, 18) * mm, "radius": 0.15 * mm});
            skCircle(sketch, "E8.9.19.0", {"center": v(0, 19) * mm, "radius": 0.15 * mm});
            skCircle(sketch, "E8.9.20.0", {"center": v(0, 20) * mm, "radius": 0.15 * mm});
            skCircle(sketch, "E8.9.21.0", {"center": v(0, 21) * mm, "radius": 0.15 * mm});
            skCircle(sketch, "E8.9.22.0", {"center": v(0, 22) * mm, "radius": 0.15 * mm});
            skCircle(sketch, "E8.9.23.0", {"center": v(0, 23) * mm, "radius": 0.15 * mm});
            skCircle(sketch, "E8.9.24.0", {"center": v(0, 24) * mm, "radius": 0.15 * mm});
            skCircle(sketch, "E8.9.25.0", {"center": v(0, 25) * mm, "radius": 0.15 * mm});
            skCircle(sketch, "E8.9.26.0", {"center": v(0, 26) * mm, "radius": 0.15 * mm});
            skCircle(sketch, "E8.9.27.0", {"center": v(0, 27) * mm, "radius": 0.15 * mm});
            skCircle(sketch, "E8.9.28.0", {"center": v(0, 28) * mm, "radius": 0.15 * mm});
            skCircle(sketch, "E8.9.29.0", {"center": v(0, 29) * mm, "radius": 0.15 * mm});
            skCircle(sketch, "E8.9.30.0", {"center": v(0, 30) * mm, "radius": 0.15 * mm});
            skCircle(sketch, "E8.9.31.0", {"center": v(0, 31) * mm, "radius": 0.15 * mm});
            skCircle(sketch, "E8.9.32.0", {"center": v(0, 32) * mm, "radius": 0.15 * mm});
            skCircle(sketch, "E8.9.33.0", {"center": v(0, 33) * mm, "radius": 0.15 * mm});
            skCircle(sketch, "E8.9.34.0", {"center": v(0, 34) * mm, "radius": 0.15 * mm});
            skCircle(sketch, "E8.9.35.0", {"center": v(0, 35) * mm, "radius": 0.15 * mm});
            skCircle(sketch, "E8.9.36.0", {"center": v(0, 36) * mm, "radius": 0.15 * mm});
            skCircle(sketch, "E8.9.37.0", {"center": v(0, 37) * mm, "radius": 0.15 * mm});
            skCircle(sketch, "E8.9.38.0", {"center": v(0, 38) * mm, "radius": 0.15 * mm});
            skCircle(sketch, "E8.9.39.0", {"center": v(0, 39) * mm, "radius": 0.15 * mm});
            skCircle(sketch, "E8.9.40.0", {"center": v(0, 40) * mm, "radius": 0.15 * mm});
            skCircle(sketch, "E8.9.41.0", {"center": v(0, 41) * mm, "radius": 0.15 * mm});
            skCircle(sketch, "E8.9.42.0", {"center": v(0, 42) * mm, "radius": 0.15 * mm});
            skCircle(sketch, "E8.9.43.0", {"center": v(0, 43) * mm, "radius": 0.15 * mm});
            skCircle(sketch, "E8.9.44.0", {"center": v(0, 44) * mm, "radius": 0.15 * mm});
            skCircle(sketch, "E8.10.0.0", {"center": v(-1, 0) * mm, "radius": 0.15 * mm});
            skCircle(sketch, "E8.10.1.0", {"center": v(-1, 1) * mm, "radius": 0.15 * mm});
            skCircle(sketch, "E8.10.2.0", {"center": v(-1, 2) * mm, "radius": 0.15 * mm});
            skCircle(sketch, "E8.10.3.0", {"center": v(-1, 3) * mm, "radius": 0.15 * mm});
            skCircle(sketch, "E8.10.4.0", {"center": v(-1, 4) * mm, "radius": 0.15 * mm});
            skCircle(sketch, "E8.10.5.0", {"center": v(-1, 5) * mm, "radius": 0.15 * mm});
            skCircle(sketch, "E8.10.6.0", {"center": v(-1, 6) * mm, "radius": 0.15 * mm});
            skCircle(sketch, "E8.10.7.0", {"center": v(-1, 7) * mm, "radius": 0.15 * mm});
            skCircle(sketch, "E8.10.8.0", {"center": v(-1, 8) * mm, "radius": 0.15 * mm});
            skCircle(sketch, "E8.10.9.0", {"center": v(-1, 9) * mm, "radius": 0.15 * mm});
            skCircle(sketch, "E8.10.10.0", {"center": v(-1, 10) * mm, "radius": 0.15 * mm});
            skCircle(sketch, "E8.10.11.0", {"center": v(-1, 11) * mm, "radius": 0.15 * mm});
            skCircle(sketch, "E8.10.12.0", {"center": v(-1, 12) * mm, "radius": 0.15 * mm});
            skCircle(sketch, "E8.10.13.0", {"center": v(-1, 13) * mm, "radius": 0.15 * mm});
            skCircle(sketch, "E8.10.14.0", {"center": v(-1, 14) * mm, "radius": 0.15 * mm});
            skCircle(sketch, "E8.10.15.0", {"center": v(-1, 15) * mm, "radius": 0.15 * mm});
            skCircle(sketch, "E8.10.16.0", {"center": v(-1, 16) * mm, "radius": 0.15 * mm});
            skCircle(sketch, "E8.10.17.0", {"center": v(-1, 17) * mm, "radius": 0.15 * mm});
            skCircle(sketch, "E8.10.18.0", {"center": v(-1, 18) * mm, "radius": 0.15 * mm});
            skCircle(sketch, "E8.10.19.0", {"center": v(-1, 19) * mm, "radius": 0.15 * mm});
            skCircle(sketch, "E8.10.20.0", {"center": v(-1, 20) * mm, "radius": 0.15 * mm});
            skCircle(sketch, "E8.10.21.0", {"center": v(-1, 21) * mm, "radius": 0.15 * mm});
            skCircle(sketch, "E8.10.22.0", {"center": v(-1, 22) * mm, "radius": 0.15 * mm});
            skCircle(sketch, "E8.10.23.0", {"center": v(-1, 23) * mm, "radius": 0.15 * mm});
            skCircle(sketch, "E8.10.24.0", {"center": v(-1, 24) * mm, "radius": 0.15 * mm});
            skCircle(sketch, "E8.10.25.0", {"center": v(-1, 25) * mm, "radius": 0.15 * mm});
            skCircle(sketch, "E8.10.26.0", {"center": v(-1, 26) * mm, "radius": 0.15 * mm});
            skCircle(sketch, "E8.10.27.0", {"center": v(-1, 27) * mm, "radius": 0.15 * mm});
            skCircle(sketch, "E8.10.28.0", {"center": v(-1, 28) * mm, "radius": 0.15 * mm});
            skCircle(sketch, "E8.10.29.0", {"center": v(-1, 29) * mm, "radius": 0.15 * mm});
            skCircle(sketch, "E8.10.30.0", {"center": v(-1, 30) * mm, "radius": 0.15 * mm});
            skCircle(sketch, "E8.10.31.0", {"center": v(-1, 31) * mm, "radius": 0.15 * mm});
            skCircle(sketch, "E8.10.32.0", {"center": v(-1, 32) * mm, "radius": 0.15 * mm});
            skCircle(sketch, "E8.10.33.0", {"center": v(-1, 33) * mm, "radius": 0.15 * mm});
            skCircle(sketch, "E8.10.34.0", {"center": v(-1, 34) * mm, "radius": 0.15 * mm});
            skCircle(sketch, "E8.10.35.0", {"center": v(-1, 35) * mm, "radius": 0.15 * mm});
            skCircle(sketch, "E8.10.36.0", {"center": v(-1, 36) * mm, "radius": 0.15 * mm});
            skCircle(sketch, "E8.10.37.0", {"center": v(-1, 37) * mm, "radius": 0.15 * mm});
            skCircle(sketch, "E8.10.38.0", {"center": v(-1, 38) * mm, "radius": 0.15 * mm});
            skCircle(sketch, "E8.10.39.0", {"center": v(-1, 39) * mm, "radius": 0.15 * mm});
            skCircle(sketch, "E8.10.40.0", {"center": v(-1, 40) * mm, "radius": 0.15 * mm});
            skCircle(sketch, "E8.10.41.0", {"center": v(-1, 41) * mm, "radius": 0.15 * mm});
            skCircle(sketch, "E8.10.42.0", {"center": v(-1, 42) * mm, "radius": 0.15 * mm});
            skCircle(sketch, "E8.10.43.0", {"center": v(-1, 43) * mm, "radius": 0.15 * mm});
            skCircle(sketch, "E8.10.44.0", {"center": v(-1, 44) * mm, "radius": 0.15 * mm});
            skCircle(sketch, "E8.11.0.0", {"center": v(-2, 0) * mm, "radius": 0.15 * mm});
            skCircle(sketch, "E8.11.1.0", {"center": v(-2, 1) * mm, "radius": 0.15 * mm});
            skCircle(sketch, "E8.11.2.0", {"center": v(-2, 2) * mm, "radius": 0.15 * mm});
            skCircle(sketch, "E8.11.3.0", {"center": v(-2, 3) * mm, "radius": 0.15 * mm});
            skCircle(sketch, "E8.11.4.0", {"center": v(-2, 4) * mm, "radius": 0.15 * mm});
            skCircle(sketch, "E8.11.5.0", {"center": v(-2, 5) * mm, "radius": 0.15 * mm});
            skCircle(sketch, "E8.11.6.0", {"center": v(-2, 6) * mm, "radius": 0.15 * mm});
            skCircle(sketch, "E8.11.7.0", {"center": v(-2, 7) * mm, "radius": 0.15 * mm});
            skCircle(sketch, "E8.11.8.0", {"center": v(-2, 8) * mm, "radius": 0.15 * mm});
            skCircle(sketch, "E8.11.9.0", {"center": v(-2, 9) * mm, "radius": 0.15 * mm});
            skCircle(sketch, "E8.11.10.0", {"center": v(-2, 10) * mm, "radius": 0.15 * mm});
            skCircle(sketch, "E8.11.11.0", {"center": v(-2, 11) * mm, "radius": 0.15 * mm});
            skCircle(sketch, "E8.11.12.0", {"center": v(-2, 12) * mm, "radius": 0.15 * mm});
            skCircle(sketch, "E8.11.13.0", {"center": v(-2, 13) * mm, "radius": 0.15 * mm});
            skCircle(sketch, "E8.11.14.0", {"center": v(-2, 14) * mm, "radius": 0.15 * mm});
            skCircle(sketch, "E8.11.15.0", {"center": v(-2, 15) * mm, "radius": 0.15 * mm});
            skCircle(sketch, "E8.11.16.0", {"center": v(-2, 16) * mm, "radius": 0.15 * mm});
            skCircle(sketch, "E8.11.17.0", {"center": v(-2, 17) * mm, "radius": 0.15 * mm});
            skCircle(sketch, "E8.11.18.0", {"center": v(-2, 18) * mm, "radius": 0.15 * mm});
            skCircle(sketch, "E8.11.19.0", {"center": v(-2, 19) * mm, "radius": 0.15 * mm});
            skCircle(sketch, "E8.11.20.0", {"center": v(-2, 20) * mm, "radius": 0.15 * mm});
            skCircle(sketch, "E8.11.21.0", {"center": v(-2, 21) * mm, "radius": 0.15 * mm});
            skCircle(sketch, "E8.11.22.0", {"center": v(-2, 22) * mm, "radius": 0.15 * mm});
            skCircle(sketch, "E8.11.23.0", {"center": v(-2, 23) * mm, "radius": 0.15 * mm});
            skCircle(sketch, "E8.11.24.0", {"center": v(-2, 24) * mm, "radius": 0.15 * mm});
            skCircle(sketch, "E8.11.25.0", {"center": v(-2, 25) * mm, "radius": 0.15 * mm});
            skCircle(sketch, "E8.11.26.0", {"center": v(-2, 26) * mm, "radius": 0.15 * mm});
            skCircle(sketch, "E8.11.27.0", {"center": v(-2, 27) * mm, "radius": 0.15 * mm});
            skCircle(sketch, "E8.11.28.0", {"center": v(-2, 28) * mm, "radius": 0.15 * mm});
            skCircle(sketch, "E8.11.29.0", {"center": v(-2, 29) * mm, "radius": 0.15 * mm});
            skCircle(sketch, "E8.11.30.0", {"center": v(-2, 30) * mm, "radius": 0.15 * mm});
            skCircle(sketch, "E8.11.31.0", {"center": v(-2, 31) * mm, "radius": 0.15 * mm});
            skCircle(sketch, "E8.11.32.0", {"center": v(-2, 32) * mm, "radius": 0.15 * mm});
            skCircle(sketch, "E8.11.33.0", {"center": v(-2, 33) * mm, "radius": 0.15 * mm});
            skCircle(sketch, "E8.11.34.0", {"center": v(-2, 34) * mm, "radius": 0.15 * mm});
            skCircle(sketch, "E8.11.35.0", {"center": v(-2, 35) * mm, "radius": 0.15 * mm});
            skCircle(sketch, "E8.11.36.0", {"center": v(-2, 36) * mm, "radius": 0.15 * mm});
            skCircle(sketch, "E8.11.37.0", {"center": v(-2, 37) * mm, "radius": 0.15 * mm});
            skCircle(sketch, "E8.11.38.0", {"center": v(-2, 38) * mm, "radius": 0.15 * mm});
            skCircle(sketch, "E8.11.39.0", {"center": v(-2, 39) * mm, "radius": 0.15 * mm});
            skCircle(sketch, "E8.11.40.0", {"center": v(-2, 40) * mm, "radius": 0.15 * mm});
            skCircle(sketch, "E8.11.41.0", {"center": v(-2, 41) * mm, "radius": 0.15 * mm});
            skCircle(sketch, "E8.11.42.0", {"center": v(-2, 42) * mm, "radius": 0.15 * mm});
            skCircle(sketch, "E8.11.43.0", {"center": v(-2, 43) * mm, "radius": 0.15 * mm});
            skCircle(sketch, "E8.11.44.0", {"center": v(-2, 44) * mm, "radius": 0.15 * mm});
            skCircle(sketch, "E8.12.0.0", {"center": v(-3, 0) * mm, "radius": 0.15 * mm});
            skCircle(sketch, "E8.12.1.0", {"center": v(-3, 1) * mm, "radius": 0.15 * mm});
            skCircle(sketch, "E8.12.2.0", {"center": v(-3, 2) * mm, "radius": 0.15 * mm});
            skCircle(sketch, "E8.12.3.0", {"center": v(-3, 3) * mm, "radius": 0.15 * mm});
            skCircle(sketch, "E8.12.4.0", {"center": v(-3, 4) * mm, "radius": 0.15 * mm});
            skCircle(sketch, "E8.12.5.0", {"center": v(-3, 5) * mm, "radius": 0.15 * mm});
            skCircle(sketch, "E8.12.6.0", {"center": v(-3, 6) * mm, "radius": 0.15 * mm});
            skCircle(sketch, "E8.12.7.0", {"center": v(-3, 7) * mm, "radius": 0.15 * mm});
            skCircle(sketch, "E8.12.8.0", {"center": v(-3, 8) * mm, "radius": 0.15 * mm});
            skCircle(sketch, "E8.12.9.0", {"center": v(-3, 9) * mm, "radius": 0.15 * mm});
            skCircle(sketch, "E8.12.10.0", {"center": v(-3, 10) * mm, "radius": 0.15 * mm});
            skCircle(sketch, "E8.12.11.0", {"center": v(-3, 11) * mm, "radius": 0.15 * mm});
            skCircle(sketch, "E8.12.12.0", {"center": v(-3, 12) * mm, "radius": 0.15 * mm});
            skCircle(sketch, "E8.12.13.0", {"center": v(-3, 13) * mm, "radius": 0.15 * mm});
            skCircle(sketch, "E8.12.14.0", {"center": v(-3, 14) * mm, "radius": 0.15 * mm});
            skCircle(sketch, "E8.12.15.0", {"center": v(-3, 15) * mm, "radius": 0.15 * mm});
            skCircle(sketch, "E8.12.16.0", {"center": v(-3, 16) * mm, "radius": 0.15 * mm});
            skCircle(sketch, "E8.12.17.0", {"center": v(-3, 17) * mm, "radius": 0.15 * mm});
            skCircle(sketch, "E8.12.18.0", {"center": v(-3, 18) * mm, "radius": 0.15 * mm});
            skCircle(sketch, "E8.12.19.0", {"center": v(-3, 19) * mm, "radius": 0.15 * mm});
            skCircle(sketch, "E8.12.20.0", {"center": v(-3, 20) * mm, "radius": 0.15 * mm});
            skCircle(sketch, "E8.12.21.0", {"center": v(-3, 21) * mm, "radius": 0.15 * mm});
            skCircle(sketch, "E8.12.22.0", {"center": v(-3, 22) * mm, "radius": 0.15 * mm});
            skCircle(sketch, "E8.12.23.0", {"center": v(-3, 23) * mm, "radius": 0.15 * mm});
            skCircle(sketch, "E8.12.24.0", {"center": v(-3, 24) * mm, "radius": 0.15 * mm});
            skCircle(sketch, "E8.12.25.0", {"center": v(-3, 25) * mm, "radius": 0.15 * mm});
            skCircle(sketch, "E8.12.26.0", {"center": v(-3, 26) * mm, "radius": 0.15 * mm});
            skCircle(sketch, "E8.12.27.0", {"center": v(-3, 27) * mm, "radius": 0.15 * mm});
            skCircle(sketch, "E8.12.28.0", {"center": v(-3, 28) * mm, "radius": 0.15 * mm});
            skCircle(sketch, "E8.12.29.0", {"center": v(-3, 29) * mm, "radius": 0.15 * mm});
            skCircle(sketch, "E8.12.30.0", {"center": v(-3, 30) * mm, "radius": 0.15 * mm});
            skCircle(sketch, "E8.12.31.0", {"center": v(-3, 31) * mm, "radius": 0.15 * mm});
            skCircle(sketch, "E8.12.32.0", {"center": v(-3, 32) * mm, "radius": 0.15 * mm});
            skCircle(sketch, "E8.12.33.0", {"center": v(-3, 33) * mm, "radius": 0.15 * mm});
            skCircle(sketch, "E8.12.34.0", {"center": v(-3, 34) * mm, "radius": 0.15 * mm});
            skCircle(sketch, "E8.12.35.0", {"center": v(-3, 35) * mm, "radius": 0.15 * mm});
            skCircle(sketch, "E8.12.36.0", {"center": v(-3, 36) * mm, "radius": 0.15 * mm});
            skCircle(sketch, "E8.12.37.0", {"center": v(-3, 37) * mm, "radius": 0.15 * mm});
            skCircle(sketch, "E8.12.38.0", {"center": v(-3, 38) * mm, "radius": 0.15 * mm});
            skCircle(sketch, "E8.12.39.0", {"center": v(-3, 39) * mm, "radius": 0.15 * mm});
            skCircle(sketch, "E8.12.40.0", {"center": v(-3, 40) * mm, "radius": 0.15 * mm});
            skCircle(sketch, "E8.12.41.0", {"center": v(-3, 41) * mm, "radius": 0.15 * mm});
            skCircle(sketch, "E8.12.42.0", {"center": v(-3, 42) * mm, "radius": 0.15 * mm});
            skCircle(sketch, "E8.12.43.0", {"center": v(-3, 43) * mm, "radius": 0.15 * mm});
            skCircle(sketch, "E8.12.44.0", {"center": v(-3, 44) * mm, "radius": 0.15 * mm});
            skCircle(sketch, "E8.13.0.0", {"center": v(-4, 0) * mm, "radius": 0.15 * mm});
            skCircle(sketch, "E8.13.1.0", {"center": v(-4, 1) * mm, "radius": 0.15 * mm});
            skCircle(sketch, "E8.13.2.0", {"center": v(-4, 2) * mm, "radius": 0.15 * mm});
            skCircle(sketch, "E8.13.3.0", {"center": v(-4, 3) * mm, "radius": 0.15 * mm});
            skCircle(sketch, "E8.13.4.0", {"center": v(-4, 4) * mm, "radius": 0.15 * mm});
            skCircle(sketch, "E8.13.5.0", {"center": v(-4, 5) * mm, "radius": 0.15 * mm});
            skCircle(sketch, "E8.13.6.0", {"center": v(-4, 6) * mm, "radius": 0.15 * mm});
            skCircle(sketch, "E8.13.7.0", {"center": v(-4, 7) * mm, "radius": 0.15 * mm});
            skCircle(sketch, "E8.13.8.0", {"center": v(-4, 8) * mm, "radius": 0.15 * mm});
            skCircle(sketch, "E8.13.9.0", {"center": v(-4, 9) * mm, "radius": 0.15 * mm});
            skCircle(sketch, "E8.13.10.0", {"center": v(-4, 10) * mm, "radius": 0.15 * mm});
            skCircle(sketch, "E8.13.11.0", {"center": v(-4, 11) * mm, "radius": 0.15 * mm});
            skCircle(sketch, "E8.13.12.0", {"center": v(-4, 12) * mm, "radius": 0.15 * mm});
            skCircle(sketch, "E8.13.13.0", {"center": v(-4, 13) * mm, "radius": 0.15 * mm});
            skCircle(sketch, "E8.13.14.0", {"center": v(-4, 14) * mm, "radius": 0.15 * mm});
            skCircle(sketch, "E8.13.15.0", {"center": v(-4, 15) * mm, "radius": 0.15 * mm});
            skCircle(sketch, "E8.13.16.0", {"center": v(-4, 16) * mm, "radius": 0.15 * mm});
            skCircle(sketch, "E8.13.17.0", {"center": v(-4, 17) * mm, "radius": 0.15 * mm});
            skCircle(sketch, "E8.13.18.0", {"center": v(-4, 18) * mm, "radius": 0.15 * mm});
            skCircle(sketch, "E8.13.19.0", {"center": v(-4, 19) * mm, "radius": 0.15 * mm});
            skCircle(sketch, "E8.13.20.0", {"center": v(-4, 20) * mm, "radius": 0.15 * mm});
            skCircle(sketch, "E8.13.21.0", {"center": v(-4, 21) * mm, "radius": 0.15 * mm});
            skCircle(sketch, "E8.13.22.0", {"center": v(-4, 22) * mm, "radius": 0.15 * mm});
            skCircle(sketch, "E8.13.23.0", {"center": v(-4, 23) * mm, "radius": 0.15 * mm});
            skCircle(sketch, "E8.13.24.0", {"center": v(-4, 24) * mm, "radius": 0.15 * mm});
            skCircle(sketch, "E8.13.25.0", {"center": v(-4, 25) * mm, "radius": 0.15 * mm});
            skCircle(sketch, "E8.13.26.0", {"center": v(-4, 26) * mm, "radius": 0.15 * mm});
            skCircle(sketch, "E8.13.27.0", {"center": v(-4, 27) * mm, "radius": 0.15 * mm});
            skCircle(sketch, "E8.13.28.0", {"center": v(-4, 28) * mm, "radius": 0.15 * mm});
            skCircle(sketch, "E8.13.29.0", {"center": v(-4, 29) * mm, "radius": 0.15 * mm});
            skCircle(sketch, "E8.13.30.0", {"center": v(-4, 30) * mm, "radius": 0.15 * mm});
            skCircle(sketch, "E8.13.31.0", {"center": v(-4, 31) * mm, "radius": 0.15 * mm});
            skCircle(sketch, "E8.13.32.0", {"center": v(-4, 32) * mm, "radius": 0.15 * mm});
            skCircle(sketch, "E8.13.33.0", {"center": v(-4, 33) * mm, "radius": 0.15 * mm});
            skCircle(sketch, "E8.13.34.0", {"center": v(-4, 34) * mm, "radius": 0.15 * mm});
            skCircle(sketch, "E8.13.35.0", {"center": v(-4, 35) * mm, "radius": 0.15 * mm});
            skCircle(sketch, "E8.13.36.0", {"center": v(-4, 36) * mm, "radius": 0.15 * mm});
            skCircle(sketch, "E8.13.37.0", {"center": v(-4, 37) * mm, "radius": 0.15 * mm});
            skCircle(sketch, "E8.13.38.0", {"center": v(-4, 38) * mm, "radius": 0.15 * mm});
            skCircle(sketch, "E8.13.39.0", {"center": v(-4, 39) * mm, "radius": 0.15 * mm});
            skCircle(sketch, "E8.13.40.0", {"center": v(-4, 40) * mm, "radius": 0.15 * mm});
            skCircle(sketch, "E8.13.41.0", {"center": v(-4, 41) * mm, "radius": 0.15 * mm});
            skCircle(sketch, "E8.13.42.0", {"center": v(-4, 42) * mm, "radius": 0.15 * mm});
            skCircle(sketch, "E8.13.43.0", {"center": v(-4, 43) * mm, "radius": 0.15 * mm});
            skCircle(sketch, "E8.13.44.0", {"center": v(-4, 44) * mm, "radius": 0.15 * mm});
            skCircle(sketch, "E8.14.0.0", {"center": v(-5, 0) * mm, "radius": 0.15 * mm});
            skCircle(sketch, "E8.14.1.0", {"center": v(-5, 1) * mm, "radius": 0.15 * mm});
            skCircle(sketch, "E8.14.2.0", {"center": v(-5, 2) * mm, "radius": 0.15 * mm});
            skCircle(sketch, "E8.14.3.0", {"center": v(-5, 3) * mm, "radius": 0.15 * mm});
            skCircle(sketch, "E8.14.4.0", {"center": v(-5, 4) * mm, "radius": 0.15 * mm});
            skCircle(sketch, "E8.14.5.0", {"center": v(-5, 5) * mm, "radius": 0.15 * mm});
            skCircle(sketch, "E8.14.6.0", {"center": v(-5, 6) * mm, "radius": 0.15 * mm});
            skCircle(sketch, "E8.14.7.0", {"center": v(-5, 7) * mm, "radius": 0.15 * mm});
            skCircle(sketch, "E8.14.8.0", {"center": v(-5, 8) * mm, "radius": 0.15 * mm});
            skCircle(sketch, "E8.14.9.0", {"center": v(-5, 9) * mm, "radius": 0.15 * mm});
            skCircle(sketch, "E8.14.10.0", {"center": v(-5, 10) * mm, "radius": 0.15 * mm});
            skCircle(sketch, "E8.14.11.0", {"center": v(-5, 11) * mm, "radius": 0.15 * mm});
            skCircle(sketch, "E8.14.12.0", {"center": v(-5, 12) * mm, "radius": 0.15 * mm});
            skCircle(sketch, "E8.14.13.0", {"center": v(-5, 13) * mm, "radius": 0.15 * mm});
            skCircle(sketch, "E8.14.14.0", {"center": v(-5, 14) * mm, "radius": 0.15 * mm});
            skCircle(sketch, "E8.14.15.0", {"center": v(-5, 15) * mm, "radius": 0.15 * mm});
            skCircle(sketch, "E8.14.16.0", {"center": v(-5, 16) * mm, "radius": 0.15 * mm});
            skCircle(sketch, "E8.14.17.0", {"center": v(-5, 17) * mm, "radius": 0.15 * mm});
            skCircle(sketch, "E8.14.18.0", {"center": v(-5, 18) * mm, "radius": 0.15 * mm});
            skCircle(sketch, "E8.14.19.0", {"center": v(-5, 19) * mm, "radius": 0.15 * mm});
            skCircle(sketch, "E8.14.20.0", {"center": v(-5, 20) * mm, "radius": 0.15 * mm});
            skCircle(sketch, "E8.14.21.0", {"center": v(-5, 21) * mm, "radius": 0.15 * mm});
            skCircle(sketch, "E8.14.22.0", {"center": v(-5, 22) * mm, "radius": 0.15 * mm});
            skCircle(sketch, "E8.14.23.0", {"center": v(-5, 23) * mm, "radius": 0.15 * mm});
            skCircle(sketch, "E8.14.24.0", {"center": v(-5, 24) * mm, "radius": 0.15 * mm});
            skCircle(sketch, "E8.14.25.0", {"center": v(-5, 25) * mm, "radius": 0.15 * mm});
            skCircle(sketch, "E8.14.26.0", {"center": v(-5, 26) * mm, "radius": 0.15 * mm});
            skCircle(sketch, "E8.14.27.0", {"center": v(-5, 27) * mm, "radius": 0.15 * mm});
            skCircle(sketch, "E8.14.28.0", {"center": v(-5, 28) * mm, "radius": 0.15 * mm});
            skCircle(sketch, "E8.14.29.0", {"center": v(-5, 29) * mm, "radius": 0.15 * mm});
            skCircle(sketch, "E8.14.30.0", {"center": v(-5, 30) * mm, "radius": 0.15 * mm});
            skCircle(sketch, "E8.14.31.0", {"center": v(-5, 31) * mm, "radius": 0.15 * mm});
            skCircle(sketch, "E8.14.32.0", {"center": v(-5, 32) * mm, "radius": 0.15 * mm});
            skCircle(sketch, "E8.14.33.0", {"center": v(-5, 33) * mm, "radius": 0.15 * mm});
            skCircle(sketch, "E8.14.34.0", {"center": v(-5, 34) * mm, "radius": 0.15 * mm});
            skCircle(sketch, "E8.14.35.0", {"center": v(-5, 35) * mm, "radius": 0.15 * mm});
            skCircle(sketch, "E8.14.36.0", {"center": v(-5, 36) * mm, "radius": 0.15 * mm});
            skCircle(sketch, "E8.14.37.0", {"center": v(-5, 37) * mm, "radius": 0.15 * mm});
            skCircle(sketch, "E8.14.38.0", {"center": v(-5, 38) * mm, "radius": 0.15 * mm});
            skCircle(sketch, "E8.14.39.0", {"center": v(-5, 39) * mm, "radius": 0.15 * mm});
            skCircle(sketch, "E8.14.40.0", {"center": v(-5, 40) * mm, "radius": 0.15 * mm});
            skCircle(sketch, "E8.14.41.0", {"center": v(-5, 41) * mm, "radius": 0.15 * mm});
            skCircle(sketch, "E8.14.42.0", {"center": v(-5, 42) * mm, "radius": 0.15 * mm});
            skCircle(sketch, "E8.14.43.0", {"center": v(-5, 43) * mm, "radius": 0.15 * mm});
            skCircle(sketch, "E8.14.44.0", {"center": v(-5, 44) * mm, "radius": 0.15 * mm});
            skCircle(sketch, "E8.15.0.0", {"center": v(-6, 0) * mm, "radius": 0.15 * mm});
            skCircle(sketch, "E8.15.1.0", {"center": v(-6, 1) * mm, "radius": 0.15 * mm});
            skCircle(sketch, "E8.15.2.0", {"center": v(-6, 2) * mm, "radius": 0.15 * mm});
            skCircle(sketch, "E8.15.3.0", {"center": v(-6, 3) * mm, "radius": 0.15 * mm});
            skCircle(sketch, "E8.15.4.0", {"center": v(-6, 4) * mm, "radius": 0.15 * mm});
            skCircle(sketch, "E8.15.5.0", {"center": v(-6, 5) * mm, "radius": 0.15 * mm});
            skCircle(sketch, "E8.15.6.0", {"center": v(-6, 6) * mm, "radius": 0.15 * mm});
            skCircle(sketch, "E8.15.7.0", {"center": v(-6, 7) * mm, "radius": 0.15 * mm});
            skCircle(sketch, "E8.15.8.0", {"center": v(-6, 8) * mm, "radius": 0.15 * mm});
            skCircle(sketch, "E8.15.9.0", {"center": v(-6, 9) * mm, "radius": 0.15 * mm});
            skCircle(sketch, "E8.15.10.0", {"center": v(-6, 10) * mm, "radius": 0.15 * mm});
            skCircle(sketch, "E8.15.11.0", {"center": v(-6, 11) * mm, "radius": 0.15 * mm});
            skCircle(sketch, "E8.15.12.0", {"center": v(-6, 12) * mm, "radius": 0.15 * mm});
            skCircle(sketch, "E8.15.13.0", {"center": v(-6, 13) * mm, "radius": 0.15 * mm});
            skCircle(sketch, "E8.15.14.0", {"center": v(-6, 14) * mm, "radius": 0.15 * mm});
            skCircle(sketch, "E8.15.15.0", {"center": v(-6, 15) * mm, "radius": 0.15 * mm});
            skCircle(sketch, "E8.15.16.0", {"center": v(-6, 16) * mm, "radius": 0.15 * mm});
            skCircle(sketch, "E8.15.17.0", {"center": v(-6, 17) * mm, "radius": 0.15 * mm});
            skCircle(sketch, "E8.15.18.0", {"center": v(-6, 18) * mm, "radius": 0.15 * mm});
            skCircle(sketch, "E8.15.19.0", {"center": v(-6, 19) * mm, "radius": 0.15 * mm});
            skCircle(sketch, "E8.15.20.0", {"center": v(-6, 20) * mm, "radius": 0.15 * mm});
            skCircle(sketch, "E8.15.21.0", {"center": v(-6, 21) * mm, "radius": 0.15 * mm});
            skCircle(sketch, "E8.15.22.0", {"center": v(-6, 22) * mm, "radius": 0.15 * mm});
            skCircle(sketch, "E8.15.23.0", {"center": v(-6, 23) * mm, "radius": 0.15 * mm});
            skCircle(sketch, "E8.15.24.0", {"center": v(-6, 24) * mm, "radius": 0.15 * mm});
            skCircle(sketch, "E8.15.25.0", {"center": v(-6, 25) * mm, "radius": 0.15 * mm});
            skCircle(sketch, "E8.15.26.0", {"center": v(-6, 26) * mm, "radius": 0.15 * mm});
            skCircle(sketch, "E8.15.27.0", {"center": v(-6, 27) * mm, "radius": 0.15 * mm});
            skCircle(sketch, "E8.15.28.0", {"center": v(-6, 28) * mm, "radius": 0.15 * mm});
            skCircle(sketch, "E8.15.29.0", {"center": v(-6, 29) * mm, "radius": 0.15 * mm});
            skCircle(sketch, "E8.15.30.0", {"center": v(-6, 30) * mm, "radius": 0.15 * mm});
            skCircle(sketch, "E8.15.31.0", {"center": v(-6, 31) * mm, "radius": 0.15 * mm});
            skCircle(sketch, "E8.15.32.0", {"center": v(-6, 32) * mm, "radius": 0.15 * mm});
            skCircle(sketch, "E8.15.33.0", {"center": v(-6, 33) * mm, "radius": 0.15 * mm});
            skCircle(sketch, "E8.15.34.0", {"center": v(-6, 34) * mm, "radius": 0.15 * mm});
            skCircle(sketch, "E8.15.35.0", {"center": v(-6, 35) * mm, "radius": 0.15 * mm});
            skCircle(sketch, "E8.15.36.0", {"center": v(-6, 36) * mm, "radius": 0.15 * mm});
            skCircle(sketch, "E8.15.37.0", {"center": v(-6, 37) * mm, "radius": 0.15 * mm});
            skCircle(sketch, "E8.15.38.0", {"center": v(-6, 38) * mm, "radius": 0.15 * mm});
            skCircle(sketch, "E8.15.39.0", {"center": v(-6, 39) * mm, "radius": 0.15 * mm});
            skCircle(sketch, "E8.15.40.0", {"center": v(-6, 40) * mm, "radius": 0.15 * mm});
            skCircle(sketch, "E8.15.41.0", {"center": v(-6, 41) * mm, "radius": 0.15 * mm});
            skCircle(sketch, "E8.15.42.0", {"center": v(-6, 42) * mm, "radius": 0.15 * mm});
            skCircle(sketch, "E8.15.43.0", {"center": v(-6, 43) * mm, "radius": 0.15 * mm});
            skCircle(sketch, "E8.15.44.0", {"center": v(-6, 44) * mm, "radius": 0.15 * mm});
            skCircle(sketch, "E8.16.0.0", {"center": v(-7, 0) * mm, "radius": 0.15 * mm});
            skCircle(sketch, "E8.16.1.0", {"center": v(-7, 1) * mm, "radius": 0.15 * mm});
            skCircle(sketch, "E8.16.2.0", {"center": v(-7, 2) * mm, "radius": 0.15 * mm});
            skCircle(sketch, "E8.16.3.0", {"center": v(-7, 3) * mm, "radius": 0.15 * mm});
            skCircle(sketch, "E8.16.4.0", {"center": v(-7, 4) * mm, "radius": 0.15 * mm});
            skCircle(sketch, "E8.16.5.0", {"center": v(-7, 5) * mm, "radius": 0.15 * mm});
            skCircle(sketch, "E8.16.6.0", {"center": v(-7, 6) * mm, "radius": 0.15 * mm});
            skCircle(sketch, "E8.16.7.0", {"center": v(-7, 7) * mm, "radius": 0.15 * mm});
            skCircle(sketch, "E8.16.8.0", {"center": v(-7, 8) * mm, "radius": 0.15 * mm});
            skCircle(sketch, "E8.16.9.0", {"center": v(-7, 9) * mm, "radius": 0.15 * mm});
            skCircle(sketch, "E8.16.10.0", {"center": v(-7, 10) * mm, "radius": 0.15 * mm});
            skCircle(sketch, "E8.16.11.0", {"center": v(-7, 11) * mm, "radius": 0.15 * mm});
            skCircle(sketch, "E8.16.12.0", {"center": v(-7, 12) * mm, "radius": 0.15 * mm});
            skCircle(sketch, "E8.16.13.0", {"center": v(-7, 13) * mm, "radius": 0.15 * mm});
            skCircle(sketch, "E8.16.14.0", {"center": v(-7, 14) * mm, "radius": 0.15 * mm});
            skCircle(sketch, "E8.16.15.0", {"center": v(-7, 15) * mm, "radius": 0.15 * mm});
            skCircle(sketch, "E8.16.16.0", {"center": v(-7, 16) * mm, "radius": 0.15 * mm});
            skCircle(sketch, "E8.16.17.0", {"center": v(-7, 17) * mm, "radius": 0.15 * mm});
            skCircle(sketch, "E8.16.18.0", {"center": v(-7, 18) * mm, "radius": 0.15 * mm});
            skCircle(sketch, "E8.16.19.0", {"center": v(-7, 19) * mm, "radius": 0.15 * mm});
            skCircle(sketch, "E8.16.20.0", {"center": v(-7, 20) * mm, "radius": 0.15 * mm});
            skCircle(sketch, "E8.16.21.0", {"center": v(-7, 21) * mm, "radius": 0.15 * mm});
            skCircle(sketch, "E8.16.22.0", {"center": v(-7, 22) * mm, "radius": 0.15 * mm});
            skCircle(sketch, "E8.16.23.0", {"center": v(-7, 23) * mm, "radius": 0.15 * mm});
            skCircle(sketch, "E8.16.24.0", {"center": v(-7, 24) * mm, "radius": 0.15 * mm});
            skCircle(sketch, "E8.16.25.0", {"center": v(-7, 25) * mm, "radius": 0.15 * mm});
            skCircle(sketch, "E8.16.26.0", {"center": v(-7, 26) * mm, "radius": 0.15 * mm});
            skCircle(sketch, "E8.16.27.0", {"center": v(-7, 27) * mm, "radius": 0.15 * mm});
            skCircle(sketch, "E8.16.28.0", {"center": v(-7, 28) * mm, "radius": 0.15 * mm});
            skCircle(sketch, "E8.16.29.0", {"center": v(-7, 29) * mm, "radius": 0.15 * mm});
            skCircle(sketch, "E8.16.30.0", {"center": v(-7, 30) * mm, "radius": 0.15 * mm});
            skCircle(sketch, "E8.16.31.0", {"center": v(-7, 31) * mm, "radius": 0.15 * mm});
            skCircle(sketch, "E8.16.32.0", {"center": v(-7, 32) * mm, "radius": 0.15 * mm});
            skCircle(sketch, "E8.16.33.0", {"center": v(-7, 33) * mm, "radius": 0.15 * mm});
            skCircle(sketch, "E8.16.34.0", {"center": v(-7, 34) * mm, "radius": 0.15 * mm});
            skCircle(sketch, "E8.16.35.0", {"center": v(-7, 35) * mm, "radius": 0.15 * mm});
            skCircle(sketch, "E8.16.36.0", {"center": v(-7, 36) * mm, "radius": 0.15 * mm});
            skCircle(sketch, "E8.16.37.0", {"center": v(-7, 37) * mm, "radius": 0.15 * mm});
            skCircle(sketch, "E8.16.38.0", {"center": v(-7, 38) * mm, "radius": 0.15 * mm});
            skCircle(sketch, "E8.16.39.0", {"center": v(-7, 39) * mm, "radius": 0.15 * mm});
            skCircle(sketch, "E8.16.40.0", {"center": v(-7, 40) * mm, "radius": 0.15 * mm});
            skCircle(sketch, "E8.16.41.0", {"center": v(-7, 41) * mm, "radius": 0.15 * mm});
            skCircle(sketch, "E8.16.42.0", {"center": v(-7, 42) * mm, "radius": 0.15 * mm});
            skCircle(sketch, "E8.16.43.0", {"center": v(-7, 43) * mm, "radius": 0.15 * mm});
            skCircle(sketch, "E8.16.44.0", {"center": v(-7, 44) * mm, "radius": 0.15 * mm});
            skCircle(sketch, "E8.17.0.0", {"center": v(-8, 0) * mm, "radius": 0.15 * mm});
            skCircle(sketch, "E8.17.1.0", {"center": v(-8, 1) * mm, "radius": 0.15 * mm});
            skCircle(sketch, "E8.17.2.0", {"center": v(-8, 2) * mm, "radius": 0.15 * mm});
            skCircle(sketch, "E8.17.3.0", {"center": v(-8, 3) * mm, "radius": 0.15 * mm});
            skCircle(sketch, "E8.17.4.0", {"center": v(-8, 4) * mm, "radius": 0.15 * mm});
            skCircle(sketch, "E8.17.5.0", {"center": v(-8, 5) * mm, "radius": 0.15 * mm});
            skCircle(sketch, "E8.17.6.0", {"center": v(-8, 6) * mm, "radius": 0.15 * mm});
            skCircle(sketch, "E8.17.7.0", {"center": v(-8, 7) * mm, "radius": 0.15 * mm});
            skCircle(sketch, "E8.17.8.0", {"center": v(-8, 8) * mm, "radius": 0.15 * mm});
            skCircle(sketch, "E8.17.9.0", {"center": v(-8, 9) * mm, "radius": 0.15 * mm});
            skCircle(sketch, "E8.17.10.0", {"center": v(-8, 10) * mm, "radius": 0.15 * mm});
            skCircle(sketch, "E8.17.11.0", {"center": v(-8, 11) * mm, "radius": 0.15 * mm});
            skCircle(sketch, "E8.17.12.0", {"center": v(-8, 12) * mm, "radius": 0.15 * mm});
            skCircle(sketch, "E8.17.13.0", {"center": v(-8, 13) * mm, "radius": 0.15 * mm});
            skCircle(sketch, "E8.17.14.0", {"center": v(-8, 14) * mm, "radius": 0.15 * mm});
            skCircle(sketch, "E8.17.15.0", {"center": v(-8, 15) * mm, "radius": 0.15 * mm});
            skCircle(sketch, "E8.17.16.0", {"center": v(-8, 16) * mm, "radius": 0.15 * mm});
            skCircle(sketch, "E8.17.17.0", {"center": v(-8, 17) * mm, "radius": 0.15 * mm});
            skCircle(sketch, "E8.17.18.0", {"center": v(-8, 18) * mm, "radius": 0.15 * mm});
            skCircle(sketch, "E8.17.19.0", {"center": v(-8, 19) * mm, "radius": 0.15 * mm});
            skCircle(sketch, "E8.17.20.0", {"center": v(-8, 20) * mm, "radius": 0.15 * mm});
            skCircle(sketch, "E8.17.21.0", {"center": v(-8, 21) * mm, "radius": 0.15 * mm});
            skCircle(sketch, "E8.17.22.0", {"center": v(-8, 22) * mm, "radius": 0.15 * mm});
            skCircle(sketch, "E8.17.23.0", {"center": v(-8, 23) * mm, "radius": 0.15 * mm});
            skCircle(sketch, "E8.17.24.0", {"center": v(-8, 24) * mm, "radius": 0.15 * mm});
            skCircle(sketch, "E8.17.25.0", {"center": v(-8, 25) * mm, "radius": 0.15 * mm});
            skCircle(sketch, "E8.17.26.0", {"center": v(-8, 26) * mm, "radius": 0.15 * mm});
            skCircle(sketch, "E8.17.27.0", {"center": v(-8, 27) * mm, "radius": 0.15 * mm});
            skCircle(sketch, "E8.17.28.0", {"center": v(-8, 28) * mm, "radius": 0.15 * mm});
            skCircle(sketch, "E8.17.29.0", {"center": v(-8, 29) * mm, "radius": 0.15 * mm});
            skCircle(sketch, "E8.17.30.0", {"center": v(-8, 30) * mm, "radius": 0.15 * mm});
            skCircle(sketch, "E8.17.31.0", {"center": v(-8, 31) * mm, "radius": 0.15 * mm});
            skCircle(sketch, "E8.17.32.0", {"center": v(-8, 32) * mm, "radius": 0.15 * mm});
            skCircle(sketch, "E8.17.33.0", {"center": v(-8, 33) * mm, "radius": 0.15 * mm});
            skCircle(sketch, "E8.17.34.0", {"center": v(-8, 34) * mm, "radius": 0.15 * mm});
            skCircle(sketch, "E8.17.35.0", {"center": v(-8, 35) * mm, "radius": 0.15 * mm});
            skCircle(sketch, "E8.17.36.0", {"center": v(-8, 36) * mm, "radius": 0.15 * mm});
            skCircle(sketch, "E8.17.37.0", {"center": v(-8, 37) * mm, "radius": 0.15 * mm});
            skCircle(sketch, "E8.17.38.0", {"center": v(-8, 38) * mm, "radius": 0.15 * mm});
            skCircle(sketch, "E8.17.39.0", {"center": v(-8, 39) * mm, "radius": 0.15 * mm});
            skCircle(sketch, "E8.17.40.0", {"center": v(-8, 40) * mm, "radius": 0.15 * mm});
            skCircle(sketch, "E8.17.41.0", {"center": v(-8, 41) * mm, "radius": 0.15 * mm});
            skCircle(sketch, "E8.17.42.0", {"center": v(-8, 42) * mm, "radius": 0.15 * mm});
            skCircle(sketch, "E8.17.43.0", {"center": v(-8, 43) * mm, "radius": 0.15 * mm});
            skCircle(sketch, "E8.17.44.0", {"center": v(-8, 44) * mm, "radius": 0.15 * mm});
            skCircle(sketch, "E8.18.0.0", {"center": v(-9, 0) * mm, "radius": 0.15 * mm});
            skCircle(sketch, "E8.18.1.0", {"center": v(-9, 1) * mm, "radius": 0.15 * mm});
            skCircle(sketch, "E8.18.2.0", {"center": v(-9, 2) * mm, "radius": 0.15 * mm});
            skCircle(sketch, "E8.18.3.0", {"center": v(-9, 3) * mm, "radius": 0.15 * mm});
            skCircle(sketch, "E8.18.4.0", {"center": v(-9, 4) * mm, "radius": 0.15 * mm});
            skCircle(sketch, "E8.18.5.0", {"center": v(-9, 5) * mm, "radius": 0.15 * mm});
            skCircle(sketch, "E8.18.6.0", {"center": v(-9, 6) * mm, "radius": 0.15 * mm});
            skCircle(sketch, "E8.18.7.0", {"center": v(-9, 7) * mm, "radius": 0.15 * mm});
            skCircle(sketch, "E8.18.8.0", {"center": v(-9, 8) * mm, "radius": 0.15 * mm});
            skCircle(sketch, "E8.18.9.0", {"center": v(-9, 9) * mm, "radius": 0.15 * mm});
            skCircle(sketch, "E8.18.10.0", {"center": v(-9, 10) * mm, "radius": 0.15 * mm});
            skCircle(sketch, "E8.18.11.0", {"center": v(-9, 11) * mm, "radius": 0.15 * mm});
            skCircle(sketch, "E8.18.12.0", {"center": v(-9, 12) * mm, "radius": 0.15 * mm});
            skCircle(sketch, "E8.18.13.0", {"center": v(-9, 13) * mm, "radius": 0.15 * mm});
            skCircle(sketch, "E8.18.14.0", {"center": v(-9, 14) * mm, "radius": 0.15 * mm});
            skCircle(sketch, "E8.18.15.0", {"center": v(-9, 15) * mm, "radius": 0.15 * mm});
            skCircle(sketch, "E8.18.16.0", {"center": v(-9, 16) * mm, "radius": 0.15 * mm});
            skCircle(sketch, "E8.18.17.0", {"center": v(-9, 17) * mm, "radius": 0.15 * mm});
            skCircle(sketch, "E8.18.18.0", {"center": v(-9, 18) * mm, "radius": 0.15 * mm});
            skCircle(sketch, "E8.18.19.0", {"center": v(-9, 19) * mm, "radius": 0.15 * mm});
            skCircle(sketch, "E8.18.20.0", {"center": v(-9, 20) * mm, "radius": 0.15 * mm});
            skCircle(sketch, "E8.18.21.0", {"center": v(-9, 21) * mm, "radius": 0.15 * mm});
            skCircle(sketch, "E8.18.22.0", {"center": v(-9, 22) * mm, "radius": 0.15 * mm});
            skCircle(sketch, "E8.18.23.0", {"center": v(-9, 23) * mm, "radius": 0.15 * mm});
            skCircle(sketch, "E8.18.24.0", {"center": v(-9, 24) * mm, "radius": 0.15 * mm});
            skCircle(sketch, "E8.18.25.0", {"center": v(-9, 25) * mm, "radius": 0.15 * mm});
            skCircle(sketch, "E8.18.26.0", {"center": v(-9, 26) * mm, "radius": 0.15 * mm});
            skCircle(sketch, "E8.18.27.0", {"center": v(-9, 27) * mm, "radius": 0.15 * mm});
            skCircle(sketch, "E8.18.28.0", {"center": v(-9, 28) * mm, "radius": 0.15 * mm});
            skCircle(sketch, "E8.18.29.0", {"center": v(-9, 29) * mm, "radius": 0.15 * mm});
            skCircle(sketch, "E8.18.30.0", {"center": v(-9, 30) * mm, "radius": 0.15 * mm});
            skCircle(sketch, "E8.18.31.0", {"center": v(-9, 31) * mm, "radius": 0.15 * mm});
            skCircle(sketch, "E8.18.32.0", {"center": v(-9, 32) * mm, "radius": 0.15 * mm});
            skCircle(sketch, "E8.18.33.0", {"center": v(-9, 33) * mm, "radius": 0.15 * mm});
            skCircle(sketch, "E8.18.34.0", {"center": v(-9, 34) * mm, "radius": 0.15 * mm});
            skCircle(sketch, "E8.18.35.0", {"center": v(-9, 35) * mm, "radius": 0.15 * mm});
            skCircle(sketch, "E8.18.36.0", {"center": v(-9, 36) * mm, "radius": 0.15 * mm});
            skCircle(sketch, "E8.18.37.0", {"center": v(-9, 37) * mm, "radius": 0.15 * mm});
            skCircle(sketch, "E8.18.38.0", {"center": v(-9, 38) * mm, "radius": 0.15 * mm});
            skCircle(sketch, "E8.18.39.0", {"center": v(-9, 39) * mm, "radius": 0.15 * mm});
            skCircle(sketch, "E8.18.40.0", {"center": v(-9, 40) * mm, "radius": 0.15 * mm});
            skCircle(sketch, "E8.18.41.0", {"center": v(-9, 41) * mm, "radius": 0.15 * mm});
            skCircle(sketch, "E8.18.42.0", {"center": v(-9, 42) * mm, "radius": 0.15 * mm});
            skCircle(sketch, "E8.18.43.0", {"center": v(-9, 43) * mm, "radius": 0.15 * mm});
            skCircle(sketch, "E8.18.44.0", {"center": v(-9, 44) * mm, "radius": 0.15 * mm});
            skCircle(sketch, "E8.19.0.0", {"center": v(-10, 0) * mm, "radius": 0.15 * mm});
            skCircle(sketch, "E8.19.1.0", {"center": v(-10, 1) * mm, "radius": 0.15 * mm});
            skCircle(sketch, "E8.19.2.0", {"center": v(-10, 2) * mm, "radius": 0.15 * mm});
            skCircle(sketch, "E8.19.3.0", {"center": v(-10, 3) * mm, "radius": 0.15 * mm});
            skCircle(sketch, "E8.19.4.0", {"center": v(-10, 4) * mm, "radius": 0.15 * mm});
            skCircle(sketch, "E8.19.5.0", {"center": v(-10, 5) * mm, "radius": 0.15 * mm});
            skCircle(sketch, "E8.19.6.0", {"center": v(-10, 6) * mm, "radius": 0.15 * mm});
            skCircle(sketch, "E8.19.7.0", {"center": v(-10, 7) * mm, "radius": 0.15 * mm});
            skCircle(sketch, "E8.19.8.0", {"center": v(-10, 8) * mm, "radius": 0.15 * mm});
            skCircle(sketch, "E8.19.9.0", {"center": v(-10, 9) * mm, "radius": 0.15 * mm});
            skCircle(sketch, "E8.19.10.0", {"center": v(-10, 10) * mm, "radius": 0.15 * mm});
            skCircle(sketch, "E8.19.11.0", {"center": v(-10, 11) * mm, "radius": 0.15 * mm});
            skCircle(sketch, "E8.19.12.0", {"center": v(-10, 12) * mm, "radius": 0.15 * mm});
            skCircle(sketch, "E8.19.13.0", {"center": v(-10, 13) * mm, "radius": 0.15 * mm});
            skCircle(sketch, "E8.19.14.0", {"center": v(-10, 14) * mm, "radius": 0.15 * mm});
            skCircle(sketch, "E8.19.15.0", {"center": v(-10, 15) * mm, "radius": 0.15 * mm});
            skCircle(sketch, "E8.19.16.0", {"center": v(-10, 16) * mm, "radius": 0.15 * mm});
            skCircle(sketch, "E8.19.17.0", {"center": v(-10, 17) * mm, "radius": 0.15 * mm});
            skCircle(sketch, "E8.19.18.0", {"center": v(-10, 18) * mm, "radius": 0.15 * mm});
            skCircle(sketch, "E8.19.19.0", {"center": v(-10, 19) * mm, "radius": 0.15 * mm});
            skCircle(sketch, "E8.19.20.0", {"center": v(-10, 20) * mm, "radius": 0.15 * mm});
            skCircle(sketch, "E8.19.21.0", {"center": v(-10, 21) * mm, "radius": 0.15 * mm});
            skCircle(sketch, "E8.19.22.0", {"center": v(-10, 22) * mm, "radius": 0.15 * mm});
            skCircle(sketch, "E8.19.23.0", {"center": v(-10, 23) * mm, "radius": 0.15 * mm});
            skCircle(sketch, "E8.19.24.0", {"center": v(-10, 24) * mm, "radius": 0.15 * mm});
            skCircle(sketch, "E8.19.25.0", {"center": v(-10, 25) * mm, "radius": 0.15 * mm});
            skCircle(sketch, "E8.19.26.0", {"center": v(-10, 26) * mm, "radius": 0.15 * mm});
            skCircle(sketch, "E8.19.27.0", {"center": v(-10, 27) * mm, "radius": 0.15 * mm});
            skCircle(sketch, "E8.19.28.0", {"center": v(-10, 28) * mm, "radius": 0.15 * mm});
            skCircle(sketch, "E8.19.29.0", {"center": v(-10, 29) * mm, "radius": 0.15 * mm});
            skCircle(sketch, "E8.19.30.0", {"center": v(-10, 30) * mm, "radius": 0.15 * mm});
            skCircle(sketch, "E8.19.31.0", {"center": v(-10, 31) * mm, "radius": 0.15 * mm});
            skCircle(sketch, "E8.19.32.0", {"center": v(-10, 32) * mm, "radius": 0.15 * mm});
            skCircle(sketch, "E8.19.33.0", {"center": v(-10, 33) * mm, "radius": 0.15 * mm});
            skCircle(sketch, "E8.19.34.0", {"center": v(-10, 34) * mm, "radius": 0.15 * mm});
            skCircle(sketch, "E8.19.35.0", {"center": v(-10, 35) * mm, "radius": 0.15 * mm});
            skCircle(sketch, "E8.19.36.0", {"center": v(-10, 36) * mm, "radius": 0.15 * mm});
            skCircle(sketch, "E8.19.37.0", {"center": v(-10, 37) * mm, "radius": 0.15 * mm});
            skCircle(sketch, "E8.19.38.0", {"center": v(-10, 38) * mm, "radius": 0.15 * mm});
            skCircle(sketch, "E8.19.39.0", {"center": v(-10, 39) * mm, "radius": 0.15 * mm});
            skCircle(sketch, "E8.19.40.0", {"center": v(-10, 40) * mm, "radius": 0.15 * mm});
            skCircle(sketch, "E8.19.41.0", {"center": v(-10, 41) * mm, "radius": 0.15 * mm});
            skCircle(sketch, "E8.19.42.0", {"center": v(-10, 42) * mm, "radius": 0.15 * mm});
            skCircle(sketch, "E8.19.43.0", {"center": v(-10, 43) * mm, "radius": 0.15 * mm});
            skCircle(sketch, "E8.19.44.0", {"center": v(-10, 44) * mm, "radius": 0.15 * mm});
            skLineSegment(sketch, "E8.direction1", {"start": v(9, 0) * mm, "end": v(8, 0) * mm, "construction": true});
            skLineSegment(sketch, "E8.direction2", {"start": v(9, 0) * mm, "end": v(9, 1) * mm, "construction": true});
            skSolve(sketch);
        }
        {
            var Q0;
            Q0=qCreatedBy(makeId("Right.planeOp"),FACE);
            var sketch = newSketch(context, id + "F6", { "sketchPlane" : qUnion([Q0])});
            skCircle(sketch, "E9", {"center": v(0, 0) * mm, "radius": 0.15 * mm});
            skCircle(sketch, "E10.0.1.0", {"center": v(0, 1) * mm, "radius": 0.15 * mm});
            skCircle(sketch, "E10.0.2.0", {"center": v(0, 2) * mm, "radius": 0.15 * mm});
            skCircle(sketch, "E10.0.3.0", {"center": v(0, 3) * mm, "radius": 0.15 * mm});
            skCircle(sketch, "E10.0.4.0", {"center": v(0, 4) * mm, "radius": 0.15 * mm});
            skCircle(sketch, "E10.0.5.0", {"center": v(0, 5) * mm, "radius": 0.15 * mm});
            skCircle(sketch, "E10.0.6.0", {"center": v(0, 6) * mm, "radius": 0.15 * mm});
            skCircle(sketch, "E10.0.7.0", {"center": v(0, 7) * mm, "radius": 0.15 * mm});
            skCircle(sketch, "E10.0.8.0", {"center": v(0, 8) * mm, "radius": 0.15 * mm});
            skCircle(sketch, "E10.0.9.0", {"center": v(0, 9) * mm, "radius": 0.15 * mm});
            skCircle(sketch, "E10.1.0.0", {"center": v(1, 0) * mm, "radius": 0.15 * mm});
            skCircle(sketch, "E10.1.1.0", {"center": v(1, 1) * mm, "radius": 0.15 * mm});
            skCircle(sketch, "E10.1.2.0", {"center": v(1, 2) * mm, "radius": 0.15 * mm});
            skCircle(sketch, "E10.1.3.0", {"center": v(1, 3) * mm, "radius": 0.15 * mm});
            skCircle(sketch, "E10.1.4.0", {"center": v(1, 4) * mm, "radius": 0.15 * mm});
            skCircle(sketch, "E10.1.5.0", {"center": v(1, 5) * mm, "radius": 0.15 * mm});
            skCircle(sketch, "E10.1.6.0", {"center": v(1, 6) * mm, "radius": 0.15 * mm});
            skCircle(sketch, "E10.1.7.0", {"center": v(1, 7) * mm, "radius": 0.15 * mm});
            skCircle(sketch, "E10.1.8.0", {"center": v(1, 8) * mm, "radius": 0.15 * mm});
            skCircle(sketch, "E10.1.9.0", {"center": v(1, 9) * mm, "radius": 0.15 * mm});
            skCircle(sketch, "E10.2.0.0", {"center": v(2, 0) * mm, "radius": 0.15 * mm});
            skCircle(sketch, "E10.2.1.0", {"center": v(2, 1) * mm, "radius": 0.15 * mm});
            skCircle(sketch, "E10.2.2.0", {"center": v(2, 2) * mm, "radius": 0.15 * mm});
            skCircle(sketch, "E10.2.3.0", {"center": v(2, 3) * mm, "radius": 0.15 * mm});
            skCircle(sketch, "E10.2.4.0", {"center": v(2, 4) * mm, "radius": 0.15 * mm});
            skCircle(sketch, "E10.2.5.0", {"center": v(2, 5) * mm, "radius": 0.15 * mm});
            skCircle(sketch, "E10.2.6.0", {"center": v(2, 6) * mm, "radius": 0.15 * mm});
            skCircle(sketch, "E10.2.7.0", {"center": v(2, 7) * mm, "radius": 0.15 * mm});
            skCircle(sketch, "E10.2.8.0", {"center": v(2, 8) * mm, "radius": 0.15 * mm});
            skCircle(sketch, "E10.2.9.0", {"center": v(2, 9) * mm, "radius": 0.15 * mm});
            skCircle(sketch, "E10.3.0.0", {"center": v(3, 0) * mm, "radius": 0.15 * mm});
            skCircle(sketch, "E10.3.1.0", {"center": v(3, 1) * mm, "radius": 0.15 * mm});
            skCircle(sketch, "E10.3.2.0", {"center": v(3, 2) * mm, "radius": 0.15 * mm});
            skCircle(sketch, "E10.3.3.0", {"center": v(3, 3) * mm, "radius": 0.15 * mm});
            skCircle(sketch, "E10.3.4.0", {"center": v(3, 4) * mm, "radius": 0.15 * mm});
            skCircle(sketch, "E10.3.5.0", {"center": v(3, 5) * mm, "radius": 0.15 * mm});
            skCircle(sketch, "E10.3.6.0", {"center": v(3, 6) * mm, "radius": 0.15 * mm});
            skCircle(sketch, "E10.3.7.0", {"center": v(3, 7) * mm, "radius": 0.15 * mm});
            skCircle(sketch, "E10.3.8.0", {"center": v(3, 8) * mm, "radius": 0.15 * mm});
            skCircle(sketch, "E10.3.9.0", {"center": v(3, 9) * mm, "radius": 0.15 * mm});
            skCircle(sketch, "E10.4.0.0", {"center": v(4, 0) * mm, "radius": 0.15 * mm});
            skCircle(sketch, "E10.4.1.0", {"center": v(4, 1) * mm, "radius": 0.15 * mm});
            skCircle(sketch, "E10.4.2.0", {"center": v(4, 2) * mm, "radius": 0.15 * mm});
            skCircle(sketch, "E10.4.3.0", {"center": v(4, 3) * mm, "radius": 0.15 * mm});
            skCircle(sketch, "E10.4.4.0", {"center": v(4, 4) * mm, "radius": 0.15 * mm});
            skCircle(sketch, "E10.4.5.0", {"center": v(4, 5) * mm, "radius": 0.15 * mm});
            skCircle(sketch, "E10.4.6.0", {"center": v(4, 6) * mm, "radius": 0.15 * mm});
            skCircle(sketch, "E10.4.7.0", {"center": v(4, 7) * mm, "radius": 0.15 * mm});
            skCircle(sketch, "E10.4.8.0", {"center": v(4, 8) * mm, "radius": 0.15 * mm});
            skCircle(sketch, "E10.4.9.0", {"center": v(4, 9) * mm, "radius": 0.15 * mm});
            skCircle(sketch, "E10.5.0.0", {"center": v(5, 0) * mm, "radius": 0.15 * mm});
            skCircle(sketch, "E10.5.1.0", {"center": v(5, 1) * mm, "radius": 0.15 * mm});
            skCircle(sketch, "E10.5.2.0", {"center": v(5, 2) * mm, "radius": 0.15 * mm});
            skCircle(sketch, "E10.5.3.0", {"center": v(5, 3) * mm, "radius": 0.15 * mm});
            skCircle(sketch, "E10.5.4.0", {"center": v(5, 4) * mm, "radius": 0.15 * mm});
            skCircle(sketch, "E10.5.5.0", {"center": v(5, 5) * mm, "radius": 0.15 * mm});
            skCircle(sketch, "E10.5.6.0", {"center": v(5, 6) * mm, "radius": 0.15 * mm});
            skCircle(sketch, "E10.5.7.0", {"center": v(5, 7) * mm, "radius": 0.15 * mm});
            skCircle(sketch, "E10.5.8.0", {"center": v(5, 8) * mm, "radius": 0.15 * mm});
            skCircle(sketch, "E10.5.9.0", {"center": v(5, 9) * mm, "radius": 0.15 * mm});
            skCircle(sketch, "E10.6.0.0", {"center": v(6, 0) * mm, "radius": 0.15 * mm});
            skCircle(sketch, "E10.6.1.0", {"center": v(6, 1) * mm, "radius": 0.15 * mm});
            skCircle(sketch, "E10.6.2.0", {"center": v(6, 2) * mm, "radius": 0.15 * mm});
            skCircle(sketch, "E10.6.3.0", {"center": v(6, 3) * mm, "radius": 0.15 * mm});
            skCircle(sketch, "E10.6.4.0", {"center": v(6, 4) * mm, "radius": 0.15 * mm});
            skCircle(sketch, "E10.6.5.0", {"center": v(6, 5) * mm, "radius": 0.15 * mm});
            skCircle(sketch, "E10.6.6.0", {"center": v(6, 6) * mm, "radius": 0.15 * mm});
            skCircle(sketch, "E10.6.7.0", {"center": v(6, 7) * mm, "radius": 0.15 * mm});
            skCircle(sketch, "E10.6.8.0", {"center": v(6, 8) * mm, "radius": 0.15 * mm});
            skCircle(sketch, "E10.6.9.0", {"center": v(6, 9) * mm, "radius": 0.15 * mm});
            skCircle(sketch, "E10.7.0.0", {"center": v(7, 0) * mm, "radius": 0.15 * mm});
            skCircle(sketch, "E10.7.1.0", {"center": v(7, 1) * mm, "radius": 0.15 * mm});
            skCircle(sketch, "E10.7.2.0", {"center": v(7, 2) * mm, "radius": 0.15 * mm});
            skCircle(sketch, "E10.7.3.0", {"center": v(7, 3) * mm, "radius": 0.15 * mm});
            skCircle(sketch, "E10.7.4.0", {"center": v(7, 4) * mm, "radius": 0.15 * mm});
            skCircle(sketch, "E10.7.5.0", {"center": v(7, 5) * mm, "radius": 0.15 * mm});
            skCircle(sketch, "E10.7.6.0", {"center": v(7, 6) * mm, "radius": 0.15 * mm});
            skCircle(sketch, "E10.7.7.0", {"center": v(7, 7) * mm, "radius": 0.15 * mm});
            skCircle(sketch, "E10.7.8.0", {"center": v(7, 8) * mm, "radius": 0.15 * mm});
            skCircle(sketch, "E10.7.9.0", {"center": v(7, 9) * mm, "radius": 0.15 * mm});
            skCircle(sketch, "E10.8.0.0", {"center": v(8, 0) * mm, "radius": 0.15 * mm});
            skCircle(sketch, "E10.8.1.0", {"center": v(8, 1) * mm, "radius": 0.15 * mm});
            skCircle(sketch, "E10.8.2.0", {"center": v(8, 2) * mm, "radius": 0.15 * mm});
            skCircle(sketch, "E10.8.3.0", {"center": v(8, 3) * mm, "radius": 0.15 * mm});
            skCircle(sketch, "E10.8.4.0", {"center": v(8, 4) * mm, "radius": 0.15 * mm});
            skCircle(sketch, "E10.8.5.0", {"center": v(8, 5) * mm, "radius": 0.15 * mm});
            skCircle(sketch, "E10.8.6.0", {"center": v(8, 6) * mm, "radius": 0.15 * mm});
            skCircle(sketch, "E10.8.7.0", {"center": v(8, 7) * mm, "radius": 0.15 * mm});
            skCircle(sketch, "E10.8.8.0", {"center": v(8, 8) * mm, "radius": 0.15 * mm});
            skCircle(sketch, "E10.8.9.0", {"center": v(8, 9) * mm, "radius": 0.15 * mm});
            skCircle(sketch, "E10.9.0.0", {"center": v(9, 0) * mm, "radius": 0.15 * mm});
            skCircle(sketch, "E10.9.1.0", {"center": v(9, 1) * mm, "radius": 0.15 * mm});
            skCircle(sketch, "E10.9.2.0", {"center": v(9, 2) * mm, "radius": 0.15 * mm});
            skCircle(sketch, "E10.9.3.0", {"center": v(9, 3) * mm, "radius": 0.15 * mm});
            skCircle(sketch, "E10.9.4.0", {"center": v(9, 4) * mm, "radius": 0.15 * mm});
            skCircle(sketch, "E10.9.5.0", {"center": v(9, 5) * mm, "radius": 0.15 * mm});
            skCircle(sketch, "E10.9.6.0", {"center": v(9, 6) * mm, "radius": 0.15 * mm});
            skCircle(sketch, "E10.9.7.0", {"center": v(9, 7) * mm, "radius": 0.15 * mm});
            skCircle(sketch, "E10.9.8.0", {"center": v(9, 8) * mm, "radius": 0.15 * mm});
            skCircle(sketch, "E10.9.9.0", {"center": v(9, 9) * mm, "radius": 0.15 * mm});
            skLineSegment(sketch, "E10.direction1", {"start": v(0, 0) * mm, "end": v(1, 0) * mm, "construction": true});
            skLineSegment(sketch, "E10.direction2", {"start": v(0, 0) * mm, "end": v(0, 1) * mm, "construction": true});
            skCircle(sketch, "E11.0.10.0", {"center": v(9, -1) * mm, "radius": 0.15 * mm});
            skCircle(sketch, "E11.0.11.0", {"center": v(9, -2) * mm, "radius": 0.15 * mm});
            skCircle(sketch, "E11.0.12.0", {"center": v(9, -3) * mm, "radius": 0.15 * mm});
            skCircle(sketch, "E11.0.13.0", {"center": v(9, -4) * mm, "radius": 0.15 * mm});
            skCircle(sketch, "E11.0.14.0", {"center": v(9, -5) * mm, "radius": 0.15 * mm});
            skCircle(sketch, "E11.0.15.0", {"center": v(9, -6) * mm, "radius": 0.15 * mm});
            skCircle(sketch, "E11.0.16.0", {"center": v(9, -7) * mm, "radius": 0.15 * mm});
            skCircle(sketch, "E11.0.17.0", {"center": v(9, -8) * mm, "radius": 0.15 * mm});
            skCircle(sketch, "E11.0.18.0", {"center": v(9, -9) * mm, "radius": 0.15 * mm});
            skCircle(sketch, "E11.0.19.0", {"center": v(9, -10) * mm, "radius": 0.15 * mm});
            skCircle(sketch, "E11.1.10.0", {"center": v(8, -1) * mm, "radius": 0.15 * mm});
            skCircle(sketch, "E11.1.11.0", {"center": v(8, -2) * mm, "radius": 0.15 * mm});
            skCircle(sketch, "E11.1.12.0", {"center": v(8, -3) * mm, "radius": 0.15 * mm});
            skCircle(sketch, "E11.1.13.0", {"center": v(8, -4) * mm, "radius": 0.15 * mm});
            skCircle(sketch, "E11.1.14.0", {"center": v(8, -5) * mm, "radius": 0.15 * mm});
            skCircle(sketch, "E11.1.15.0", {"center": v(8, -6) * mm, "radius": 0.15 * mm});
            skCircle(sketch, "E11.1.16.0", {"center": v(8, -7) * mm, "radius": 0.15 * mm});
            skCircle(sketch, "E11.1.17.0", {"center": v(8, -8) * mm, "radius": 0.15 * mm});
            skCircle(sketch, "E11.1.18.0", {"center": v(8, -9) * mm, "radius": 0.15 * mm});
            skCircle(sketch, "E11.1.19.0", {"center": v(8, -10) * mm, "radius": 0.15 * mm});
            skCircle(sketch, "E11.2.10.0", {"center": v(7, -1) * mm, "radius": 0.15 * mm});
            skCircle(sketch, "E11.2.11.0", {"center": v(7, -2) * mm, "radius": 0.15 * mm});
            skCircle(sketch, "E11.2.12.0", {"center": v(7, -3) * mm, "radius": 0.15 * mm});
            skCircle(sketch, "E11.2.13.0", {"center": v(7, -4) * mm, "radius": 0.15 * mm});
            skCircle(sketch, "E11.2.14.0", {"center": v(7, -5) * mm, "radius": 0.15 * mm});
            skCircle(sketch, "E11.2.15.0", {"center": v(7, -6) * mm, "radius": 0.15 * mm});
            skCircle(sketch, "E11.2.16.0", {"center": v(7, -7) * mm, "radius": 0.15 * mm});
            skCircle(sketch, "E11.2.17.0", {"center": v(7, -8) * mm, "radius": 0.15 * mm});
            skCircle(sketch, "E11.2.18.0", {"center": v(7, -9) * mm, "radius": 0.15 * mm});
            skCircle(sketch, "E11.2.19.0", {"center": v(7, -10) * mm, "radius": 0.15 * mm});
            skCircle(sketch, "E11.3.10.0", {"center": v(6, -1) * mm, "radius": 0.15 * mm});
            skCircle(sketch, "E11.3.11.0", {"center": v(6, -2) * mm, "radius": 0.15 * mm});
            skCircle(sketch, "E11.3.12.0", {"center": v(6, -3) * mm, "radius": 0.15 * mm});
            skCircle(sketch, "E11.3.13.0", {"center": v(6, -4) * mm, "radius": 0.15 * mm});
            skCircle(sketch, "E11.3.14.0", {"center": v(6, -5) * mm, "radius": 0.15 * mm});
            skCircle(sketch, "E11.3.15.0", {"center": v(6, -6) * mm, "radius": 0.15 * mm});
            skCircle(sketch, "E11.3.16.0", {"center": v(6, -7) * mm, "radius": 0.15 * mm});
            skCircle(sketch, "E11.3.17.0", {"center": v(6, -8) * mm, "radius": 0.15 * mm});
            skCircle(sketch, "E11.3.18.0", {"center": v(6, -9) * mm, "radius": 0.15 * mm});
            skCircle(sketch, "E11.3.19.0", {"center": v(6, -10) * mm, "radius": 0.15 * mm});
            skCircle(sketch, "E11.4.10.0", {"center": v(5, -1) * mm, "radius": 0.15 * mm});
            skCircle(sketch, "E11.4.11.0", {"center": v(5, -2) * mm, "radius": 0.15 * mm});
            skCircle(sketch, "E11.4.12.0", {"center": v(5, -3) * mm, "radius": 0.15 * mm});
            skCircle(sketch, "E11.4.13.0", {"center": v(5, -4) * mm, "radius": 0.15 * mm});
            skCircle(sketch, "E11.4.14.0", {"center": v(5, -5) * mm, "radius": 0.15 * mm});
            skCircle(sketch, "E11.4.15.0", {"center": v(5, -6) * mm, "radius": 0.15 * mm});
            skCircle(sketch, "E11.4.16.0", {"center": v(5, -7) * mm, "radius": 0.15 * mm});
            skCircle(sketch, "E11.4.17.0", {"center": v(5, -8) * mm, "radius": 0.15 * mm});
            skCircle(sketch, "E11.4.18.0", {"center": v(5, -9) * mm, "radius": 0.15 * mm});
            skCircle(sketch, "E11.4.19.0", {"center": v(5, -10) * mm, "radius": 0.15 * mm});
            skCircle(sketch, "E11.5.10.0", {"center": v(4, -1) * mm, "radius": 0.15 * mm});
            skCircle(sketch, "E11.5.11.0", {"center": v(4, -2) * mm, "radius": 0.15 * mm});
            skCircle(sketch, "E11.5.12.0", {"center": v(4, -3) * mm, "radius": 0.15 * mm});
            skCircle(sketch, "E11.5.13.0", {"center": v(4, -4) * mm, "radius": 0.15 * mm});
            skCircle(sketch, "E11.5.14.0", {"center": v(4, -5) * mm, "radius": 0.15 * mm});
            skCircle(sketch, "E11.5.15.0", {"center": v(4, -6) * mm, "radius": 0.15 * mm});
            skCircle(sketch, "E11.5.16.0", {"center": v(4, -7) * mm, "radius": 0.15 * mm});
            skCircle(sketch, "E11.5.17.0", {"center": v(4, -8) * mm, "radius": 0.15 * mm});
            skCircle(sketch, "E11.5.18.0", {"center": v(4, -9) * mm, "radius": 0.15 * mm});
            skCircle(sketch, "E11.5.19.0", {"center": v(4, -10) * mm, "radius": 0.15 * mm});
            skCircle(sketch, "E11.6.10.0", {"center": v(3, -1) * mm, "radius": 0.15 * mm});
            skCircle(sketch, "E11.6.11.0", {"center": v(3, -2) * mm, "radius": 0.15 * mm});
            skCircle(sketch, "E11.6.12.0", {"center": v(3, -3) * mm, "radius": 0.15 * mm});
            skCircle(sketch, "E11.6.13.0", {"center": v(3, -4) * mm, "radius": 0.15 * mm});
            skCircle(sketch, "E11.6.14.0", {"center": v(3, -5) * mm, "radius": 0.15 * mm});
            skCircle(sketch, "E11.6.15.0", {"center": v(3, -6) * mm, "radius": 0.15 * mm});
            skCircle(sketch, "E11.6.16.0", {"center": v(3, -7) * mm, "radius": 0.15 * mm});
            skCircle(sketch, "E11.6.17.0", {"center": v(3, -8) * mm, "radius": 0.15 * mm});
            skCircle(sketch, "E11.6.18.0", {"center": v(3, -9) * mm, "radius": 0.15 * mm});
            skCircle(sketch, "E11.6.19.0", {"center": v(3, -10) * mm, "radius": 0.15 * mm});
            skCircle(sketch, "E11.7.10.0", {"center": v(2, -1) * mm, "radius": 0.15 * mm});
            skCircle(sketch, "E11.7.11.0", {"center": v(2, -2) * mm, "radius": 0.15 * mm});
            skCircle(sketch, "E11.7.12.0", {"center": v(2, -3) * mm, "radius": 0.15 * mm});
            skCircle(sketch, "E11.7.13.0", {"center": v(2, -4) * mm, "radius": 0.15 * mm});
            skCircle(sketch, "E11.7.14.0", {"center": v(2, -5) * mm, "radius": 0.15 * mm});
            skCircle(sketch, "E11.7.15.0", {"center": v(2, -6) * mm, "radius": 0.15 * mm});
            skCircle(sketch, "E11.7.16.0", {"center": v(2, -7) * mm, "radius": 0.15 * mm});
            skCircle(sketch, "E11.7.17.0", {"center": v(2, -8) * mm, "radius": 0.15 * mm});
            skCircle(sketch, "E11.7.18.0", {"center": v(2, -9) * mm, "radius": 0.15 * mm});
            skCircle(sketch, "E11.7.19.0", {"center": v(2, -10) * mm, "radius": 0.15 * mm});
            skCircle(sketch, "E11.8.10.0", {"center": v(1, -1) * mm, "radius": 0.15 * mm});
            skCircle(sketch, "E11.8.11.0", {"center": v(1, -2) * mm, "radius": 0.15 * mm});
            skCircle(sketch, "E11.8.12.0", {"center": v(1, -3) * mm, "radius": 0.15 * mm});
            skCircle(sketch, "E11.8.13.0", {"center": v(1, -4) * mm, "radius": 0.15 * mm});
            skCircle(sketch, "E11.8.14.0", {"center": v(1, -5) * mm, "radius": 0.15 * mm});
            skCircle(sketch, "E11.8.15.0", {"center": v(1, -6) * mm, "radius": 0.15 * mm});
            skCircle(sketch, "E11.8.16.0", {"center": v(1, -7) * mm, "radius": 0.15 * mm});
            skCircle(sketch, "E11.8.17.0", {"center": v(1, -8) * mm, "radius": 0.15 * mm});
            skCircle(sketch, "E11.8.18.0", {"center": v(1, -9) * mm, "radius": 0.15 * mm});
            skCircle(sketch, "E11.8.19.0", {"center": v(1, -10) * mm, "radius": 0.15 * mm});
            skCircle(sketch, "E11.9.10.0", {"center": v(0, -1) * mm, "radius": 0.15 * mm});
            skCircle(sketch, "E11.9.11.0", {"center": v(0, -2) * mm, "radius": 0.15 * mm});
            skCircle(sketch, "E11.9.12.0", {"center": v(0, -3) * mm, "radius": 0.15 * mm});
            skCircle(sketch, "E11.9.13.0", {"center": v(0, -4) * mm, "radius": 0.15 * mm});
            skCircle(sketch, "E11.9.14.0", {"center": v(0, -5) * mm, "radius": 0.15 * mm});
            skCircle(sketch, "E11.9.15.0", {"center": v(0, -6) * mm, "radius": 0.15 * mm});
            skCircle(sketch, "E11.9.16.0", {"center": v(0, -7) * mm, "radius": 0.15 * mm});
            skCircle(sketch, "E11.9.17.0", {"center": v(0, -8) * mm, "radius": 0.15 * mm});
            skCircle(sketch, "E11.9.18.0", {"center": v(0, -9) * mm, "radius": 0.15 * mm});
            skCircle(sketch, "E11.9.19.0", {"center": v(0, -10) * mm, "radius": 0.15 * mm});
            skCircle(sketch, "E11.10.0.0", {"center": v(-1, 9) * mm, "radius": 0.15 * mm});
            skCircle(sketch, "E11.10.1.0", {"center": v(-1, 8) * mm, "radius": 0.15 * mm});
            skCircle(sketch, "E11.10.2.0", {"center": v(-1, 7) * mm, "radius": 0.15 * mm});
            skCircle(sketch, "E11.10.3.0", {"center": v(-1, 6) * mm, "radius": 0.15 * mm});
            skCircle(sketch, "E11.10.4.0", {"center": v(-1, 5) * mm, "radius": 0.15 * mm});
            skCircle(sketch, "E11.10.5.0", {"center": v(-1, 4) * mm, "radius": 0.15 * mm});
            skCircle(sketch, "E11.10.6.0", {"center": v(-1, 3) * mm, "radius": 0.15 * mm});
            skCircle(sketch, "E11.10.7.0", {"center": v(-1, 2) * mm, "radius": 0.15 * mm});
            skCircle(sketch, "E11.10.8.0", {"center": v(-1, 1) * mm, "radius": 0.15 * mm});
            skCircle(sketch, "E11.10.9.0", {"center": v(-1, 0) * mm, "radius": 0.15 * mm});
            skCircle(sketch, "E11.10.10.0", {"center": v(-1, -1) * mm, "radius": 0.15 * mm});
            skCircle(sketch, "E11.10.11.0", {"center": v(-1, -2) * mm, "radius": 0.15 * mm});
            skCircle(sketch, "E11.10.12.0", {"center": v(-1, -3) * mm, "radius": 0.15 * mm});
            skCircle(sketch, "E11.10.13.0", {"center": v(-1, -4) * mm, "radius": 0.15 * mm});
            skCircle(sketch, "E11.10.14.0", {"center": v(-1, -5) * mm, "radius": 0.15 * mm});
            skCircle(sketch, "E11.10.15.0", {"center": v(-1, -6) * mm, "radius": 0.15 * mm});
            skCircle(sketch, "E11.10.16.0", {"center": v(-1, -7) * mm, "radius": 0.15 * mm});
            skCircle(sketch, "E11.10.17.0", {"center": v(-1, -8) * mm, "radius": 0.15 * mm});
            skCircle(sketch, "E11.10.18.0", {"center": v(-1, -9) * mm, "radius": 0.15 * mm});
            skCircle(sketch, "E11.10.19.0", {"center": v(-1, -10) * mm, "radius": 0.15 * mm});
            skCircle(sketch, "E11.11.0.0", {"center": v(-2, 9) * mm, "radius": 0.15 * mm});
            skCircle(sketch, "E11.11.1.0", {"center": v(-2, 8) * mm, "radius": 0.15 * mm});
            skCircle(sketch, "E11.11.2.0", {"center": v(-2, 7) * mm, "radius": 0.15 * mm});
            skCircle(sketch, "E11.11.3.0", {"center": v(-2, 6) * mm, "radius": 0.15 * mm});
            skCircle(sketch, "E11.11.4.0", {"center": v(-2, 5) * mm, "radius": 0.15 * mm});
            skCircle(sketch, "E11.11.5.0", {"center": v(-2, 4) * mm, "radius": 0.15 * mm});
            skCircle(sketch, "E11.11.6.0", {"center": v(-2, 3) * mm, "radius": 0.15 * mm});
            skCircle(sketch, "E11.11.7.0", {"center": v(-2, 2) * mm, "radius": 0.15 * mm});
            skCircle(sketch, "E11.11.8.0", {"center": v(-2, 1) * mm, "radius": 0.15 * mm});
            skCircle(sketch, "E11.11.9.0", {"center": v(-2, 0) * mm, "radius": 0.15 * mm});
            skCircle(sketch, "E11.11.10.0", {"center": v(-2, -1) * mm, "radius": 0.15 * mm});
            skCircle(sketch, "E11.11.11.0", {"center": v(-2, -2) * mm, "radius": 0.15 * mm});
            skCircle(sketch, "E11.11.12.0", {"center": v(-2, -3) * mm, "radius": 0.15 * mm});
            skCircle(sketch, "E11.11.13.0", {"center": v(-2, -4) * mm, "radius": 0.15 * mm});
            skCircle(sketch, "E11.11.14.0", {"center": v(-2, -5) * mm, "radius": 0.15 * mm});
            skCircle(sketch, "E11.11.15.0", {"center": v(-2, -6) * mm, "radius": 0.15 * mm});
            skCircle(sketch, "E11.11.16.0", {"center": v(-2, -7) * mm, "radius": 0.15 * mm});
            skCircle(sketch, "E11.11.17.0", {"center": v(-2, -8) * mm, "radius": 0.15 * mm});
            skCircle(sketch, "E11.11.18.0", {"center": v(-2, -9) * mm, "radius": 0.15 * mm});
            skCircle(sketch, "E11.11.19.0", {"center": v(-2, -10) * mm, "radius": 0.15 * mm});
            skCircle(sketch, "E11.12.0.0", {"center": v(-3, 9) * mm, "radius": 0.15 * mm});
            skCircle(sketch, "E11.12.1.0", {"center": v(-3, 8) * mm, "radius": 0.15 * mm});
            skCircle(sketch, "E11.12.2.0", {"center": v(-3, 7) * mm, "radius": 0.15 * mm});
            skCircle(sketch, "E11.12.3.0", {"center": v(-3, 6) * mm, "radius": 0.15 * mm});
            skCircle(sketch, "E11.12.4.0", {"center": v(-3, 5) * mm, "radius": 0.15 * mm});
            skCircle(sketch, "E11.12.5.0", {"center": v(-3, 4) * mm, "radius": 0.15 * mm});
            skCircle(sketch, "E11.12.6.0", {"center": v(-3, 3) * mm, "radius": 0.15 * mm});
            skCircle(sketch, "E11.12.7.0", {"center": v(-3, 2) * mm, "radius": 0.15 * mm});
            skCircle(sketch, "E11.12.8.0", {"center": v(-3, 1) * mm, "radius": 0.15 * mm});
            skCircle(sketch, "E11.12.9.0", {"center": v(-3, 0) * mm, "radius": 0.15 * mm});
            skCircle(sketch, "E11.12.10.0", {"center": v(-3, -1) * mm, "radius": 0.15 * mm});
            skCircle(sketch, "E11.12.11.0", {"center": v(-3, -2) * mm, "radius": 0.15 * mm});
            skCircle(sketch, "E11.12.12.0", {"center": v(-3, -3) * mm, "radius": 0.15 * mm});
            skCircle(sketch, "E11.12.13.0", {"center": v(-3, -4) * mm, "radius": 0.15 * mm});
            skCircle(sketch, "E11.12.14.0", {"center": v(-3, -5) * mm, "radius": 0.15 * mm});
            skCircle(sketch, "E11.12.15.0", {"center": v(-3, -6) * mm, "radius": 0.15 * mm});
            skCircle(sketch, "E11.12.16.0", {"center": v(-3, -7) * mm, "radius": 0.15 * mm});
            skCircle(sketch, "E11.12.17.0", {"center": v(-3, -8) * mm, "radius": 0.15 * mm});
            skCircle(sketch, "E11.12.18.0", {"center": v(-3, -9) * mm, "radius": 0.15 * mm});
            skCircle(sketch, "E11.12.19.0", {"center": v(-3, -10) * mm, "radius": 0.15 * mm});
            skCircle(sketch, "E11.13.0.0", {"center": v(-4, 9) * mm, "radius": 0.15 * mm});
            skCircle(sketch, "E11.13.1.0", {"center": v(-4, 8) * mm, "radius": 0.15 * mm});
            skCircle(sketch, "E11.13.2.0", {"center": v(-4, 7) * mm, "radius": 0.15 * mm});
            skCircle(sketch, "E11.13.3.0", {"center": v(-4, 6) * mm, "radius": 0.15 * mm});
            skCircle(sketch, "E11.13.4.0", {"center": v(-4, 5) * mm, "radius": 0.15 * mm});
            skCircle(sketch, "E11.13.5.0", {"center": v(-4, 4) * mm, "radius": 0.15 * mm});
            skCircle(sketch, "E11.13.6.0", {"center": v(-4, 3) * mm, "radius": 0.15 * mm});
            skCircle(sketch, "E11.13.7.0", {"center": v(-4, 2) * mm, "radius": 0.15 * mm});
            skCircle(sketch, "E11.13.8.0", {"center": v(-4, 1) * mm, "radius": 0.15 * mm});
            skCircle(sketch, "E11.13.9.0", {"center": v(-4, 0) * mm, "radius": 0.15 * mm});
            skCircle(sketch, "E11.13.10.0", {"center": v(-4, -1) * mm, "radius": 0.15 * mm});
            skCircle(sketch, "E11.13.11.0", {"center": v(-4, -2) * mm, "radius": 0.15 * mm});
            skCircle(sketch, "E11.13.12.0", {"center": v(-4, -3) * mm, "radius": 0.15 * mm});
            skCircle(sketch, "E11.13.13.0", {"center": v(-4, -4) * mm, "radius": 0.15 * mm});
            skCircle(sketch, "E11.13.14.0", {"center": v(-4, -5) * mm, "radius": 0.15 * mm});
            skCircle(sketch, "E11.13.15.0", {"center": v(-4, -6) * mm, "radius": 0.15 * mm});
            skCircle(sketch, "E11.13.16.0", {"center": v(-4, -7) * mm, "radius": 0.15 * mm});
            skCircle(sketch, "E11.13.17.0", {"center": v(-4, -8) * mm, "radius": 0.15 * mm});
            skCircle(sketch, "E11.13.18.0", {"center": v(-4, -9) * mm, "radius": 0.15 * mm});
            skCircle(sketch, "E11.13.19.0", {"center": v(-4, -10) * mm, "radius": 0.15 * mm});
            skCircle(sketch, "E11.14.0.0", {"center": v(-5, 9) * mm, "radius": 0.15 * mm});
            skCircle(sketch, "E11.14.1.0", {"center": v(-5, 8) * mm, "radius": 0.15 * mm});
            skCircle(sketch, "E11.14.2.0", {"center": v(-5, 7) * mm, "radius": 0.15 * mm});
            skCircle(sketch, "E11.14.3.0", {"center": v(-5, 6) * mm, "radius": 0.15 * mm});
            skCircle(sketch, "E11.14.4.0", {"center": v(-5, 5) * mm, "radius": 0.15 * mm});
            skCircle(sketch, "E11.14.5.0", {"center": v(-5, 4) * mm, "radius": 0.15 * mm});
            skCircle(sketch, "E11.14.6.0", {"center": v(-5, 3) * mm, "radius": 0.15 * mm});
            skCircle(sketch, "E11.14.7.0", {"center": v(-5, 2) * mm, "radius": 0.15 * mm});
            skCircle(sketch, "E11.14.8.0", {"center": v(-5, 1) * mm, "radius": 0.15 * mm});
            skCircle(sketch, "E11.14.9.0", {"center": v(-5, 0) * mm, "radius": 0.15 * mm});
            skCircle(sketch, "E11.14.10.0", {"center": v(-5, -1) * mm, "radius": 0.15 * mm});
            skCircle(sketch, "E11.14.11.0", {"center": v(-5, -2) * mm, "radius": 0.15 * mm});
            skCircle(sketch, "E11.14.12.0", {"center": v(-5, -3) * mm, "radius": 0.15 * mm});
            skCircle(sketch, "E11.14.13.0", {"center": v(-5, -4) * mm, "radius": 0.15 * mm});
            skCircle(sketch, "E11.14.14.0", {"center": v(-5, -5) * mm, "radius": 0.15 * mm});
            skCircle(sketch, "E11.14.15.0", {"center": v(-5, -6) * mm, "radius": 0.15 * mm});
            skCircle(sketch, "E11.14.16.0", {"center": v(-5, -7) * mm, "radius": 0.15 * mm});
            skCircle(sketch, "E11.14.17.0", {"center": v(-5, -8) * mm, "radius": 0.15 * mm});
            skCircle(sketch, "E11.14.18.0", {"center": v(-5, -9) * mm, "radius": 0.15 * mm});
            skCircle(sketch, "E11.14.19.0", {"center": v(-5, -10) * mm, "radius": 0.15 * mm});
            skCircle(sketch, "E11.15.0.0", {"center": v(-6, 9) * mm, "radius": 0.15 * mm});
            skCircle(sketch, "E11.15.1.0", {"center": v(-6, 8) * mm, "radius": 0.15 * mm});
            skCircle(sketch, "E11.15.2.0", {"center": v(-6, 7) * mm, "radius": 0.15 * mm});
            skCircle(sketch, "E11.15.3.0", {"center": v(-6, 6) * mm, "radius": 0.15 * mm});
            skCircle(sketch, "E11.15.4.0", {"center": v(-6, 5) * mm, "radius": 0.15 * mm});
            skCircle(sketch, "E11.15.5.0", {"center": v(-6, 4) * mm, "radius": 0.15 * mm});
            skCircle(sketch, "E11.15.6.0", {"center": v(-6, 3) * mm, "radius": 0.15 * mm});
            skCircle(sketch, "E11.15.7.0", {"center": v(-6, 2) * mm, "radius": 0.15 * mm});
            skCircle(sketch, "E11.15.8.0", {"center": v(-6, 1) * mm, "radius": 0.15 * mm});
            skCircle(sketch, "E11.15.9.0", {"center": v(-6, 0) * mm, "radius": 0.15 * mm});
            skCircle(sketch, "E11.15.10.0", {"center": v(-6, -1) * mm, "radius": 0.15 * mm});
            skCircle(sketch, "E11.15.11.0", {"center": v(-6, -2) * mm, "radius": 0.15 * mm});
            skCircle(sketch, "E11.15.12.0", {"center": v(-6, -3) * mm, "radius": 0.15 * mm});
            skCircle(sketch, "E11.15.13.0", {"center": v(-6, -4) * mm, "radius": 0.15 * mm});
            skCircle(sketch, "E11.15.14.0", {"center": v(-6, -5) * mm, "radius": 0.15 * mm});
            skCircle(sketch, "E11.15.15.0", {"center": v(-6, -6) * mm, "radius": 0.15 * mm});
            skCircle(sketch, "E11.15.16.0", {"center": v(-6, -7) * mm, "radius": 0.15 * mm});
            skCircle(sketch, "E11.15.17.0", {"center": v(-6, -8) * mm, "radius": 0.15 * mm});
            skCircle(sketch, "E11.15.18.0", {"center": v(-6, -9) * mm, "radius": 0.15 * mm});
            skCircle(sketch, "E11.15.19.0", {"center": v(-6, -10) * mm, "radius": 0.15 * mm});
            skCircle(sketch, "E11.16.0.0", {"center": v(-7, 9) * mm, "radius": 0.15 * mm});
            skCircle(sketch, "E11.16.1.0", {"center": v(-7, 8) * mm, "radius": 0.15 * mm});
            skCircle(sketch, "E11.16.2.0", {"center": v(-7, 7) * mm, "radius": 0.15 * mm});
            skCircle(sketch, "E11.16.3.0", {"center": v(-7, 6) * mm, "radius": 0.15 * mm});
            skCircle(sketch, "E11.16.4.0", {"center": v(-7, 5) * mm, "radius": 0.15 * mm});
            skCircle(sketch, "E11.16.5.0", {"center": v(-7, 4) * mm, "radius": 0.15 * mm});
            skCircle(sketch, "E11.16.6.0", {"center": v(-7, 3) * mm, "radius": 0.15 * mm});
            skCircle(sketch, "E11.16.7.0", {"center": v(-7, 2) * mm, "radius": 0.15 * mm});
            skCircle(sketch, "E11.16.8.0", {"center": v(-7, 1) * mm, "radius": 0.15 * mm});
            skCircle(sketch, "E11.16.9.0", {"center": v(-7, 0) * mm, "radius": 0.15 * mm});
            skCircle(sketch, "E11.16.10.0", {"center": v(-7, -1) * mm, "radius": 0.15 * mm});
            skCircle(sketch, "E11.16.11.0", {"center": v(-7, -2) * mm, "radius": 0.15 * mm});
            skCircle(sketch, "E11.16.12.0", {"center": v(-7, -3) * mm, "radius": 0.15 * mm});
            skCircle(sketch, "E11.16.13.0", {"center": v(-7, -4) * mm, "radius": 0.15 * mm});
            skCircle(sketch, "E11.16.14.0", {"center": v(-7, -5) * mm, "radius": 0.15 * mm});
            skCircle(sketch, "E11.16.15.0", {"center": v(-7, -6) * mm, "radius": 0.15 * mm});
            skCircle(sketch, "E11.16.16.0", {"center": v(-7, -7) * mm, "radius": 0.15 * mm});
            skCircle(sketch, "E11.16.17.0", {"center": v(-7, -8) * mm, "radius": 0.15 * mm});
            skCircle(sketch, "E11.16.18.0", {"center": v(-7, -9) * mm, "radius": 0.15 * mm});
            skCircle(sketch, "E11.16.19.0", {"center": v(-7, -10) * mm, "radius": 0.15 * mm});
            skCircle(sketch, "E11.17.0.0", {"center": v(-8, 9) * mm, "radius": 0.15 * mm});
            skCircle(sketch, "E11.17.1.0", {"center": v(-8, 8) * mm, "radius": 0.15 * mm});
            skCircle(sketch, "E11.17.2.0", {"center": v(-8, 7) * mm, "radius": 0.15 * mm});
            skCircle(sketch, "E11.17.3.0", {"center": v(-8, 6) * mm, "radius": 0.15 * mm});
            skCircle(sketch, "E11.17.4.0", {"center": v(-8, 5) * mm, "radius": 0.15 * mm});
            skCircle(sketch, "E11.17.5.0", {"center": v(-8, 4) * mm, "radius": 0.15 * mm});
            skCircle(sketch, "E11.17.6.0", {"center": v(-8, 3) * mm, "radius": 0.15 * mm});
            skCircle(sketch, "E11.17.7.0", {"center": v(-8, 2) * mm, "radius": 0.15 * mm});
            skCircle(sketch, "E11.17.8.0", {"center": v(-8, 1) * mm, "radius": 0.15 * mm});
            skCircle(sketch, "E11.17.9.0", {"center": v(-8, 0) * mm, "radius": 0.15 * mm});
            skCircle(sketch, "E11.17.10.0", {"center": v(-8, -1) * mm, "radius": 0.15 * mm});
            skCircle(sketch, "E11.17.11.0", {"center": v(-8, -2) * mm, "radius": 0.15 * mm});
            skCircle(sketch, "E11.17.12.0", {"center": v(-8, -3) * mm, "radius": 0.15 * mm});
            skCircle(sketch, "E11.17.13.0", {"center": v(-8, -4) * mm, "radius": 0.15 * mm});
            skCircle(sketch, "E11.17.14.0", {"center": v(-8, -5) * mm, "radius": 0.15 * mm});
            skCircle(sketch, "E11.17.15.0", {"center": v(-8, -6) * mm, "radius": 0.15 * mm});
            skCircle(sketch, "E11.17.16.0", {"center": v(-8, -7) * mm, "radius": 0.15 * mm});
            skCircle(sketch, "E11.17.17.0", {"center": v(-8, -8) * mm, "radius": 0.15 * mm});
            skCircle(sketch, "E11.17.18.0", {"center": v(-8, -9) * mm, "radius": 0.15 * mm});
            skCircle(sketch, "E11.17.19.0", {"center": v(-8, -10) * mm, "radius": 0.15 * mm});
            skCircle(sketch, "E11.18.0.0", {"center": v(-9, 9) * mm, "radius": 0.15 * mm});
            skCircle(sketch, "E11.18.1.0", {"center": v(-9, 8) * mm, "radius": 0.15 * mm});
            skCircle(sketch, "E11.18.2.0", {"center": v(-9, 7) * mm, "radius": 0.15 * mm});
            skCircle(sketch, "E11.18.3.0", {"center": v(-9, 6) * mm, "radius": 0.15 * mm});
            skCircle(sketch, "E11.18.4.0", {"center": v(-9, 5) * mm, "radius": 0.15 * mm});
            skCircle(sketch, "E11.18.5.0", {"center": v(-9, 4) * mm, "radius": 0.15 * mm});
            skCircle(sketch, "E11.18.6.0", {"center": v(-9, 3) * mm, "radius": 0.15 * mm});
            skCircle(sketch, "E11.18.7.0", {"center": v(-9, 2) * mm, "radius": 0.15 * mm});
            skCircle(sketch, "E11.18.8.0", {"center": v(-9, 1) * mm, "radius": 0.15 * mm});
            skCircle(sketch, "E11.18.9.0", {"center": v(-9, 0) * mm, "radius": 0.15 * mm});
            skCircle(sketch, "E11.18.10.0", {"center": v(-9, -1) * mm, "radius": 0.15 * mm});
            skCircle(sketch, "E11.18.11.0", {"center": v(-9, -2) * mm, "radius": 0.15 * mm});
            skCircle(sketch, "E11.18.12.0", {"center": v(-9, -3) * mm, "radius": 0.15 * mm});
            skCircle(sketch, "E11.18.13.0", {"center": v(-9, -4) * mm, "radius": 0.15 * mm});
            skCircle(sketch, "E11.18.14.0", {"center": v(-9, -5) * mm, "radius": 0.15 * mm});
            skCircle(sketch, "E11.18.15.0", {"center": v(-9, -6) * mm, "radius": 0.15 * mm});
            skCircle(sketch, "E11.18.16.0", {"center": v(-9, -7) * mm, "radius": 0.15 * mm});
            skCircle(sketch, "E11.18.17.0", {"center": v(-9, -8) * mm, "radius": 0.15 * mm});
            skCircle(sketch, "E11.18.18.0", {"center": v(-9, -9) * mm, "radius": 0.15 * mm});
            skCircle(sketch, "E11.18.19.0", {"center": v(-9, -10) * mm, "radius": 0.15 * mm});
            skCircle(sketch, "E11.19.0.0", {"center": v(-10, 9) * mm, "radius": 0.15 * mm});
            skCircle(sketch, "E11.19.1.0", {"center": v(-10, 8) * mm, "radius": 0.15 * mm});
            skCircle(sketch, "E11.19.2.0", {"center": v(-10, 7) * mm, "radius": 0.15 * mm});
            skCircle(sketch, "E11.19.3.0", {"center": v(-10, 6) * mm, "radius": 0.15 * mm});
            skCircle(sketch, "E11.19.4.0", {"center": v(-10, 5) * mm, "radius": 0.15 * mm});
            skCircle(sketch, "E11.19.5.0", {"center": v(-10, 4) * mm, "radius": 0.15 * mm});
            skCircle(sketch, "E11.19.6.0", {"center": v(-10, 3) * mm, "radius": 0.15 * mm});
            skCircle(sketch, "E11.19.7.0", {"center": v(-10, 2) * mm, "radius": 0.15 * mm});
            skCircle(sketch, "E11.19.8.0", {"center": v(-10, 1) * mm, "radius": 0.15 * mm});
            skCircle(sketch, "E11.19.9.0", {"center": v(-10, 0) * mm, "radius": 0.15 * mm});
            skCircle(sketch, "E11.19.10.0", {"center": v(-10, -1) * mm, "radius": 0.15 * mm});
            skCircle(sketch, "E11.19.11.0", {"center": v(-10, -2) * mm, "radius": 0.15 * mm});
            skCircle(sketch, "E11.19.12.0", {"center": v(-10, -3) * mm, "radius": 0.15 * mm});
            skCircle(sketch, "E11.19.13.0", {"center": v(-10, -4) * mm, "radius": 0.15 * mm});
            skCircle(sketch, "E11.19.14.0", {"center": v(-10, -5) * mm, "radius": 0.15 * mm});
            skCircle(sketch, "E11.19.15.0", {"center": v(-10, -6) * mm, "radius": 0.15 * mm});
            skCircle(sketch, "E11.19.16.0", {"center": v(-10, -7) * mm, "radius": 0.15 * mm});
            skCircle(sketch, "E11.19.17.0", {"center": v(-10, -8) * mm, "radius": 0.15 * mm});
            skCircle(sketch, "E11.19.18.0", {"center": v(-10, -9) * mm, "radius": 0.15 * mm});
            skCircle(sketch, "E11.19.19.0", {"center": v(-10, -10) * mm, "radius": 0.15 * mm});
            skLineSegment(sketch, "E11.direction1", {"start": v(9, 9) * mm, "end": v(8, 9) * mm, "construction": true});
            skLineSegment(sketch, "E11.direction2", {"start": v(9, 9) * mm, "end": v(9, 8) * mm, "construction": true});
            skCircle(sketch, "E12.1.0.0", {"center": v(10, 9) * mm, "radius": 0.15 * mm});
            skCircle(sketch, "E12.1.1.0", {"center": v(10, 8) * mm, "radius": 0.15 * mm});
            skCircle(sketch, "E12.1.2.0", {"center": v(10, 7) * mm, "radius": 0.15 * mm});
            skCircle(sketch, "E12.1.3.0", {"center": v(10, 6) * mm, "radius": 0.15 * mm});
            skCircle(sketch, "E12.1.4.0", {"center": v(10, 5) * mm, "radius": 0.15 * mm});
            skCircle(sketch, "E12.1.5.0", {"center": v(10, 4) * mm, "radius": 0.15 * mm});
            skCircle(sketch, "E12.1.6.0", {"center": v(10, 3) * mm, "radius": 0.15 * mm});
            skCircle(sketch, "E12.1.7.0", {"center": v(10, 2) * mm, "radius": 0.15 * mm});
            skCircle(sketch, "E12.1.8.0", {"center": v(10, 1) * mm, "radius": 0.15 * mm});
            skCircle(sketch, "E12.1.9.0", {"center": v(10, 0) * mm, "radius": 0.15 * mm});
            skCircle(sketch, "E12.1.10.0", {"center": v(10, -1) * mm, "radius": 0.15 * mm});
            skCircle(sketch, "E12.1.11.0", {"center": v(10, -2) * mm, "radius": 0.15 * mm});
            skCircle(sketch, "E12.1.12.0", {"center": v(10, -3) * mm, "radius": 0.15 * mm});
            skCircle(sketch, "E12.1.13.0", {"center": v(10, -4) * mm, "radius": 0.15 * mm});
            skCircle(sketch, "E12.1.14.0", {"center": v(10, -5) * mm, "radius": 0.15 * mm});
            skCircle(sketch, "E12.1.15.0", {"center": v(10, -6) * mm, "radius": 0.15 * mm});
            skCircle(sketch, "E12.1.16.0", {"center": v(10, -7) * mm, "radius": 0.15 * mm});
            skCircle(sketch, "E12.1.17.0", {"center": v(10, -8) * mm, "radius": 0.15 * mm});
            skCircle(sketch, "E12.1.18.0", {"center": v(10, -9) * mm, "radius": 0.15 * mm});
            skCircle(sketch, "E12.1.19.0", {"center": v(10, -10) * mm, "radius": 0.15 * mm});
            skCircle(sketch, "E12.2.0.0", {"center": v(11, 9) * mm, "radius": 0.15 * mm});
            skCircle(sketch, "E12.2.1.0", {"center": v(11, 8) * mm, "radius": 0.15 * mm});
            skCircle(sketch, "E12.2.2.0", {"center": v(11, 7) * mm, "radius": 0.15 * mm});
            skCircle(sketch, "E12.2.3.0", {"center": v(11, 6) * mm, "radius": 0.15 * mm});
            skCircle(sketch, "E12.2.4.0", {"center": v(11, 5) * mm, "radius": 0.15 * mm});
            skCircle(sketch, "E12.2.5.0", {"center": v(11, 4) * mm, "radius": 0.15 * mm});
            skCircle(sketch, "E12.2.6.0", {"center": v(11, 3) * mm, "radius": 0.15 * mm});
            skCircle(sketch, "E12.2.7.0", {"center": v(11, 2) * mm, "radius": 0.15 * mm});
            skCircle(sketch, "E12.2.8.0", {"center": v(11, 1) * mm, "radius": 0.15 * mm});
            skCircle(sketch, "E12.2.9.0", {"center": v(11, 0) * mm, "radius": 0.15 * mm});
            skCircle(sketch, "E12.2.10.0", {"center": v(11, -1) * mm, "radius": 0.15 * mm});
            skCircle(sketch, "E12.2.11.0", {"center": v(11, -2) * mm, "radius": 0.15 * mm});
            skCircle(sketch, "E12.2.12.0", {"center": v(11, -3) * mm, "radius": 0.15 * mm});
            skCircle(sketch, "E12.2.13.0", {"center": v(11, -4) * mm, "radius": 0.15 * mm});
            skCircle(sketch, "E12.2.14.0", {"center": v(11, -5) * mm, "radius": 0.15 * mm});
            skCircle(sketch, "E12.2.15.0", {"center": v(11, -6) * mm, "radius": 0.15 * mm});
            skCircle(sketch, "E12.2.16.0", {"center": v(11, -7) * mm, "radius": 0.15 * mm});
            skCircle(sketch, "E12.2.17.0", {"center": v(11, -8) * mm, "radius": 0.15 * mm});
            skCircle(sketch, "E12.2.18.0", {"center": v(11, -9) * mm, "radius": 0.15 * mm});
            skCircle(sketch, "E12.2.19.0", {"center": v(11, -10) * mm, "radius": 0.15 * mm});
            skCircle(sketch, "E12.3.0.0", {"center": v(12, 9) * mm, "radius": 0.15 * mm});
            skCircle(sketch, "E12.3.1.0", {"center": v(12, 8) * mm, "radius": 0.15 * mm});
            skCircle(sketch, "E12.3.2.0", {"center": v(12, 7) * mm, "radius": 0.15 * mm});
            skCircle(sketch, "E12.3.3.0", {"center": v(12, 6) * mm, "radius": 0.15 * mm});
            skCircle(sketch, "E12.3.4.0", {"center": v(12, 5) * mm, "radius": 0.15 * mm});
            skCircle(sketch, "E12.3.5.0", {"center": v(12, 4) * mm, "radius": 0.15 * mm});
            skCircle(sketch, "E12.3.6.0", {"center": v(12, 3) * mm, "radius": 0.15 * mm});
            skCircle(sketch, "E12.3.7.0", {"center": v(12, 2) * mm, "radius": 0.15 * mm});
            skCircle(sketch, "E12.3.8.0", {"center": v(12, 1) * mm, "radius": 0.15 * mm});
            skCircle(sketch, "E12.3.9.0", {"center": v(12, 0) * mm, "radius": 0.15 * mm});
            skCircle(sketch, "E12.3.10.0", {"center": v(12, -1) * mm, "radius": 0.15 * mm});
            skCircle(sketch, "E12.3.11.0", {"center": v(12, -2) * mm, "radius": 0.15 * mm});
            skCircle(sketch, "E12.3.12.0", {"center": v(12, -3) * mm, "radius": 0.15 * mm});
            skCircle(sketch, "E12.3.13.0", {"center": v(12, -4) * mm, "radius": 0.15 * mm});
            skCircle(sketch, "E12.3.14.0", {"center": v(12, -5) * mm, "radius": 0.15 * mm});
            skCircle(sketch, "E12.3.15.0", {"center": v(12, -6) * mm, "radius": 0.15 * mm});
            skCircle(sketch, "E12.3.16.0", {"center": v(12, -7) * mm, "radius": 0.15 * mm});
            skCircle(sketch, "E12.3.17.0", {"center": v(12, -8) * mm, "radius": 0.15 * mm});
            skCircle(sketch, "E12.3.18.0", {"center": v(12, -9) * mm, "radius": 0.15 * mm});
            skCircle(sketch, "E12.3.19.0", {"center": v(12, -10) * mm, "radius": 0.15 * mm});
            skCircle(sketch, "E12.4.0.0", {"center": v(13, 9) * mm, "radius": 0.15 * mm});
            skCircle(sketch, "E12.4.1.0", {"center": v(13, 8) * mm, "radius": 0.15 * mm});
            skCircle(sketch, "E12.4.2.0", {"center": v(13, 7) * mm, "radius": 0.15 * mm});
            skCircle(sketch, "E12.4.3.0", {"center": v(13, 6) * mm, "radius": 0.15 * mm});
            skCircle(sketch, "E12.4.4.0", {"center": v(13, 5) * mm, "radius": 0.15 * mm});
            skCircle(sketch, "E12.4.5.0", {"center": v(13, 4) * mm, "radius": 0.15 * mm});
            skCircle(sketch, "E12.4.6.0", {"center": v(13, 3) * mm, "radius": 0.15 * mm});
            skCircle(sketch, "E12.4.7.0", {"center": v(13, 2) * mm, "radius": 0.15 * mm});
            skCircle(sketch, "E12.4.8.0", {"center": v(13, 1) * mm, "radius": 0.15 * mm});
            skCircle(sketch, "E12.4.9.0", {"center": v(13, 0) * mm, "radius": 0.15 * mm});
            skCircle(sketch, "E12.4.10.0", {"center": v(13, -1) * mm, "radius": 0.15 * mm});
            skCircle(sketch, "E12.4.11.0", {"center": v(13, -2) * mm, "radius": 0.15 * mm});
            skCircle(sketch, "E12.4.12.0", {"center": v(13, -3) * mm, "radius": 0.15 * mm});
            skCircle(sketch, "E12.4.13.0", {"center": v(13, -4) * mm, "radius": 0.15 * mm});
            skCircle(sketch, "E12.4.14.0", {"center": v(13, -5) * mm, "radius": 0.15 * mm});
            skCircle(sketch, "E12.4.15.0", {"center": v(13, -6) * mm, "radius": 0.15 * mm});
            skCircle(sketch, "E12.4.16.0", {"center": v(13, -7) * mm, "radius": 0.15 * mm});
            skCircle(sketch, "E12.4.17.0", {"center": v(13, -8) * mm, "radius": 0.15 * mm});
            skCircle(sketch, "E12.4.18.0", {"center": v(13, -9) * mm, "radius": 0.15 * mm});
            skCircle(sketch, "E12.4.19.0", {"center": v(13, -10) * mm, "radius": 0.15 * mm});
            skCircle(sketch, "E12.5.0.0", {"center": v(14, 9) * mm, "radius": 0.15 * mm});
            skCircle(sketch, "E12.5.1.0", {"center": v(14, 8) * mm, "radius": 0.15 * mm});
            skCircle(sketch, "E12.5.2.0", {"center": v(14, 7) * mm, "radius": 0.15 * mm});
            skCircle(sketch, "E12.5.3.0", {"center": v(14, 6) * mm, "radius": 0.15 * mm});
            skCircle(sketch, "E12.5.4.0", {"center": v(14, 5) * mm, "radius": 0.15 * mm});
            skCircle(sketch, "E12.5.5.0", {"center": v(14, 4) * mm, "radius": 0.15 * mm});
            skCircle(sketch, "E12.5.6.0", {"center": v(14, 3) * mm, "radius": 0.15 * mm});
            skCircle(sketch, "E12.5.7.0", {"center": v(14, 2) * mm, "radius": 0.15 * mm});
            skCircle(sketch, "E12.5.8.0", {"center": v(14, 1) * mm, "radius": 0.15 * mm});
            skCircle(sketch, "E12.5.9.0", {"center": v(14, 0) * mm, "radius": 0.15 * mm});
            skCircle(sketch, "E12.5.10.0", {"center": v(14, -1) * mm, "radius": 0.15 * mm});
            skCircle(sketch, "E12.5.11.0", {"center": v(14, -2) * mm, "radius": 0.15 * mm});
            skCircle(sketch, "E12.5.12.0", {"center": v(14, -3) * mm, "radius": 0.15 * mm});
            skCircle(sketch, "E12.5.13.0", {"center": v(14, -4) * mm, "radius": 0.15 * mm});
            skCircle(sketch, "E12.5.14.0", {"center": v(14, -5) * mm, "radius": 0.15 * mm});
            skCircle(sketch, "E12.5.15.0", {"center": v(14, -6) * mm, "radius": 0.15 * mm});
            skCircle(sketch, "E12.5.16.0", {"center": v(14, -7) * mm, "radius": 0.15 * mm});
            skCircle(sketch, "E12.5.17.0", {"center": v(14, -8) * mm, "radius": 0.15 * mm});
            skCircle(sketch, "E12.5.18.0", {"center": v(14, -9) * mm, "radius": 0.15 * mm});
            skCircle(sketch, "E12.5.19.0", {"center": v(14, -10) * mm, "radius": 0.15 * mm});
            skCircle(sketch, "E12.6.0.0", {"center": v(15, 9) * mm, "radius": 0.15 * mm});
            skCircle(sketch, "E12.6.1.0", {"center": v(15, 8) * mm, "radius": 0.15 * mm});
            skCircle(sketch, "E12.6.2.0", {"center": v(15, 7) * mm, "radius": 0.15 * mm});
            skCircle(sketch, "E12.6.3.0", {"center": v(15, 6) * mm, "radius": 0.15 * mm});
            skCircle(sketch, "E12.6.4.0", {"center": v(15, 5) * mm, "radius": 0.15 * mm});
            skCircle(sketch, "E12.6.5.0", {"center": v(15, 4) * mm, "radius": 0.15 * mm});
            skCircle(sketch, "E12.6.6.0", {"center": v(15, 3) * mm, "radius": 0.15 * mm});
            skCircle(sketch, "E12.6.7.0", {"center": v(15, 2) * mm, "radius": 0.15 * mm});
            skCircle(sketch, "E12.6.8.0", {"center": v(15, 1) * mm, "radius": 0.15 * mm});
            skCircle(sketch, "E12.6.9.0", {"center": v(15, 0) * mm, "radius": 0.15 * mm});
            skCircle(sketch, "E12.6.10.0", {"center": v(15, -1) * mm, "radius": 0.15 * mm});
            skCircle(sketch, "E12.6.11.0", {"center": v(15, -2) * mm, "radius": 0.15 * mm});
            skCircle(sketch, "E12.6.12.0", {"center": v(15, -3) * mm, "radius": 0.15 * mm});
            skCircle(sketch, "E12.6.13.0", {"center": v(15, -4) * mm, "radius": 0.15 * mm});
            skCircle(sketch, "E12.6.14.0", {"center": v(15, -5) * mm, "radius": 0.15 * mm});
            skCircle(sketch, "E12.6.15.0", {"center": v(15, -6) * mm, "radius": 0.15 * mm});
            skCircle(sketch, "E12.6.16.0", {"center": v(15, -7) * mm, "radius": 0.15 * mm});
            skCircle(sketch, "E12.6.17.0", {"center": v(15, -8) * mm, "radius": 0.15 * mm});
            skCircle(sketch, "E12.6.18.0", {"center": v(15, -9) * mm, "radius": 0.15 * mm});
            skCircle(sketch, "E12.6.19.0", {"center": v(15, -10) * mm, "radius": 0.15 * mm});
            skCircle(sketch, "E12.7.0.0", {"center": v(16, 9) * mm, "radius": 0.15 * mm});
            skCircle(sketch, "E12.7.1.0", {"center": v(16, 8) * mm, "radius": 0.15 * mm});
            skCircle(sketch, "E12.7.2.0", {"center": v(16, 7) * mm, "radius": 0.15 * mm});
            skCircle(sketch, "E12.7.3.0", {"center": v(16, 6) * mm, "radius": 0.15 * mm});
            skCircle(sketch, "E12.7.4.0", {"center": v(16, 5) * mm, "radius": 0.15 * mm});
            skCircle(sketch, "E12.7.5.0", {"center": v(16, 4) * mm, "radius": 0.15 * mm});
            skCircle(sketch, "E12.7.6.0", {"center": v(16, 3) * mm, "radius": 0.15 * mm});
            skCircle(sketch, "E12.7.7.0", {"center": v(16, 2) * mm, "radius": 0.15 * mm});
            skCircle(sketch, "E12.7.8.0", {"center": v(16, 1) * mm, "radius": 0.15 * mm});
            skCircle(sketch, "E12.7.9.0", {"center": v(16, 0) * mm, "radius": 0.15 * mm});
            skCircle(sketch, "E12.7.10.0", {"center": v(16, -1) * mm, "radius": 0.15 * mm});
            skCircle(sketch, "E12.7.11.0", {"center": v(16, -2) * mm, "radius": 0.15 * mm});
            skCircle(sketch, "E12.7.12.0", {"center": v(16, -3) * mm, "radius": 0.15 * mm});
            skCircle(sketch, "E12.7.13.0", {"center": v(16, -4) * mm, "radius": 0.15 * mm});
            skCircle(sketch, "E12.7.14.0", {"center": v(16, -5) * mm, "radius": 0.15 * mm});
            skCircle(sketch, "E12.7.15.0", {"center": v(16, -6) * mm, "radius": 0.15 * mm});
            skCircle(sketch, "E12.7.16.0", {"center": v(16, -7) * mm, "radius": 0.15 * mm});
            skCircle(sketch, "E12.7.17.0", {"center": v(16, -8) * mm, "radius": 0.15 * mm});
            skCircle(sketch, "E12.7.18.0", {"center": v(16, -9) * mm, "radius": 0.15 * mm});
            skCircle(sketch, "E12.7.19.0", {"center": v(16, -10) * mm, "radius": 0.15 * mm});
            skCircle(sketch, "E12.8.0.0", {"center": v(17, 9) * mm, "radius": 0.15 * mm});
            skCircle(sketch, "E12.8.1.0", {"center": v(17, 8) * mm, "radius": 0.15 * mm});
            skCircle(sketch, "E12.8.2.0", {"center": v(17, 7) * mm, "radius": 0.15 * mm});
            skCircle(sketch, "E12.8.3.0", {"center": v(17, 6) * mm, "radius": 0.15 * mm});
            skCircle(sketch, "E12.8.4.0", {"center": v(17, 5) * mm, "radius": 0.15 * mm});
            skCircle(sketch, "E12.8.5.0", {"center": v(17, 4) * mm, "radius": 0.15 * mm});
            skCircle(sketch, "E12.8.6.0", {"center": v(17, 3) * mm, "radius": 0.15 * mm});
            skCircle(sketch, "E12.8.7.0", {"center": v(17, 2) * mm, "radius": 0.15 * mm});
            skCircle(sketch, "E12.8.8.0", {"center": v(17, 1) * mm, "radius": 0.15 * mm});
            skCircle(sketch, "E12.8.9.0", {"center": v(17, 0) * mm, "radius": 0.15 * mm});
            skCircle(sketch, "E12.8.10.0", {"center": v(17, -1) * mm, "radius": 0.15 * mm});
            skCircle(sketch, "E12.8.11.0", {"center": v(17, -2) * mm, "radius": 0.15 * mm});
            skCircle(sketch, "E12.8.12.0", {"center": v(17, -3) * mm, "radius": 0.15 * mm});
            skCircle(sketch, "E12.8.13.0", {"center": v(17, -4) * mm, "radius": 0.15 * mm});
            skCircle(sketch, "E12.8.14.0", {"center": v(17, -5) * mm, "radius": 0.15 * mm});
            skCircle(sketch, "E12.8.15.0", {"center": v(17, -6) * mm, "radius": 0.15 * mm});
            skCircle(sketch, "E12.8.16.0", {"center": v(17, -7) * mm, "radius": 0.15 * mm});
            skCircle(sketch, "E12.8.17.0", {"center": v(17, -8) * mm, "radius": 0.15 * mm});
            skCircle(sketch, "E12.8.18.0", {"center": v(17, -9) * mm, "radius": 0.15 * mm});
            skCircle(sketch, "E12.8.19.0", {"center": v(17, -10) * mm, "radius": 0.15 * mm});
            skCircle(sketch, "E12.9.0.0", {"center": v(18, 9) * mm, "radius": 0.15 * mm});
            skCircle(sketch, "E12.9.1.0", {"center": v(18, 8) * mm, "radius": 0.15 * mm});
            skCircle(sketch, "E12.9.2.0", {"center": v(18, 7) * mm, "radius": 0.15 * mm});
            skCircle(sketch, "E12.9.3.0", {"center": v(18, 6) * mm, "radius": 0.15 * mm});
            skCircle(sketch, "E12.9.4.0", {"center": v(18, 5) * mm, "radius": 0.15 * mm});
            skCircle(sketch, "E12.9.5.0", {"center": v(18, 4) * mm, "radius": 0.15 * mm});
            skCircle(sketch, "E12.9.6.0", {"center": v(18, 3) * mm, "radius": 0.15 * mm});
            skCircle(sketch, "E12.9.7.0", {"center": v(18, 2) * mm, "radius": 0.15 * mm});
            skCircle(sketch, "E12.9.8.0", {"center": v(18, 1) * mm, "radius": 0.15 * mm});
            skCircle(sketch, "E12.9.9.0", {"center": v(18, 0) * mm, "radius": 0.15 * mm});
            skCircle(sketch, "E12.9.10.0", {"center": v(18, -1) * mm, "radius": 0.15 * mm});
            skCircle(sketch, "E12.9.11.0", {"center": v(18, -2) * mm, "radius": 0.15 * mm});
            skCircle(sketch, "E12.9.12.0", {"center": v(18, -3) * mm, "radius": 0.15 * mm});
            skCircle(sketch, "E12.9.13.0", {"center": v(18, -4) * mm, "radius": 0.15 * mm});
            skCircle(sketch, "E12.9.14.0", {"center": v(18, -5) * mm, "radius": 0.15 * mm});
            skCircle(sketch, "E12.9.15.0", {"center": v(18, -6) * mm, "radius": 0.15 * mm});
            skCircle(sketch, "E12.9.16.0", {"center": v(18, -7) * mm, "radius": 0.15 * mm});
            skCircle(sketch, "E12.9.17.0", {"center": v(18, -8) * mm, "radius": 0.15 * mm});
            skCircle(sketch, "E12.9.18.0", {"center": v(18, -9) * mm, "radius": 0.15 * mm});
            skCircle(sketch, "E12.9.19.0", {"center": v(18, -10) * mm, "radius": 0.15 * mm});
            skCircle(sketch, "E12.10.0.0", {"center": v(19, 9) * mm, "radius": 0.15 * mm});
            skCircle(sketch, "E12.10.1.0", {"center": v(19, 8) * mm, "radius": 0.15 * mm});
            skCircle(sketch, "E12.10.2.0", {"center": v(19, 7) * mm, "radius": 0.15 * mm});
            skCircle(sketch, "E12.10.3.0", {"center": v(19, 6) * mm, "radius": 0.15 * mm});
            skCircle(sketch, "E12.10.4.0", {"center": v(19, 5) * mm, "radius": 0.15 * mm});
            skCircle(sketch, "E12.10.5.0", {"center": v(19, 4) * mm, "radius": 0.15 * mm});
            skCircle(sketch, "E12.10.6.0", {"center": v(19, 3) * mm, "radius": 0.15 * mm});
            skCircle(sketch, "E12.10.7.0", {"center": v(19, 2) * mm, "radius": 0.15 * mm});
            skCircle(sketch, "E12.10.8.0", {"center": v(19, 1) * mm, "radius": 0.15 * mm});
            skCircle(sketch, "E12.10.9.0", {"center": v(19, 0) * mm, "radius": 0.15 * mm});
            skCircle(sketch, "E12.10.10.0", {"center": v(19, -1) * mm, "radius": 0.15 * mm});
            skCircle(sketch, "E12.10.11.0", {"center": v(19, -2) * mm, "radius": 0.15 * mm});
            skCircle(sketch, "E12.10.12.0", {"center": v(19, -3) * mm, "radius": 0.15 * mm});
            skCircle(sketch, "E12.10.13.0", {"center": v(19, -4) * mm, "radius": 0.15 * mm});
            skCircle(sketch, "E12.10.14.0", {"center": v(19, -5) * mm, "radius": 0.15 * mm});
            skCircle(sketch, "E12.10.15.0", {"center": v(19, -6) * mm, "radius": 0.15 * mm});
            skCircle(sketch, "E12.10.16.0", {"center": v(19, -7) * mm, "radius": 0.15 * mm});
            skCircle(sketch, "E12.10.17.0", {"center": v(19, -8) * mm, "radius": 0.15 * mm});
            skCircle(sketch, "E12.10.18.0", {"center": v(19, -9) * mm, "radius": 0.15 * mm});
            skCircle(sketch, "E12.10.19.0", {"center": v(19, -10) * mm, "radius": 0.15 * mm});
            skCircle(sketch, "E12.11.0.0", {"center": v(20, 9) * mm, "radius": 0.15 * mm});
            skCircle(sketch, "E12.11.1.0", {"center": v(20, 8) * mm, "radius": 0.15 * mm});
            skCircle(sketch, "E12.11.2.0", {"center": v(20, 7) * mm, "radius": 0.15 * mm});
            skCircle(sketch, "E12.11.3.0", {"center": v(20, 6) * mm, "radius": 0.15 * mm});
            skCircle(sketch, "E12.11.4.0", {"center": v(20, 5) * mm, "radius": 0.15 * mm});
            skCircle(sketch, "E12.11.5.0", {"center": v(20, 4) * mm, "radius": 0.15 * mm});
            skCircle(sketch, "E12.11.6.0", {"center": v(20, 3) * mm, "radius": 0.15 * mm});
            skCircle(sketch, "E12.11.7.0", {"center": v(20, 2) * mm, "radius": 0.15 * mm});
            skCircle(sketch, "E12.11.8.0", {"center": v(20, 1) * mm, "radius": 0.15 * mm});
            skCircle(sketch, "E12.11.9.0", {"center": v(20, 0) * mm, "radius": 0.15 * mm});
            skCircle(sketch, "E12.11.10.0", {"center": v(20, -1) * mm, "radius": 0.15 * mm});
            skCircle(sketch, "E12.11.11.0", {"center": v(20, -2) * mm, "radius": 0.15 * mm});
            skCircle(sketch, "E12.11.12.0", {"center": v(20, -3) * mm, "radius": 0.15 * mm});
            skCircle(sketch, "E12.11.13.0", {"center": v(20, -4) * mm, "radius": 0.15 * mm});
            skCircle(sketch, "E12.11.14.0", {"center": v(20, -5) * mm, "radius": 0.15 * mm});
            skCircle(sketch, "E12.11.15.0", {"center": v(20, -6) * mm, "radius": 0.15 * mm});
            skCircle(sketch, "E12.11.16.0", {"center": v(20, -7) * mm, "radius": 0.15 * mm});
            skCircle(sketch, "E12.11.17.0", {"center": v(20, -8) * mm, "radius": 0.15 * mm});
            skCircle(sketch, "E12.11.18.0", {"center": v(20, -9) * mm, "radius": 0.15 * mm});
            skCircle(sketch, "E12.11.19.0", {"center": v(20, -10) * mm, "radius": 0.15 * mm});
            skCircle(sketch, "E12.12.0.0", {"center": v(21, 9) * mm, "radius": 0.15 * mm});
            skCircle(sketch, "E12.12.1.0", {"center": v(21, 8) * mm, "radius": 0.15 * mm});
            skCircle(sketch, "E12.12.2.0", {"center": v(21, 7) * mm, "radius": 0.15 * mm});
            skCircle(sketch, "E12.12.3.0", {"center": v(21, 6) * mm, "radius": 0.15 * mm});
            skCircle(sketch, "E12.12.4.0", {"center": v(21, 5) * mm, "radius": 0.15 * mm});
            skCircle(sketch, "E12.12.5.0", {"center": v(21, 4) * mm, "radius": 0.15 * mm});
            skCircle(sketch, "E12.12.6.0", {"center": v(21, 3) * mm, "radius": 0.15 * mm});
            skCircle(sketch, "E12.12.7.0", {"center": v(21, 2) * mm, "radius": 0.15 * mm});
            skCircle(sketch, "E12.12.8.0", {"center": v(21, 1) * mm, "radius": 0.15 * mm});
            skCircle(sketch, "E12.12.9.0", {"center": v(21, 0) * mm, "radius": 0.15 * mm});
            skCircle(sketch, "E12.12.10.0", {"center": v(21, -1) * mm, "radius": 0.15 * mm});
            skCircle(sketch, "E12.12.11.0", {"center": v(21, -2) * mm, "radius": 0.15 * mm});
            skCircle(sketch, "E12.12.12.0", {"center": v(21, -3) * mm, "radius": 0.15 * mm});
            skCircle(sketch, "E12.12.13.0", {"center": v(21, -4) * mm, "radius": 0.15 * mm});
            skCircle(sketch, "E12.12.14.0", {"center": v(21, -5) * mm, "radius": 0.15 * mm});
            skCircle(sketch, "E12.12.15.0", {"center": v(21, -6) * mm, "radius": 0.15 * mm});
            skCircle(sketch, "E12.12.16.0", {"center": v(21, -7) * mm, "radius": 0.15 * mm});
            skCircle(sketch, "E12.12.17.0", {"center": v(21, -8) * mm, "radius": 0.15 * mm});
            skCircle(sketch, "E12.12.18.0", {"center": v(21, -9) * mm, "radius": 0.15 * mm});
            skCircle(sketch, "E12.12.19.0", {"center": v(21, -10) * mm, "radius": 0.15 * mm});
            skCircle(sketch, "E12.13.0.0", {"center": v(22, 9) * mm, "radius": 0.15 * mm});
            skCircle(sketch, "E12.13.1.0", {"center": v(22, 8) * mm, "radius": 0.15 * mm});
            skCircle(sketch, "E12.13.2.0", {"center": v(22, 7) * mm, "radius": 0.15 * mm});
            skCircle(sketch, "E12.13.3.0", {"center": v(22, 6) * mm, "radius": 0.15 * mm});
            skCircle(sketch, "E12.13.4.0", {"center": v(22, 5) * mm, "radius": 0.15 * mm});
            skCircle(sketch, "E12.13.5.0", {"center": v(22, 4) * mm, "radius": 0.15 * mm});
            skCircle(sketch, "E12.13.6.0", {"center": v(22, 3) * mm, "radius": 0.15 * mm});
            skCircle(sketch, "E12.13.7.0", {"center": v(22, 2) * mm, "radius": 0.15 * mm});
            skCircle(sketch, "E12.13.8.0", {"center": v(22, 1) * mm, "radius": 0.15 * mm});
            skCircle(sketch, "E12.13.9.0", {"center": v(22, 0) * mm, "radius": 0.15 * mm});
            skCircle(sketch, "E12.13.10.0", {"center": v(22, -1) * mm, "radius": 0.15 * mm});
            skCircle(sketch, "E12.13.11.0", {"center": v(22, -2) * mm, "radius": 0.15 * mm});
            skCircle(sketch, "E12.13.12.0", {"center": v(22, -3) * mm, "radius": 0.15 * mm});
            skCircle(sketch, "E12.13.13.0", {"center": v(22, -4) * mm, "radius": 0.15 * mm});
            skCircle(sketch, "E12.13.14.0", {"center": v(22, -5) * mm, "radius": 0.15 * mm});
            skCircle(sketch, "E12.13.15.0", {"center": v(22, -6) * mm, "radius": 0.15 * mm});
            skCircle(sketch, "E12.13.16.0", {"center": v(22, -7) * mm, "radius": 0.15 * mm});
            skCircle(sketch, "E12.13.17.0", {"center": v(22, -8) * mm, "radius": 0.15 * mm});
            skCircle(sketch, "E12.13.18.0", {"center": v(22, -9) * mm, "radius": 0.15 * mm});
            skCircle(sketch, "E12.13.19.0", {"center": v(22, -10) * mm, "radius": 0.15 * mm});
            skCircle(sketch, "E12.14.0.0", {"center": v(23, 9) * mm, "radius": 0.15 * mm});
            skCircle(sketch, "E12.14.1.0", {"center": v(23, 8) * mm, "radius": 0.15 * mm});
            skCircle(sketch, "E12.14.2.0", {"center": v(23, 7) * mm, "radius": 0.15 * mm});
            skCircle(sketch, "E12.14.3.0", {"center": v(23, 6) * mm, "radius": 0.15 * mm});
            skCircle(sketch, "E12.14.4.0", {"center": v(23, 5) * mm, "radius": 0.15 * mm});
            skCircle(sketch, "E12.14.5.0", {"center": v(23, 4) * mm, "radius": 0.15 * mm});
            skCircle(sketch, "E12.14.6.0", {"center": v(23, 3) * mm, "radius": 0.15 * mm});
            skCircle(sketch, "E12.14.7.0", {"center": v(23, 2) * mm, "radius": 0.15 * mm});
            skCircle(sketch, "E12.14.8.0", {"center": v(23, 1) * mm, "radius": 0.15 * mm});
            skCircle(sketch, "E12.14.9.0", {"center": v(23, 0) * mm, "radius": 0.15 * mm});
            skCircle(sketch, "E12.14.10.0", {"center": v(23, -1) * mm, "radius": 0.15 * mm});
            skCircle(sketch, "E12.14.11.0", {"center": v(23, -2) * mm, "radius": 0.15 * mm});
            skCircle(sketch, "E12.14.12.0", {"center": v(23, -3) * mm, "radius": 0.15 * mm});
            skCircle(sketch, "E12.14.13.0", {"center": v(23, -4) * mm, "radius": 0.15 * mm});
            skCircle(sketch, "E12.14.14.0", {"center": v(23, -5) * mm, "radius": 0.15 * mm});
            skCircle(sketch, "E12.14.15.0", {"center": v(23, -6) * mm, "radius": 0.15 * mm});
            skCircle(sketch, "E12.14.16.0", {"center": v(23, -7) * mm, "radius": 0.15 * mm});
            skCircle(sketch, "E12.14.17.0", {"center": v(23, -8) * mm, "radius": 0.15 * mm});
            skCircle(sketch, "E12.14.18.0", {"center": v(23, -9) * mm, "radius": 0.15 * mm});
            skCircle(sketch, "E12.14.19.0", {"center": v(23, -10) * mm, "radius": 0.15 * mm});
            skCircle(sketch, "E12.15.0.0", {"center": v(24, 9) * mm, "radius": 0.15 * mm});
            skCircle(sketch, "E12.15.1.0", {"center": v(24, 8) * mm, "radius": 0.15 * mm});
            skCircle(sketch, "E12.15.2.0", {"center": v(24, 7) * mm, "radius": 0.15 * mm});
            skCircle(sketch, "E12.15.3.0", {"center": v(24, 6) * mm, "radius": 0.15 * mm});
            skCircle(sketch, "E12.15.4.0", {"center": v(24, 5) * mm, "radius": 0.15 * mm});
            skCircle(sketch, "E12.15.5.0", {"center": v(24, 4) * mm, "radius": 0.15 * mm});
            skCircle(sketch, "E12.15.6.0", {"center": v(24, 3) * mm, "radius": 0.15 * mm});
            skCircle(sketch, "E12.15.7.0", {"center": v(24, 2) * mm, "radius": 0.15 * mm});
            skCircle(sketch, "E12.15.8.0", {"center": v(24, 1) * mm, "radius": 0.15 * mm});
            skCircle(sketch, "E12.15.9.0", {"center": v(24, 0) * mm, "radius": 0.15 * mm});
            skCircle(sketch, "E12.15.10.0", {"center": v(24, -1) * mm, "radius": 0.15 * mm});
            skCircle(sketch, "E12.15.11.0", {"center": v(24, -2) * mm, "radius": 0.15 * mm});
            skCircle(sketch, "E12.15.12.0", {"center": v(24, -3) * mm, "radius": 0.15 * mm});
            skCircle(sketch, "E12.15.13.0", {"center": v(24, -4) * mm, "radius": 0.15 * mm});
            skCircle(sketch, "E12.15.14.0", {"center": v(24, -5) * mm, "radius": 0.15 * mm});
            skCircle(sketch, "E12.15.15.0", {"center": v(24, -6) * mm, "radius": 0.15 * mm});
            skCircle(sketch, "E12.15.16.0", {"center": v(24, -7) * mm, "radius": 0.15 * mm});
            skCircle(sketch, "E12.15.17.0", {"center": v(24, -8) * mm, "radius": 0.15 * mm});
            skCircle(sketch, "E12.15.18.0", {"center": v(24, -9) * mm, "radius": 0.15 * mm});
            skCircle(sketch, "E12.15.19.0", {"center": v(24, -10) * mm, "radius": 0.15 * mm});
            skCircle(sketch, "E12.16.0.0", {"center": v(25, 9) * mm, "radius": 0.15 * mm});
            skCircle(sketch, "E12.16.1.0", {"center": v(25, 8) * mm, "radius": 0.15 * mm});
            skCircle(sketch, "E12.16.2.0", {"center": v(25, 7) * mm, "radius": 0.15 * mm});
            skCircle(sketch, "E12.16.3.0", {"center": v(25, 6) * mm, "radius": 0.15 * mm});
            skCircle(sketch, "E12.16.4.0", {"center": v(25, 5) * mm, "radius": 0.15 * mm});
            skCircle(sketch, "E12.16.5.0", {"center": v(25, 4) * mm, "radius": 0.15 * mm});
            skCircle(sketch, "E12.16.6.0", {"center": v(25, 3) * mm, "radius": 0.15 * mm});
            skCircle(sketch, "E12.16.7.0", {"center": v(25, 2) * mm, "radius": 0.15 * mm});
            skCircle(sketch, "E12.16.8.0", {"center": v(25, 1) * mm, "radius": 0.15 * mm});
            skCircle(sketch, "E12.16.9.0", {"center": v(25, 0) * mm, "radius": 0.15 * mm});
            skCircle(sketch, "E12.16.10.0", {"center": v(25, -1) * mm, "radius": 0.15 * mm});
            skCircle(sketch, "E12.16.11.0", {"center": v(25, -2) * mm, "radius": 0.15 * mm});
            skCircle(sketch, "E12.16.12.0", {"center": v(25, -3) * mm, "radius": 0.15 * mm});
            skCircle(sketch, "E12.16.13.0", {"center": v(25, -4) * mm, "radius": 0.15 * mm});
            skCircle(sketch, "E12.16.14.0", {"center": v(25, -5) * mm, "radius": 0.15 * mm});
            skCircle(sketch, "E12.16.15.0", {"center": v(25, -6) * mm, "radius": 0.15 * mm});
            skCircle(sketch, "E12.16.16.0", {"center": v(25, -7) * mm, "radius": 0.15 * mm});
            skCircle(sketch, "E12.16.17.0", {"center": v(25, -8) * mm, "radius": 0.15 * mm});
            skCircle(sketch, "E12.16.18.0", {"center": v(25, -9) * mm, "radius": 0.15 * mm});
            skCircle(sketch, "E12.16.19.0", {"center": v(25, -10) * mm, "radius": 0.15 * mm});
            skCircle(sketch, "E12.17.0.0", {"center": v(26, 9) * mm, "radius": 0.15 * mm});
            skCircle(sketch, "E12.17.1.0", {"center": v(26, 8) * mm, "radius": 0.15 * mm});
            skCircle(sketch, "E12.17.2.0", {"center": v(26, 7) * mm, "radius": 0.15 * mm});
            skCircle(sketch, "E12.17.3.0", {"center": v(26, 6) * mm, "radius": 0.15 * mm});
            skCircle(sketch, "E12.17.4.0", {"center": v(26, 5) * mm, "radius": 0.15 * mm});
            skCircle(sketch, "E12.17.5.0", {"center": v(26, 4) * mm, "radius": 0.15 * mm});
            skCircle(sketch, "E12.17.6.0", {"center": v(26, 3) * mm, "radius": 0.15 * mm});
            skCircle(sketch, "E12.17.7.0", {"center": v(26, 2) * mm, "radius": 0.15 * mm});
            skCircle(sketch, "E12.17.8.0", {"center": v(26, 1) * mm, "radius": 0.15 * mm});
            skCircle(sketch, "E12.17.9.0", {"center": v(26, 0) * mm, "radius": 0.15 * mm});
            skCircle(sketch, "E12.17.10.0", {"center": v(26, -1) * mm, "radius": 0.15 * mm});
            skCircle(sketch, "E12.17.11.0", {"center": v(26, -2) * mm, "radius": 0.15 * mm});
            skCircle(sketch, "E12.17.12.0", {"center": v(26, -3) * mm, "radius": 0.15 * mm});
            skCircle(sketch, "E12.17.13.0", {"center": v(26, -4) * mm, "radius": 0.15 * mm});
            skCircle(sketch, "E12.17.14.0", {"center": v(26, -5) * mm, "radius": 0.15 * mm});
            skCircle(sketch, "E12.17.15.0", {"center": v(26, -6) * mm, "radius": 0.15 * mm});
            skCircle(sketch, "E12.17.16.0", {"center": v(26, -7) * mm, "radius": 0.15 * mm});
            skCircle(sketch, "E12.17.17.0", {"center": v(26, -8) * mm, "radius": 0.15 * mm});
            skCircle(sketch, "E12.17.18.0", {"center": v(26, -9) * mm, "radius": 0.15 * mm});
            skCircle(sketch, "E12.17.19.0", {"center": v(26, -10) * mm, "radius": 0.15 * mm});
            skCircle(sketch, "E12.18.0.0", {"center": v(27, 9) * mm, "radius": 0.15 * mm});
            skCircle(sketch, "E12.18.1.0", {"center": v(27, 8) * mm, "radius": 0.15 * mm});
            skCircle(sketch, "E12.18.2.0", {"center": v(27, 7) * mm, "radius": 0.15 * mm});
            skCircle(sketch, "E12.18.3.0", {"center": v(27, 6) * mm, "radius": 0.15 * mm});
            skCircle(sketch, "E12.18.4.0", {"center": v(27, 5) * mm, "radius": 0.15 * mm});
            skCircle(sketch, "E12.18.5.0", {"center": v(27, 4) * mm, "radius": 0.15 * mm});
            skCircle(sketch, "E12.18.6.0", {"center": v(27, 3) * mm, "radius": 0.15 * mm});
            skCircle(sketch, "E12.18.7.0", {"center": v(27, 2) * mm, "radius": 0.15 * mm});
            skCircle(sketch, "E12.18.8.0", {"center": v(27, 1) * mm, "radius": 0.15 * mm});
            skCircle(sketch, "E12.18.9.0", {"center": v(27, 0) * mm, "radius": 0.15 * mm});
            skCircle(sketch, "E12.18.10.0", {"center": v(27, -1) * mm, "radius": 0.15 * mm});
            skCircle(sketch, "E12.18.11.0", {"center": v(27, -2) * mm, "radius": 0.15 * mm});
            skCircle(sketch, "E12.18.12.0", {"center": v(27, -3) * mm, "radius": 0.15 * mm});
            skCircle(sketch, "E12.18.13.0", {"center": v(27, -4) * mm, "radius": 0.15 * mm});
            skCircle(sketch, "E12.18.14.0", {"center": v(27, -5) * mm, "radius": 0.15 * mm});
            skCircle(sketch, "E12.18.15.0", {"center": v(27, -6) * mm, "radius": 0.15 * mm});
            skCircle(sketch, "E12.18.16.0", {"center": v(27, -7) * mm, "radius": 0.15 * mm});
            skCircle(sketch, "E12.18.17.0", {"center": v(27, -8) * mm, "radius": 0.15 * mm});
            skCircle(sketch, "E12.18.18.0", {"center": v(27, -9) * mm, "radius": 0.15 * mm});
            skCircle(sketch, "E12.18.19.0", {"center": v(27, -10) * mm, "radius": 0.15 * mm});
            skCircle(sketch, "E12.19.0.0", {"center": v(28, 9) * mm, "radius": 0.15 * mm});
            skCircle(sketch, "E12.19.1.0", {"center": v(28, 8) * mm, "radius": 0.15 * mm});
            skCircle(sketch, "E12.19.2.0", {"center": v(28, 7) * mm, "radius": 0.15 * mm});
            skCircle(sketch, "E12.19.3.0", {"center": v(28, 6) * mm, "radius": 0.15 * mm});
            skCircle(sketch, "E12.19.4.0", {"center": v(28, 5) * mm, "radius": 0.15 * mm});
            skCircle(sketch, "E12.19.5.0", {"center": v(28, 4) * mm, "radius": 0.15 * mm});
            skCircle(sketch, "E12.19.6.0", {"center": v(28, 3) * mm, "radius": 0.15 * mm});
            skCircle(sketch, "E12.19.7.0", {"center": v(28, 2) * mm, "radius": 0.15 * mm});
            skCircle(sketch, "E12.19.8.0", {"center": v(28, 1) * mm, "radius": 0.15 * mm});
            skCircle(sketch, "E12.19.9.0", {"center": v(28, 0) * mm, "radius": 0.15 * mm});
            skCircle(sketch, "E12.19.10.0", {"center": v(28, -1) * mm, "radius": 0.15 * mm});
            skCircle(sketch, "E12.19.11.0", {"center": v(28, -2) * mm, "radius": 0.15 * mm});
            skCircle(sketch, "E12.19.12.0", {"center": v(28, -3) * mm, "radius": 0.15 * mm});
            skCircle(sketch, "E12.19.13.0", {"center": v(28, -4) * mm, "radius": 0.15 * mm});
            skCircle(sketch, "E12.19.14.0", {"center": v(28, -5) * mm, "radius": 0.15 * mm});
            skCircle(sketch, "E12.19.15.0", {"center": v(28, -6) * mm, "radius": 0.15 * mm});
            skCircle(sketch, "E12.19.16.0", {"center": v(28, -7) * mm, "radius": 0.15 * mm});
            skCircle(sketch, "E12.19.17.0", {"center": v(28, -8) * mm, "radius": 0.15 * mm});
            skCircle(sketch, "E12.19.18.0", {"center": v(28, -9) * mm, "radius": 0.15 * mm});
            skCircle(sketch, "E12.19.19.0", {"center": v(28, -10) * mm, "radius": 0.15 * mm});
            skCircle(sketch, "E12.20.0.0", {"center": v(29, 9) * mm, "radius": 0.15 * mm});
            skCircle(sketch, "E12.20.1.0", {"center": v(29, 8) * mm, "radius": 0.15 * mm});
            skCircle(sketch, "E12.20.2.0", {"center": v(29, 7) * mm, "radius": 0.15 * mm});
            skCircle(sketch, "E12.20.3.0", {"center": v(29, 6) * mm, "radius": 0.15 * mm});
            skCircle(sketch, "E12.20.4.0", {"center": v(29, 5) * mm, "radius": 0.15 * mm});
            skCircle(sketch, "E12.20.5.0", {"center": v(29, 4) * mm, "radius": 0.15 * mm});
            skCircle(sketch, "E12.20.6.0", {"center": v(29, 3) * mm, "radius": 0.15 * mm});
            skCircle(sketch, "E12.20.7.0", {"center": v(29, 2) * mm, "radius": 0.15 * mm});
            skCircle(sketch, "E12.20.8.0", {"center": v(29, 1) * mm, "radius": 0.15 * mm});
            skCircle(sketch, "E12.20.9.0", {"center": v(29, 0) * mm, "radius": 0.15 * mm});
            skCircle(sketch, "E12.20.10.0", {"center": v(29, -1) * mm, "radius": 0.15 * mm});
            skCircle(sketch, "E12.20.11.0", {"center": v(29, -2) * mm, "radius": 0.15 * mm});
            skCircle(sketch, "E12.20.12.0", {"center": v(29, -3) * mm, "radius": 0.15 * mm});
            skCircle(sketch, "E12.20.13.0", {"center": v(29, -4) * mm, "radius": 0.15 * mm});
            skCircle(sketch, "E12.20.14.0", {"center": v(29, -5) * mm, "radius": 0.15 * mm});
            skCircle(sketch, "E12.20.15.0", {"center": v(29, -6) * mm, "radius": 0.15 * mm});
            skCircle(sketch, "E12.20.16.0", {"center": v(29, -7) * mm, "radius": 0.15 * mm});
            skCircle(sketch, "E12.20.17.0", {"center": v(29, -8) * mm, "radius": 0.15 * mm});
            skCircle(sketch, "E12.20.18.0", {"center": v(29, -9) * mm, "radius": 0.15 * mm});
            skCircle(sketch, "E12.20.19.0", {"center": v(29, -10) * mm, "radius": 0.15 * mm});
            skCircle(sketch, "E12.21.0.0", {"center": v(30, 9) * mm, "radius": 0.15 * mm});
            skCircle(sketch, "E12.21.1.0", {"center": v(30, 8) * mm, "radius": 0.15 * mm});
            skCircle(sketch, "E12.21.2.0", {"center": v(30, 7) * mm, "radius": 0.15 * mm});
            skCircle(sketch, "E12.21.3.0", {"center": v(30, 6) * mm, "radius": 0.15 * mm});
            skCircle(sketch, "E12.21.4.0", {"center": v(30, 5) * mm, "radius": 0.15 * mm});
            skCircle(sketch, "E12.21.5.0", {"center": v(30, 4) * mm, "radius": 0.15 * mm});
            skCircle(sketch, "E12.21.6.0", {"center": v(30, 3) * mm, "radius": 0.15 * mm});
            skCircle(sketch, "E12.21.7.0", {"center": v(30, 2) * mm, "radius": 0.15 * mm});
            skCircle(sketch, "E12.21.8.0", {"center": v(30, 1) * mm, "radius": 0.15 * mm});
            skCircle(sketch, "E12.21.9.0", {"center": v(30, 0) * mm, "radius": 0.15 * mm});
            skCircle(sketch, "E12.21.10.0", {"center": v(30, -1) * mm, "radius": 0.15 * mm});
            skCircle(sketch, "E12.21.11.0", {"center": v(30, -2) * mm, "radius": 0.15 * mm});
            skCircle(sketch, "E12.21.12.0", {"center": v(30, -3) * mm, "radius": 0.15 * mm});
            skCircle(sketch, "E12.21.13.0", {"center": v(30, -4) * mm, "radius": 0.15 * mm});
            skCircle(sketch, "E12.21.14.0", {"center": v(30, -5) * mm, "radius": 0.15 * mm});
            skCircle(sketch, "E12.21.15.0", {"center": v(30, -6) * mm, "radius": 0.15 * mm});
            skCircle(sketch, "E12.21.16.0", {"center": v(30, -7) * mm, "radius": 0.15 * mm});
            skCircle(sketch, "E12.21.17.0", {"center": v(30, -8) * mm, "radius": 0.15 * mm});
            skCircle(sketch, "E12.21.18.0", {"center": v(30, -9) * mm, "radius": 0.15 * mm});
            skCircle(sketch, "E12.21.19.0", {"center": v(30, -10) * mm, "radius": 0.15 * mm});
            skCircle(sketch, "E12.22.0.0", {"center": v(31, 9) * mm, "radius": 0.15 * mm});
            skCircle(sketch, "E12.22.1.0", {"center": v(31, 8) * mm, "radius": 0.15 * mm});
            skCircle(sketch, "E12.22.2.0", {"center": v(31, 7) * mm, "radius": 0.15 * mm});
            skCircle(sketch, "E12.22.3.0", {"center": v(31, 6) * mm, "radius": 0.15 * mm});
            skCircle(sketch, "E12.22.4.0", {"center": v(31, 5) * mm, "radius": 0.15 * mm});
            skCircle(sketch, "E12.22.5.0", {"center": v(31, 4) * mm, "radius": 0.15 * mm});
            skCircle(sketch, "E12.22.6.0", {"center": v(31, 3) * mm, "radius": 0.15 * mm});
            skCircle(sketch, "E12.22.7.0", {"center": v(31, 2) * mm, "radius": 0.15 * mm});
            skCircle(sketch, "E12.22.8.0", {"center": v(31, 1) * mm, "radius": 0.15 * mm});
            skCircle(sketch, "E12.22.9.0", {"center": v(31, 0) * mm, "radius": 0.15 * mm});
            skCircle(sketch, "E12.22.10.0", {"center": v(31, -1) * mm, "radius": 0.15 * mm});
            skCircle(sketch, "E12.22.11.0", {"center": v(31, -2) * mm, "radius": 0.15 * mm});
            skCircle(sketch, "E12.22.12.0", {"center": v(31, -3) * mm, "radius": 0.15 * mm});
            skCircle(sketch, "E12.22.13.0", {"center": v(31, -4) * mm, "radius": 0.15 * mm});
            skCircle(sketch, "E12.22.14.0", {"center": v(31, -5) * mm, "radius": 0.15 * mm});
            skCircle(sketch, "E12.22.15.0", {"center": v(31, -6) * mm, "radius": 0.15 * mm});
            skCircle(sketch, "E12.22.16.0", {"center": v(31, -7) * mm, "radius": 0.15 * mm});
            skCircle(sketch, "E12.22.17.0", {"center": v(31, -8) * mm, "radius": 0.15 * mm});
            skCircle(sketch, "E12.22.18.0", {"center": v(31, -9) * mm, "radius": 0.15 * mm});
            skCircle(sketch, "E12.22.19.0", {"center": v(31, -10) * mm, "radius": 0.15 * mm});
            skCircle(sketch, "E12.23.0.0", {"center": v(32, 9) * mm, "radius": 0.15 * mm});
            skCircle(sketch, "E12.23.1.0", {"center": v(32, 8) * mm, "radius": 0.15 * mm});
            skCircle(sketch, "E12.23.2.0", {"center": v(32, 7) * mm, "radius": 0.15 * mm});
            skCircle(sketch, "E12.23.3.0", {"center": v(32, 6) * mm, "radius": 0.15 * mm});
            skCircle(sketch, "E12.23.4.0", {"center": v(32, 5) * mm, "radius": 0.15 * mm});
            skCircle(sketch, "E12.23.5.0", {"center": v(32, 4) * mm, "radius": 0.15 * mm});
            skCircle(sketch, "E12.23.6.0", {"center": v(32, 3) * mm, "radius": 0.15 * mm});
            skCircle(sketch, "E12.23.7.0", {"center": v(32, 2) * mm, "radius": 0.15 * mm});
            skCircle(sketch, "E12.23.8.0", {"center": v(32, 1) * mm, "radius": 0.15 * mm});
            skCircle(sketch, "E12.23.9.0", {"center": v(32, 0) * mm, "radius": 0.15 * mm});
            skCircle(sketch, "E12.23.10.0", {"center": v(32, -1) * mm, "radius": 0.15 * mm});
            skCircle(sketch, "E12.23.11.0", {"center": v(32, -2) * mm, "radius": 0.15 * mm});
            skCircle(sketch, "E12.23.12.0", {"center": v(32, -3) * mm, "radius": 0.15 * mm});
            skCircle(sketch, "E12.23.13.0", {"center": v(32, -4) * mm, "radius": 0.15 * mm});
            skCircle(sketch, "E12.23.14.0", {"center": v(32, -5) * mm, "radius": 0.15 * mm});
            skCircle(sketch, "E12.23.15.0", {"center": v(32, -6) * mm, "radius": 0.15 * mm});
            skCircle(sketch, "E12.23.16.0", {"center": v(32, -7) * mm, "radius": 0.15 * mm});
            skCircle(sketch, "E12.23.17.0", {"center": v(32, -8) * mm, "radius": 0.15 * mm});
            skCircle(sketch, "E12.23.18.0", {"center": v(32, -9) * mm, "radius": 0.15 * mm});
            skCircle(sketch, "E12.23.19.0", {"center": v(32, -10) * mm, "radius": 0.15 * mm});
            skCircle(sketch, "E12.24.0.0", {"center": v(33, 9) * mm, "radius": 0.15 * mm});
            skCircle(sketch, "E12.24.1.0", {"center": v(33, 8) * mm, "radius": 0.15 * mm});
            skCircle(sketch, "E12.24.2.0", {"center": v(33, 7) * mm, "radius": 0.15 * mm});
            skCircle(sketch, "E12.24.3.0", {"center": v(33, 6) * mm, "radius": 0.15 * mm});
            skCircle(sketch, "E12.24.4.0", {"center": v(33, 5) * mm, "radius": 0.15 * mm});
            skCircle(sketch, "E12.24.5.0", {"center": v(33, 4) * mm, "radius": 0.15 * mm});
            skCircle(sketch, "E12.24.6.0", {"center": v(33, 3) * mm, "radius": 0.15 * mm});
            skCircle(sketch, "E12.24.7.0", {"center": v(33, 2) * mm, "radius": 0.15 * mm});
            skCircle(sketch, "E12.24.8.0", {"center": v(33, 1) * mm, "radius": 0.15 * mm});
            skCircle(sketch, "E12.24.9.0", {"center": v(33, 0) * mm, "radius": 0.15 * mm});
            skCircle(sketch, "E12.24.10.0", {"center": v(33, -1) * mm, "radius": 0.15 * mm});
            skCircle(sketch, "E12.24.11.0", {"center": v(33, -2) * mm, "radius": 0.15 * mm});
            skCircle(sketch, "E12.24.12.0", {"center": v(33, -3) * mm, "radius": 0.15 * mm});
            skCircle(sketch, "E12.24.13.0", {"center": v(33, -4) * mm, "radius": 0.15 * mm});
            skCircle(sketch, "E12.24.14.0", {"center": v(33, -5) * mm, "radius": 0.15 * mm});
            skCircle(sketch, "E12.24.15.0", {"center": v(33, -6) * mm, "radius": 0.15 * mm});
            skCircle(sketch, "E12.24.16.0", {"center": v(33, -7) * mm, "radius": 0.15 * mm});
            skCircle(sketch, "E12.24.17.0", {"center": v(33, -8) * mm, "radius": 0.15 * mm});
            skCircle(sketch, "E12.24.18.0", {"center": v(33, -9) * mm, "radius": 0.15 * mm});
            skCircle(sketch, "E12.24.19.0", {"center": v(33, -10) * mm, "radius": 0.15 * mm});
            skCircle(sketch, "E12.25.0.0", {"center": v(34, 9) * mm, "radius": 0.15 * mm});
            skCircle(sketch, "E12.25.1.0", {"center": v(34, 8) * mm, "radius": 0.15 * mm});
            skCircle(sketch, "E12.25.2.0", {"center": v(34, 7) * mm, "radius": 0.15 * mm});
            skCircle(sketch, "E12.25.3.0", {"center": v(34, 6) * mm, "radius": 0.15 * mm});
            skCircle(sketch, "E12.25.4.0", {"center": v(34, 5) * mm, "radius": 0.15 * mm});
            skCircle(sketch, "E12.25.5.0", {"center": v(34, 4) * mm, "radius": 0.15 * mm});
            skCircle(sketch, "E12.25.6.0", {"center": v(34, 3) * mm, "radius": 0.15 * mm});
            skCircle(sketch, "E12.25.7.0", {"center": v(34, 2) * mm, "radius": 0.15 * mm});
            skCircle(sketch, "E12.25.8.0", {"center": v(34, 1) * mm, "radius": 0.15 * mm});
            skCircle(sketch, "E12.25.9.0", {"center": v(34, 0) * mm, "radius": 0.15 * mm});
            skCircle(sketch, "E12.25.10.0", {"center": v(34, -1) * mm, "radius": 0.15 * mm});
            skCircle(sketch, "E12.25.11.0", {"center": v(34, -2) * mm, "radius": 0.15 * mm});
            skCircle(sketch, "E12.25.12.0", {"center": v(34, -3) * mm, "radius": 0.15 * mm});
            skCircle(sketch, "E12.25.13.0", {"center": v(34, -4) * mm, "radius": 0.15 * mm});
            skCircle(sketch, "E12.25.14.0", {"center": v(34, -5) * mm, "radius": 0.15 * mm});
            skCircle(sketch, "E12.25.15.0", {"center": v(34, -6) * mm, "radius": 0.15 * mm});
            skCircle(sketch, "E12.25.16.0", {"center": v(34, -7) * mm, "radius": 0.15 * mm});
            skCircle(sketch, "E12.25.17.0", {"center": v(34, -8) * mm, "radius": 0.15 * mm});
            skCircle(sketch, "E12.25.18.0", {"center": v(34, -9) * mm, "radius": 0.15 * mm});
            skCircle(sketch, "E12.25.19.0", {"center": v(34, -10) * mm, "radius": 0.15 * mm});
            skCircle(sketch, "E12.26.0.0", {"center": v(35, 9) * mm, "radius": 0.15 * mm});
            skCircle(sketch, "E12.26.1.0", {"center": v(35, 8) * mm, "radius": 0.15 * mm});
            skCircle(sketch, "E12.26.2.0", {"center": v(35, 7) * mm, "radius": 0.15 * mm});
            skCircle(sketch, "E12.26.3.0", {"center": v(35, 6) * mm, "radius": 0.15 * mm});
            skCircle(sketch, "E12.26.4.0", {"center": v(35, 5) * mm, "radius": 0.15 * mm});
            skCircle(sketch, "E12.26.5.0", {"center": v(35, 4) * mm, "radius": 0.15 * mm});
            skCircle(sketch, "E12.26.6.0", {"center": v(35, 3) * mm, "radius": 0.15 * mm});
            skCircle(sketch, "E12.26.7.0", {"center": v(35, 2) * mm, "radius": 0.15 * mm});
            skCircle(sketch, "E12.26.8.0", {"center": v(35, 1) * mm, "radius": 0.15 * mm});
            skCircle(sketch, "E12.26.9.0", {"center": v(35, 0) * mm, "radius": 0.15 * mm});
            skCircle(sketch, "E12.26.10.0", {"center": v(35, -1) * mm, "radius": 0.15 * mm});
            skCircle(sketch, "E12.26.11.0", {"center": v(35, -2) * mm, "radius": 0.15 * mm});
            skCircle(sketch, "E12.26.12.0", {"center": v(35, -3) * mm, "radius": 0.15 * mm});
            skCircle(sketch, "E12.26.13.0", {"center": v(35, -4) * mm, "radius": 0.15 * mm});
            skCircle(sketch, "E12.26.14.0", {"center": v(35, -5) * mm, "radius": 0.15 * mm});
            skCircle(sketch, "E12.26.15.0", {"center": v(35, -6) * mm, "radius": 0.15 * mm});
            skCircle(sketch, "E12.26.16.0", {"center": v(35, -7) * mm, "radius": 0.15 * mm});
            skCircle(sketch, "E12.26.17.0", {"center": v(35, -8) * mm, "radius": 0.15 * mm});
            skCircle(sketch, "E12.26.18.0", {"center": v(35, -9) * mm, "radius": 0.15 * mm});
            skCircle(sketch, "E12.26.19.0", {"center": v(35, -10) * mm, "radius": 0.15 * mm});
            skCircle(sketch, "E12.27.0.0", {"center": v(36, 9) * mm, "radius": 0.15 * mm});
            skCircle(sketch, "E12.27.1.0", {"center": v(36, 8) * mm, "radius": 0.15 * mm});
            skCircle(sketch, "E12.27.2.0", {"center": v(36, 7) * mm, "radius": 0.15 * mm});
            skCircle(sketch, "E12.27.3.0", {"center": v(36, 6) * mm, "radius": 0.15 * mm});
            skCircle(sketch, "E12.27.4.0", {"center": v(36, 5) * mm, "radius": 0.15 * mm});
            skCircle(sketch, "E12.27.5.0", {"center": v(36, 4) * mm, "radius": 0.15 * mm});
            skCircle(sketch, "E12.27.6.0", {"center": v(36, 3) * mm, "radius": 0.15 * mm});
            skCircle(sketch, "E12.27.7.0", {"center": v(36, 2) * mm, "radius": 0.15 * mm});
            skCircle(sketch, "E12.27.8.0", {"center": v(36, 1) * mm, "radius": 0.15 * mm});
            skCircle(sketch, "E12.27.9.0", {"center": v(36, 0) * mm, "radius": 0.15 * mm});
            skCircle(sketch, "E12.27.10.0", {"center": v(36, -1) * mm, "radius": 0.15 * mm});
            skCircle(sketch, "E12.27.11.0", {"center": v(36, -2) * mm, "radius": 0.15 * mm});
            skCircle(sketch, "E12.27.12.0", {"center": v(36, -3) * mm, "radius": 0.15 * mm});
            skCircle(sketch, "E12.27.13.0", {"center": v(36, -4) * mm, "radius": 0.15 * mm});
            skCircle(sketch, "E12.27.14.0", {"center": v(36, -5) * mm, "radius": 0.15 * mm});
            skCircle(sketch, "E12.27.15.0", {"center": v(36, -6) * mm, "radius": 0.15 * mm});
            skCircle(sketch, "E12.27.16.0", {"center": v(36, -7) * mm, "radius": 0.15 * mm});
            skCircle(sketch, "E12.27.17.0", {"center": v(36, -8) * mm, "radius": 0.15 * mm});
            skCircle(sketch, "E12.27.18.0", {"center": v(36, -9) * mm, "radius": 0.15 * mm});
            skCircle(sketch, "E12.27.19.0", {"center": v(36, -10) * mm, "radius": 0.15 * mm});
            skCircle(sketch, "E12.28.0.0", {"center": v(37, 9) * mm, "radius": 0.15 * mm});
            skCircle(sketch, "E12.28.1.0", {"center": v(37, 8) * mm, "radius": 0.15 * mm});
            skCircle(sketch, "E12.28.2.0", {"center": v(37, 7) * mm, "radius": 0.15 * mm});
            skCircle(sketch, "E12.28.3.0", {"center": v(37, 6) * mm, "radius": 0.15 * mm});
            skCircle(sketch, "E12.28.4.0", {"center": v(37, 5) * mm, "radius": 0.15 * mm});
            skCircle(sketch, "E12.28.5.0", {"center": v(37, 4) * mm, "radius": 0.15 * mm});
            skCircle(sketch, "E12.28.6.0", {"center": v(37, 3) * mm, "radius": 0.15 * mm});
            skCircle(sketch, "E12.28.7.0", {"center": v(37, 2) * mm, "radius": 0.15 * mm});
            skCircle(sketch, "E12.28.8.0", {"center": v(37, 1) * mm, "radius": 0.15 * mm});
            skCircle(sketch, "E12.28.9.0", {"center": v(37, 0) * mm, "radius": 0.15 * mm});
            skCircle(sketch, "E12.28.10.0", {"center": v(37, -1) * mm, "radius": 0.15 * mm});
            skCircle(sketch, "E12.28.11.0", {"center": v(37, -2) * mm, "radius": 0.15 * mm});
            skCircle(sketch, "E12.28.12.0", {"center": v(37, -3) * mm, "radius": 0.15 * mm});
            skCircle(sketch, "E12.28.13.0", {"center": v(37, -4) * mm, "radius": 0.15 * mm});
            skCircle(sketch, "E12.28.14.0", {"center": v(37, -5) * mm, "radius": 0.15 * mm});
            skCircle(sketch, "E12.28.15.0", {"center": v(37, -6) * mm, "radius": 0.15 * mm});
            skCircle(sketch, "E12.28.16.0", {"center": v(37, -7) * mm, "radius": 0.15 * mm});
            skCircle(sketch, "E12.28.17.0", {"center": v(37, -8) * mm, "radius": 0.15 * mm});
            skCircle(sketch, "E12.28.18.0", {"center": v(37, -9) * mm, "radius": 0.15 * mm});
            skCircle(sketch, "E12.28.19.0", {"center": v(37, -10) * mm, "radius": 0.15 * mm});
            skCircle(sketch, "E12.29.0.0", {"center": v(38, 9) * mm, "radius": 0.15 * mm});
            skCircle(sketch, "E12.29.1.0", {"center": v(38, 8) * mm, "radius": 0.15 * mm});
            skCircle(sketch, "E12.29.2.0", {"center": v(38, 7) * mm, "radius": 0.15 * mm});
            skCircle(sketch, "E12.29.3.0", {"center": v(38, 6) * mm, "radius": 0.15 * mm});
            skCircle(sketch, "E12.29.4.0", {"center": v(38, 5) * mm, "radius": 0.15 * mm});
            skCircle(sketch, "E12.29.5.0", {"center": v(38, 4) * mm, "radius": 0.15 * mm});
            skCircle(sketch, "E12.29.6.0", {"center": v(38, 3) * mm, "radius": 0.15 * mm});
            skCircle(sketch, "E12.29.7.0", {"center": v(38, 2) * mm, "radius": 0.15 * mm});
            skCircle(sketch, "E12.29.8.0", {"center": v(38, 1) * mm, "radius": 0.15 * mm});
            skCircle(sketch, "E12.29.9.0", {"center": v(38, 0) * mm, "radius": 0.15 * mm});
            skCircle(sketch, "E12.29.10.0", {"center": v(38, -1) * mm, "radius": 0.15 * mm});
            skCircle(sketch, "E12.29.11.0", {"center": v(38, -2) * mm, "radius": 0.15 * mm});
            skCircle(sketch, "E12.29.12.0", {"center": v(38, -3) * mm, "radius": 0.15 * mm});
            skCircle(sketch, "E12.29.13.0", {"center": v(38, -4) * mm, "radius": 0.15 * mm});
            skCircle(sketch, "E12.29.14.0", {"center": v(38, -5) * mm, "radius": 0.15 * mm});
            skCircle(sketch, "E12.29.15.0", {"center": v(38, -6) * mm, "radius": 0.15 * mm});
            skCircle(sketch, "E12.29.16.0", {"center": v(38, -7) * mm, "radius": 0.15 * mm});
            skCircle(sketch, "E12.29.17.0", {"center": v(38, -8) * mm, "radius": 0.15 * mm});
            skCircle(sketch, "E12.29.18.0", {"center": v(38, -9) * mm, "radius": 0.15 * mm});
            skCircle(sketch, "E12.29.19.0", {"center": v(38, -10) * mm, "radius": 0.15 * mm});
            skCircle(sketch, "E12.30.0.0", {"center": v(39, 9) * mm, "radius": 0.15 * mm});
            skCircle(sketch, "E12.30.1.0", {"center": v(39, 8) * mm, "radius": 0.15 * mm});
            skCircle(sketch, "E12.30.2.0", {"center": v(39, 7) * mm, "radius": 0.15 * mm});
            skCircle(sketch, "E12.30.3.0", {"center": v(39, 6) * mm, "radius": 0.15 * mm});
            skCircle(sketch, "E12.30.4.0", {"center": v(39, 5) * mm, "radius": 0.15 * mm});
            skCircle(sketch, "E12.30.5.0", {"center": v(39, 4) * mm, "radius": 0.15 * mm});
            skCircle(sketch, "E12.30.6.0", {"center": v(39, 3) * mm, "radius": 0.15 * mm});
            skCircle(sketch, "E12.30.7.0", {"center": v(39, 2) * mm, "radius": 0.15 * mm});
            skCircle(sketch, "E12.30.8.0", {"center": v(39, 1) * mm, "radius": 0.15 * mm});
            skCircle(sketch, "E12.30.9.0", {"center": v(39, 0) * mm, "radius": 0.15 * mm});
            skCircle(sketch, "E12.30.10.0", {"center": v(39, -1) * mm, "radius": 0.15 * mm});
            skCircle(sketch, "E12.30.11.0", {"center": v(39, -2) * mm, "radius": 0.15 * mm});
            skCircle(sketch, "E12.30.12.0", {"center": v(39, -3) * mm, "radius": 0.15 * mm});
            skCircle(sketch, "E12.30.13.0", {"center": v(39, -4) * mm, "radius": 0.15 * mm});
            skCircle(sketch, "E12.30.14.0", {"center": v(39, -5) * mm, "radius": 0.15 * mm});
            skCircle(sketch, "E12.30.15.0", {"center": v(39, -6) * mm, "radius": 0.15 * mm});
            skCircle(sketch, "E12.30.16.0", {"center": v(39, -7) * mm, "radius": 0.15 * mm});
            skCircle(sketch, "E12.30.17.0", {"center": v(39, -8) * mm, "radius": 0.15 * mm});
            skCircle(sketch, "E12.30.18.0", {"center": v(39, -9) * mm, "radius": 0.15 * mm});
            skCircle(sketch, "E12.30.19.0", {"center": v(39, -10) * mm, "radius": 0.15 * mm});
            skCircle(sketch, "E12.31.0.0", {"center": v(40, 9) * mm, "radius": 0.15 * mm});
            skCircle(sketch, "E12.31.1.0", {"center": v(40, 8) * mm, "radius": 0.15 * mm});
            skCircle(sketch, "E12.31.2.0", {"center": v(40, 7) * mm, "radius": 0.15 * mm});
            skCircle(sketch, "E12.31.3.0", {"center": v(40, 6) * mm, "radius": 0.15 * mm});
            skCircle(sketch, "E12.31.4.0", {"center": v(40, 5) * mm, "radius": 0.15 * mm});
            skCircle(sketch, "E12.31.5.0", {"center": v(40, 4) * mm, "radius": 0.15 * mm});
            skCircle(sketch, "E12.31.6.0", {"center": v(40, 3) * mm, "radius": 0.15 * mm});
            skCircle(sketch, "E12.31.7.0", {"center": v(40, 2) * mm, "radius": 0.15 * mm});
            skCircle(sketch, "E12.31.8.0", {"center": v(40, 1) * mm, "radius": 0.15 * mm});
            skCircle(sketch, "E12.31.9.0", {"center": v(40, 0) * mm, "radius": 0.15 * mm});
            skCircle(sketch, "E12.31.10.0", {"center": v(40, -1) * mm, "radius": 0.15 * mm});
            skCircle(sketch, "E12.31.11.0", {"center": v(40, -2) * mm, "radius": 0.15 * mm});
            skCircle(sketch, "E12.31.12.0", {"center": v(40, -3) * mm, "radius": 0.15 * mm});
            skCircle(sketch, "E12.31.13.0", {"center": v(40, -4) * mm, "radius": 0.15 * mm});
            skCircle(sketch, "E12.31.14.0", {"center": v(40, -5) * mm, "radius": 0.15 * mm});
            skCircle(sketch, "E12.31.15.0", {"center": v(40, -6) * mm, "radius": 0.15 * mm});
            skCircle(sketch, "E12.31.16.0", {"center": v(40, -7) * mm, "radius": 0.15 * mm});
            skCircle(sketch, "E12.31.17.0", {"center": v(40, -8) * mm, "radius": 0.15 * mm});
            skCircle(sketch, "E12.31.18.0", {"center": v(40, -9) * mm, "radius": 0.15 * mm});
            skCircle(sketch, "E12.31.19.0", {"center": v(40, -10) * mm, "radius": 0.15 * mm});
            skCircle(sketch, "E12.32.0.0", {"center": v(41, 9) * mm, "radius": 0.15 * mm});
            skCircle(sketch, "E12.32.1.0", {"center": v(41, 8) * mm, "radius": 0.15 * mm});
            skCircle(sketch, "E12.32.2.0", {"center": v(41, 7) * mm, "radius": 0.15 * mm});
            skCircle(sketch, "E12.32.3.0", {"center": v(41, 6) * mm, "radius": 0.15 * mm});
            skCircle(sketch, "E12.32.4.0", {"center": v(41, 5) * mm, "radius": 0.15 * mm});
            skCircle(sketch, "E12.32.5.0", {"center": v(41, 4) * mm, "radius": 0.15 * mm});
            skCircle(sketch, "E12.32.6.0", {"center": v(41, 3) * mm, "radius": 0.15 * mm});
            skCircle(sketch, "E12.32.7.0", {"center": v(41, 2) * mm, "radius": 0.15 * mm});
            skCircle(sketch, "E12.32.8.0", {"center": v(41, 1) * mm, "radius": 0.15 * mm});
            skCircle(sketch, "E12.32.9.0", {"center": v(41, 0) * mm, "radius": 0.15 * mm});
            skCircle(sketch, "E12.32.10.0", {"center": v(41, -1) * mm, "radius": 0.15 * mm});
            skCircle(sketch, "E12.32.11.0", {"center": v(41, -2) * mm, "radius": 0.15 * mm});
            skCircle(sketch, "E12.32.12.0", {"center": v(41, -3) * mm, "radius": 0.15 * mm});
            skCircle(sketch, "E12.32.13.0", {"center": v(41, -4) * mm, "radius": 0.15 * mm});
            skCircle(sketch, "E12.32.14.0", {"center": v(41, -5) * mm, "radius": 0.15 * mm});
            skCircle(sketch, "E12.32.15.0", {"center": v(41, -6) * mm, "radius": 0.15 * mm});
            skCircle(sketch, "E12.32.16.0", {"center": v(41, -7) * mm, "radius": 0.15 * mm});
            skCircle(sketch, "E12.32.17.0", {"center": v(41, -8) * mm, "radius": 0.15 * mm});
            skCircle(sketch, "E12.32.18.0", {"center": v(41, -9) * mm, "radius": 0.15 * mm});
            skCircle(sketch, "E12.32.19.0", {"center": v(41, -10) * mm, "radius": 0.15 * mm});
            skCircle(sketch, "E12.33.0.0", {"center": v(42, 9) * mm, "radius": 0.15 * mm});
            skCircle(sketch, "E12.33.1.0", {"center": v(42, 8) * mm, "radius": 0.15 * mm});
            skCircle(sketch, "E12.33.2.0", {"center": v(42, 7) * mm, "radius": 0.15 * mm});
            skCircle(sketch, "E12.33.3.0", {"center": v(42, 6) * mm, "radius": 0.15 * mm});
            skCircle(sketch, "E12.33.4.0", {"center": v(42, 5) * mm, "radius": 0.15 * mm});
            skCircle(sketch, "E12.33.5.0", {"center": v(42, 4) * mm, "radius": 0.15 * mm});
            skCircle(sketch, "E12.33.6.0", {"center": v(42, 3) * mm, "radius": 0.15 * mm});
            skCircle(sketch, "E12.33.7.0", {"center": v(42, 2) * mm, "radius": 0.15 * mm});
            skCircle(sketch, "E12.33.8.0", {"center": v(42, 1) * mm, "radius": 0.15 * mm});
            skCircle(sketch, "E12.33.9.0", {"center": v(42, 0) * mm, "radius": 0.15 * mm});
            skCircle(sketch, "E12.33.10.0", {"center": v(42, -1) * mm, "radius": 0.15 * mm});
            skCircle(sketch, "E12.33.11.0", {"center": v(42, -2) * mm, "radius": 0.15 * mm});
            skCircle(sketch, "E12.33.12.0", {"center": v(42, -3) * mm, "radius": 0.15 * mm});
            skCircle(sketch, "E12.33.13.0", {"center": v(42, -4) * mm, "radius": 0.15 * mm});
            skCircle(sketch, "E12.33.14.0", {"center": v(42, -5) * mm, "radius": 0.15 * mm});
            skCircle(sketch, "E12.33.15.0", {"center": v(42, -6) * mm, "radius": 0.15 * mm});
            skCircle(sketch, "E12.33.16.0", {"center": v(42, -7) * mm, "radius": 0.15 * mm});
            skCircle(sketch, "E12.33.17.0", {"center": v(42, -8) * mm, "radius": 0.15 * mm});
            skCircle(sketch, "E12.33.18.0", {"center": v(42, -9) * mm, "radius": 0.15 * mm});
            skCircle(sketch, "E12.33.19.0", {"center": v(42, -10) * mm, "radius": 0.15 * mm});
            skCircle(sketch, "E12.34.0.0", {"center": v(43, 9) * mm, "radius": 0.15 * mm});
            skCircle(sketch, "E12.34.1.0", {"center": v(43, 8) * mm, "radius": 0.15 * mm});
            skCircle(sketch, "E12.34.2.0", {"center": v(43, 7) * mm, "radius": 0.15 * mm});
            skCircle(sketch, "E12.34.3.0", {"center": v(43, 6) * mm, "radius": 0.15 * mm});
            skCircle(sketch, "E12.34.4.0", {"center": v(43, 5) * mm, "radius": 0.15 * mm});
            skCircle(sketch, "E12.34.5.0", {"center": v(43, 4) * mm, "radius": 0.15 * mm});
            skCircle(sketch, "E12.34.6.0", {"center": v(43, 3) * mm, "radius": 0.15 * mm});
            skCircle(sketch, "E12.34.7.0", {"center": v(43, 2) * mm, "radius": 0.15 * mm});
            skCircle(sketch, "E12.34.8.0", {"center": v(43, 1) * mm, "radius": 0.15 * mm});
            skCircle(sketch, "E12.34.9.0", {"center": v(43, 0) * mm, "radius": 0.15 * mm});
            skCircle(sketch, "E12.34.10.0", {"center": v(43, -1) * mm, "radius": 0.15 * mm});
            skCircle(sketch, "E12.34.11.0", {"center": v(43, -2) * mm, "radius": 0.15 * mm});
            skCircle(sketch, "E12.34.12.0", {"center": v(43, -3) * mm, "radius": 0.15 * mm});
            skCircle(sketch, "E12.34.13.0", {"center": v(43, -4) * mm, "radius": 0.15 * mm});
            skCircle(sketch, "E12.34.14.0", {"center": v(43, -5) * mm, "radius": 0.15 * mm});
            skCircle(sketch, "E12.34.15.0", {"center": v(43, -6) * mm, "radius": 0.15 * mm});
            skCircle(sketch, "E12.34.16.0", {"center": v(43, -7) * mm, "radius": 0.15 * mm});
            skCircle(sketch, "E12.34.17.0", {"center": v(43, -8) * mm, "radius": 0.15 * mm});
            skCircle(sketch, "E12.34.18.0", {"center": v(43, -9) * mm, "radius": 0.15 * mm});
            skCircle(sketch, "E12.34.19.0", {"center": v(43, -10) * mm, "radius": 0.15 * mm});
            skCircle(sketch, "E12.35.0.0", {"center": v(44, 9) * mm, "radius": 0.15 * mm});
            skCircle(sketch, "E12.35.1.0", {"center": v(44, 8) * mm, "radius": 0.15 * mm});
            skCircle(sketch, "E12.35.2.0", {"center": v(44, 7) * mm, "radius": 0.15 * mm});
            skCircle(sketch, "E12.35.3.0", {"center": v(44, 6) * mm, "radius": 0.15 * mm});
            skCircle(sketch, "E12.35.4.0", {"center": v(44, 5) * mm, "radius": 0.15 * mm});
            skCircle(sketch, "E12.35.5.0", {"center": v(44, 4) * mm, "radius": 0.15 * mm});
            skCircle(sketch, "E12.35.6.0", {"center": v(44, 3) * mm, "radius": 0.15 * mm});
            skCircle(sketch, "E12.35.7.0", {"center": v(44, 2) * mm, "radius": 0.15 * mm});
            skCircle(sketch, "E12.35.8.0", {"center": v(44, 1) * mm, "radius": 0.15 * mm});
            skCircle(sketch, "E12.35.9.0", {"center": v(44, 0) * mm, "radius": 0.15 * mm});
            skCircle(sketch, "E12.35.10.0", {"center": v(44, -1) * mm, "radius": 0.15 * mm});
            skCircle(sketch, "E12.35.11.0", {"center": v(44, -2) * mm, "radius": 0.15 * mm});
            skCircle(sketch, "E12.35.12.0", {"center": v(44, -3) * mm, "radius": 0.15 * mm});
            skCircle(sketch, "E12.35.13.0", {"center": v(44, -4) * mm, "radius": 0.15 * mm});
            skCircle(sketch, "E12.35.14.0", {"center": v(44, -5) * mm, "radius": 0.15 * mm});
            skCircle(sketch, "E12.35.15.0", {"center": v(44, -6) * mm, "radius": 0.15 * mm});
            skCircle(sketch, "E12.35.16.0", {"center": v(44, -7) * mm, "radius": 0.15 * mm});
            skCircle(sketch, "E12.35.17.0", {"center": v(44, -8) * mm, "radius": 0.15 * mm});
            skCircle(sketch, "E12.35.18.0", {"center": v(44, -9) * mm, "radius": 0.15 * mm});
            skCircle(sketch, "E12.35.19.0", {"center": v(44, -10) * mm, "radius": 0.15 * mm});
            skCircle(sketch, "E12.36.0.0", {"center": v(45, 9) * mm, "radius": 0.15 * mm});
            skCircle(sketch, "E12.36.1.0", {"center": v(45, 8) * mm, "radius": 0.15 * mm});
            skCircle(sketch, "E12.36.2.0", {"center": v(45, 7) * mm, "radius": 0.15 * mm});
            skCircle(sketch, "E12.36.3.0", {"center": v(45, 6) * mm, "radius": 0.15 * mm});
            skCircle(sketch, "E12.36.4.0", {"center": v(45, 5) * mm, "radius": 0.15 * mm});
            skCircle(sketch, "E12.36.5.0", {"center": v(45, 4) * mm, "radius": 0.15 * mm});
            skCircle(sketch, "E12.36.6.0", {"center": v(45, 3) * mm, "radius": 0.15 * mm});
            skCircle(sketch, "E12.36.7.0", {"center": v(45, 2) * mm, "radius": 0.15 * mm});
            skCircle(sketch, "E12.36.8.0", {"center": v(45, 1) * mm, "radius": 0.15 * mm});
            skCircle(sketch, "E12.36.9.0", {"center": v(45, 0) * mm, "radius": 0.15 * mm});
            skCircle(sketch, "E12.36.10.0", {"center": v(45, -1) * mm, "radius": 0.15 * mm});
            skCircle(sketch, "E12.36.11.0", {"center": v(45, -2) * mm, "radius": 0.15 * mm});
            skCircle(sketch, "E12.36.12.0", {"center": v(45, -3) * mm, "radius": 0.15 * mm});
            skCircle(sketch, "E12.36.13.0", {"center": v(45, -4) * mm, "radius": 0.15 * mm});
            skCircle(sketch, "E12.36.14.0", {"center": v(45, -5) * mm, "radius": 0.15 * mm});
            skCircle(sketch, "E12.36.15.0", {"center": v(45, -6) * mm, "radius": 0.15 * mm});
            skCircle(sketch, "E12.36.16.0", {"center": v(45, -7) * mm, "radius": 0.15 * mm});
            skCircle(sketch, "E12.36.17.0", {"center": v(45, -8) * mm, "radius": 0.15 * mm});
            skCircle(sketch, "E12.36.18.0", {"center": v(45, -9) * mm, "radius": 0.15 * mm});
            skCircle(sketch, "E12.36.19.0", {"center": v(45, -10) * mm, "radius": 0.15 * mm});
            skCircle(sketch, "E12.37.0.0", {"center": v(46, 9) * mm, "radius": 0.15 * mm});
            skCircle(sketch, "E12.37.1.0", {"center": v(46, 8) * mm, "radius": 0.15 * mm});
            skCircle(sketch, "E12.37.2.0", {"center": v(46, 7) * mm, "radius": 0.15 * mm});
            skCircle(sketch, "E12.37.3.0", {"center": v(46, 6) * mm, "radius": 0.15 * mm});
            skCircle(sketch, "E12.37.4.0", {"center": v(46, 5) * mm, "radius": 0.15 * mm});
            skCircle(sketch, "E12.37.5.0", {"center": v(46, 4) * mm, "radius": 0.15 * mm});
            skCircle(sketch, "E12.37.6.0", {"center": v(46, 3) * mm, "radius": 0.15 * mm});
            skCircle(sketch, "E12.37.7.0", {"center": v(46, 2) * mm, "radius": 0.15 * mm});
            skCircle(sketch, "E12.37.8.0", {"center": v(46, 1) * mm, "radius": 0.15 * mm});
            skCircle(sketch, "E12.37.9.0", {"center": v(46, 0) * mm, "radius": 0.15 * mm});
            skCircle(sketch, "E12.37.10.0", {"center": v(46, -1) * mm, "radius": 0.15 * mm});
            skCircle(sketch, "E12.37.11.0", {"center": v(46, -2) * mm, "radius": 0.15 * mm});
            skCircle(sketch, "E12.37.12.0", {"center": v(46, -3) * mm, "radius": 0.15 * mm});
            skCircle(sketch, "E12.37.13.0", {"center": v(46, -4) * mm, "radius": 0.15 * mm});
            skCircle(sketch, "E12.37.14.0", {"center": v(46, -5) * mm, "radius": 0.15 * mm});
            skCircle(sketch, "E12.37.15.0", {"center": v(46, -6) * mm, "radius": 0.15 * mm});
            skCircle(sketch, "E12.37.16.0", {"center": v(46, -7) * mm, "radius": 0.15 * mm});
            skCircle(sketch, "E12.37.17.0", {"center": v(46, -8) * mm, "radius": 0.15 * mm});
            skCircle(sketch, "E12.37.18.0", {"center": v(46, -9) * mm, "radius": 0.15 * mm});
            skCircle(sketch, "E12.37.19.0", {"center": v(46, -10) * mm, "radius": 0.15 * mm});
            skCircle(sketch, "E12.38.0.0", {"center": v(47, 9) * mm, "radius": 0.15 * mm});
            skCircle(sketch, "E12.38.1.0", {"center": v(47, 8) * mm, "radius": 0.15 * mm});
            skCircle(sketch, "E12.38.2.0", {"center": v(47, 7) * mm, "radius": 0.15 * mm});
            skCircle(sketch, "E12.38.3.0", {"center": v(47, 6) * mm, "radius": 0.15 * mm});
            skCircle(sketch, "E12.38.4.0", {"center": v(47, 5) * mm, "radius": 0.15 * mm});
            skCircle(sketch, "E12.38.5.0", {"center": v(47, 4) * mm, "radius": 0.15 * mm});
            skCircle(sketch, "E12.38.6.0", {"center": v(47, 3) * mm, "radius": 0.15 * mm});
            skCircle(sketch, "E12.38.7.0", {"center": v(47, 2) * mm, "radius": 0.15 * mm});
            skCircle(sketch, "E12.38.8.0", {"center": v(47, 1) * mm, "radius": 0.15 * mm});
            skCircle(sketch, "E12.38.9.0", {"center": v(47, 0) * mm, "radius": 0.15 * mm});
            skCircle(sketch, "E12.38.10.0", {"center": v(47, -1) * mm, "radius": 0.15 * mm});
            skCircle(sketch, "E12.38.11.0", {"center": v(47, -2) * mm, "radius": 0.15 * mm});
            skCircle(sketch, "E12.38.12.0", {"center": v(47, -3) * mm, "radius": 0.15 * mm});
            skCircle(sketch, "E12.38.13.0", {"center": v(47, -4) * mm, "radius": 0.15 * mm});
            skCircle(sketch, "E12.38.14.0", {"center": v(47, -5) * mm, "radius": 0.15 * mm});
            skCircle(sketch, "E12.38.15.0", {"center": v(47, -6) * mm, "radius": 0.15 * mm});
            skCircle(sketch, "E12.38.16.0", {"center": v(47, -7) * mm, "radius": 0.15 * mm});
            skCircle(sketch, "E12.38.17.0", {"center": v(47, -8) * mm, "radius": 0.15 * mm});
            skCircle(sketch, "E12.38.18.0", {"center": v(47, -9) * mm, "radius": 0.15 * mm});
            skCircle(sketch, "E12.38.19.0", {"center": v(47, -10) * mm, "radius": 0.15 * mm});
            skCircle(sketch, "E12.39.0.0", {"center": v(48, 9) * mm, "radius": 0.15 * mm});
            skCircle(sketch, "E12.39.1.0", {"center": v(48, 8) * mm, "radius": 0.15 * mm});
            skCircle(sketch, "E12.39.2.0", {"center": v(48, 7) * mm, "radius": 0.15 * mm});
            skCircle(sketch, "E12.39.3.0", {"center": v(48, 6) * mm, "radius": 0.15 * mm});
            skCircle(sketch, "E12.39.4.0", {"center": v(48, 5) * mm, "radius": 0.15 * mm});
            skCircle(sketch, "E12.39.5.0", {"center": v(48, 4) * mm, "radius": 0.15 * mm});
            skCircle(sketch, "E12.39.6.0", {"center": v(48, 3) * mm, "radius": 0.15 * mm});
            skCircle(sketch, "E12.39.7.0", {"center": v(48, 2) * mm, "radius": 0.15 * mm});
            skCircle(sketch, "E12.39.8.0", {"center": v(48, 1) * mm, "radius": 0.15 * mm});
            skCircle(sketch, "E12.39.9.0", {"center": v(48, 0) * mm, "radius": 0.15 * mm});
            skCircle(sketch, "E12.39.10.0", {"center": v(48, -1) * mm, "radius": 0.15 * mm});
            skCircle(sketch, "E12.39.11.0", {"center": v(48, -2) * mm, "radius": 0.15 * mm});
            skCircle(sketch, "E12.39.12.0", {"center": v(48, -3) * mm, "radius": 0.15 * mm});
            skCircle(sketch, "E12.39.13.0", {"center": v(48, -4) * mm, "radius": 0.15 * mm});
            skCircle(sketch, "E12.39.14.0", {"center": v(48, -5) * mm, "radius": 0.15 * mm});
            skCircle(sketch, "E12.39.15.0", {"center": v(48, -6) * mm, "radius": 0.15 * mm});
            skCircle(sketch, "E12.39.16.0", {"center": v(48, -7) * mm, "radius": 0.15 * mm});
            skCircle(sketch, "E12.39.17.0", {"center": v(48, -8) * mm, "radius": 0.15 * mm});
            skCircle(sketch, "E12.39.18.0", {"center": v(48, -9) * mm, "radius": 0.15 * mm});
            skCircle(sketch, "E12.39.19.0", {"center": v(48, -10) * mm, "radius": 0.15 * mm});
            skLineSegment(sketch, "E12.direction1", {"start": v(9, 9) * mm, "end": v(10, 9) * mm, "construction": true});
            skSolve(sketch);
        }
        {
            var Q0;
            Q0 = qSketchRegion(id + "F5", true);
            extrude(context, id + "F7", {"entities" : qUnion([Q0]), "operationType" : NewBodyOperationType.REMOVE, "endBound" : BoundingType.SYMMETRIC, "oppositeDirection" : true, "depth" : 25 * mm, "offsetDistance" : 25 * mm});
        }
        {
            var Q0;
            Q0 = qSketchRegion(id + "F6", true);
            extrude(context, id + "F8", {"entities" : qUnion([Q0]), "operationType" : NewBodyOperationType.REMOVE, "endBound" : BoundingType.SYMMETRIC, "oppositeDirection" : true, "depth" : 25 * mm, "offsetDistance" : 25 * mm});
        }
    });
